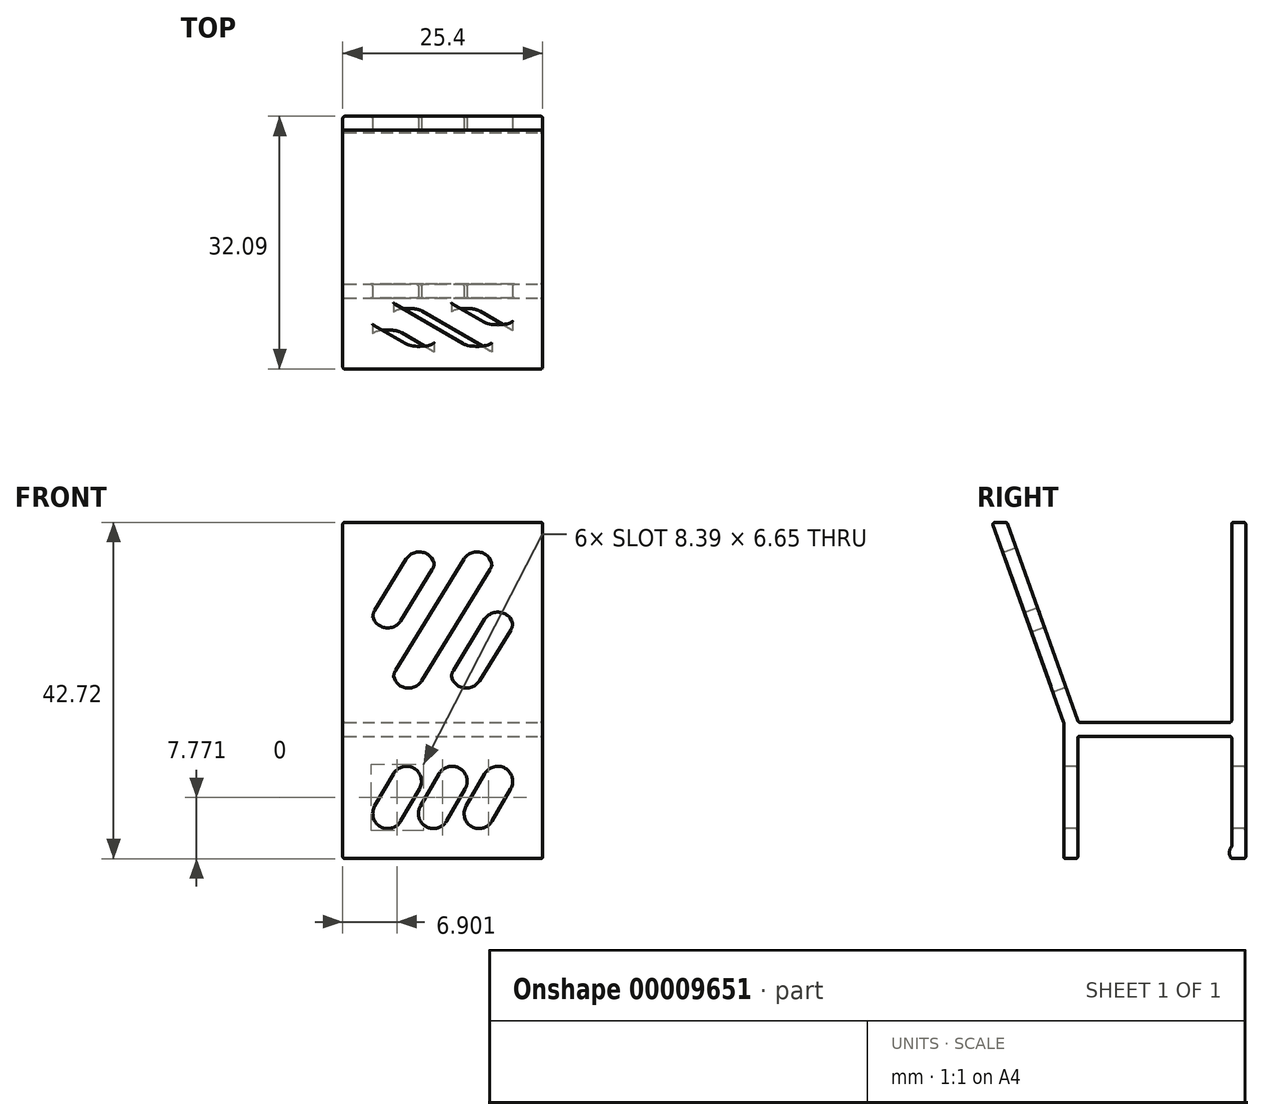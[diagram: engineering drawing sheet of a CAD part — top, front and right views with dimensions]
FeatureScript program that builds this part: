
annotation { "Feature Type Name" : "Feature", "Feature Type Description" : "" }
export const myFeature = defineFeature(function(context is Context, id is Id, definition is map)
    precondition{}
    {
        {
            var Q0;
            Q0=qCreatedBy(makeId("Right.planeOp"),FACE);
            var sketch = newSketch(context, id + "F0", { "sketchPlane" : qUnion([Q0])});
            skLineSegment(sketch, "E0.rect.bottom", {"start": v(9.78, 0.89) * mm, "end": v(-9.67, 0.89) * mm});
            skLineSegment(sketch, "E0.rect.top", {"start": v(9.78, -0.89) * mm, "end": v(-9.78, -0.89) * mm});
            skLineSegment(sketch, "E0.rect.left", {"start": v(11.56, 0.89) * mm, "end": v(11.56, -0.89) * mm});
            skLineSegment(sketch, "E0.rect.right", {"start": v(-11.56, 0.89) * mm, "end": v(-11.56, -0.89) * mm});
            skPoint(sketch, "E0.rect.middle", {"position": v(0, 0) * mm});
            skLineSegment(sketch, "E1.top", {"start": v(11.56, 26.29) * mm, "end": v(9.78, 26.29) * mm});
            skLineSegment(sketch, "E1.left", {"start": v(11.56, 0.89) * mm, "end": v(11.56, 26.29) * mm});
            skLineSegment(sketch, "E1.right", {"start": v(9.78, 0.89) * mm, "end": v(9.78, 26.29) * mm});
            skLineSegment(sketch, "E2", {"start": v(-11.56, 0.89) * mm, "end": v(-20.64, 26.29) * mm});
            skLineSegment(sketch, "E3", {"start": v(-20.64, 26.29) * mm, "end": v(-18.75, 26.29) * mm});
            skLineSegment(sketch, "E4", {"start": v(-18.75, 26.29) * mm, "end": v(-9.67, 0.89) * mm});
            skLineSegment(sketch, "E5.top", {"start": v(-11.56, -16.43) * mm, "end": v(-9.78, -16.43) * mm});
            skLineSegment(sketch, "E5.left", {"start": v(-11.56, -0.89) * mm, "end": v(-11.56, -16.43) * mm});
            skLineSegment(sketch, "E5.right", {"start": v(-9.78, -0.89) * mm, "end": v(-9.78, -16.43) * mm});
            skLineSegment(sketch, "E6.top", {"start": v(11.56, -16.43) * mm, "end": v(9.78, -16.43) * mm});
            skLineSegment(sketch, "E6.left", {"start": v(11.56, -0.89) * mm, "end": v(11.56, -16.43) * mm});
            skLineSegment(sketch, "E6.right", {"start": v(9.78, -0.89) * mm, "end": v(9.78, -14.9) * mm});
            skArc(sketch, "E7", {"start": v(9.78, -14.9) * mm, "mid": v(9.49, -15.67) * mm, "end": v(9.78, -16.43) * mm});
            skSolve(sketch);
        }
        {
            var Q0;
            Q0 = qSketchRegion(id + "F0", true);
            extrude(context, id + "F1", {"entities" : qUnion([Q0]), "oppositeDirection" : true, "depth" : 25.4 * mm});
        }
        {
            var Q0;
            Q0=makeQuery(id+"F1.opExtrude","SWEPT_FACE",FACE,{"disambiguationData":[OSD([sQuery(id+"F0.wireOp",EDGE,"E0.rect.right"),sQuery(id+"F0.wireOp",EDGE,"E5.left")])]});
            var sketch = newSketch(context, id + "F2", { "sketchPlane" : qUnion([Q0])});
            skLineSegment(sketch, "E8", {"start": v(0, 0) * mm, "end": v(-25.4, 0) * mm, "construction": true});
            skLineSegment(sketch, "E9", {"start": v(0, -0.89) * mm, "end": v(-25.4, -0.89) * mm, "construction": true});
            skArc(sketch, "E10", {"start": v(-21.33, -9.76) * mm, "mid": v(-20.64, -12.36) * mm, "end": v(-18.04, -11.67) * mm});
            skArc(sketch, "E11", {"start": v(-15.66, -7.56) * mm, "mid": v(-16.36, -4.95) * mm, "end": v(-18.96, -5.65) * mm});
            skLineSegment(sketch, "E12", {"start": v(-19.69, -10.71) * mm, "end": v(-17.31, -6.6) * mm, "construction": true});
            skLineSegment(sketch, "E13", {"start": v(-19.69, -10.71) * mm, "end": v(-10.98, -10.71) * mm, "construction": true});
            skLineSegment(sketch, "E14", {"start": v(-18.96, -5.65) * mm, "end": v(-21.33, -9.76) * mm});
            skLineSegment(sketch, "E15", {"start": v(-15.66, -7.56) * mm, "end": v(-18.04, -11.67) * mm});
            skArc(sketch, "E16.1.0.0", {"start": v(-9.86, -7.56) * mm, "mid": v(-10.56, -4.95) * mm, "end": v(-13.16, -5.65) * mm});
            skLineSegment(sketch, "E16.1.0.1", {"start": v(-13.16, -5.65) * mm, "end": v(-15.54, -9.76) * mm});
            skArc(sketch, "E16.1.0.2", {"start": v(-15.54, -9.76) * mm, "mid": v(-14.84, -12.36) * mm, "end": v(-12.24, -11.67) * mm});
            skLineSegment(sketch, "E16.1.0.3", {"start": v(-9.86, -7.56) * mm, "end": v(-12.24, -11.67) * mm});
            skArc(sketch, "E16.2.0.0", {"start": v(-4.07, -7.56) * mm, "mid": v(-4.76, -4.95) * mm, "end": v(-7.36, -5.65) * mm});
            skLineSegment(sketch, "E16.2.0.1", {"start": v(-7.36, -5.65) * mm, "end": v(-9.74, -9.76) * mm});
            skArc(sketch, "E16.2.0.2", {"start": v(-9.74, -9.76) * mm, "mid": v(-9.04, -12.36) * mm, "end": v(-6.44, -11.67) * mm});
            skLineSegment(sketch, "E16.2.0.3", {"start": v(-4.07, -7.56) * mm, "end": v(-6.44, -11.67) * mm});
            skLineSegment(sketch, "E16.direction1", {"start": v(-18.96, -5.65) * mm, "end": v(-13.16, -5.65) * mm, "construction": true});
            skSolve(sketch);
        }
        {
            var Q0;
            Q0 = qSketchRegion(id + "F2", true);
            extrude(context, id + "F3", {"entities" : qUnion([Q0]), "operationType" : NewBodyOperationType.REMOVE, "endBound" : BoundingType.THROUGH_ALL, "oppositeDirection" : true, "depth" : 25.4 * mm});
        }
        {
            var Q0;
            Q0=makeQuery(id+"F1.opExtrude","SWEPT_FACE",FACE,{"disambiguationData":[OSD([sQuery(id+"F0.wireOp",EDGE,"E2")])]});
            var sketch = newSketch(context, id + "F4", { "sketchPlane" : qUnion([Q0])});
            skArc(sketch, "E17", {"start": v(-18.7, 11.65) * mm, "mid": v(-18, 9.05) * mm, "end": v(-15.4, 9.75) * mm});
            skArc(sketch, "E18", {"start": v(-6.7, 24.78) * mm, "mid": v(-7.4, 27.39) * mm, "end": v(-10, 26.69) * mm});
            skLineSegment(sketch, "E19", {"start": v(-17.04, 10.7) * mm, "end": v(-9.9, 10.7) * mm, "construction": true});
            skLineSegment(sketch, "E20", {"start": v(-17.04, 10.7) * mm, "end": v(-8.36, 25.74) * mm, "construction": true});
            skLineSegment(sketch, "E21", {"start": v(-10, 26.69) * mm, "end": v(-18.7, 11.65) * mm});
            skLineSegment(sketch, "E22", {"start": v(-6.7, 24.78) * mm, "end": v(-15.4, 9.75) * mm});
            skLineSegment(sketch, "E23.0", {"start": v(-21.33, 19.77) * mm, "end": v(-17.34, 26.69) * mm});
            skLineSegment(sketch, "E24.0", {"start": v(-18.04, 17.87) * mm, "end": v(-14.04, 24.78) * mm});
            skArc(sketch, "E25", {"start": v(-17.34, 26.69) * mm, "mid": v(-14.74, 27.39) * mm, "end": v(-14.04, 24.78) * mm});
            skArc(sketch, "E26", {"start": v(-18.04, 17.87) * mm, "mid": v(-20.64, 17.17) * mm, "end": v(-21.33, 19.77) * mm});
            skLineSegment(sketch, "E27", {"start": v(4.18, 27.64) * mm, "end": v(-28.96, 27.64) * mm, "construction": true});
            skLineSegment(sketch, "E28", {"start": v(-29.07, 8.8) * mm, "end": v(4.54, 8.8) * mm, "construction": true});
            skLineSegment(sketch, "E29", {"start": v(-21.6, 33.76) * mm, "end": v(-21.59, -9.95) * mm, "construction": true});
            skLineSegment(sketch, "E30", {"start": v(-3.81, 33.76) * mm, "end": v(-3.8, -10.03) * mm, "construction": true});
            skLineSegment(sketch, "E31.0.MirrorCS", {"start": v(-8.06, 9.75) * mm, "end": v(-4.07, 16.66) * mm});
            skArc(sketch, "E32.0.MirrorCS", {"start": v(-4.07, 16.66) * mm, "mid": v(-4.76, 19.26) * mm, "end": v(-7.36, 18.57) * mm});
            skLineSegment(sketch, "E33.0.MirrorCS", {"start": v(-11.36, 11.65) * mm, "end": v(-7.36, 18.57) * mm});
            skArc(sketch, "E34", {"start": v(-8.06, 9.75) * mm, "mid": v(-10.66, 9.05) * mm, "end": v(-11.36, 11.65) * mm});
            skLineSegment(sketch, "E35", {"start": v(-12.7, 18.22) * mm, "end": v(-21.59, 18.22) * mm, "construction": true});
            skSolve(sketch);
        }
        {
            var Q0;
            Q0 = qSketchRegion(id + "F4", true);
            extrude(context, id + "F5", {"entities" : qUnion([Q0]), "operationType" : NewBodyOperationType.REMOVE, "endBound" : BoundingType.UP_TO_NEXT, "oppositeDirection" : true, "depth" : 25.4 * mm});
        }
        {
            var Q0;
            Q0=makeQuery(id+"F5.boolean.opBoolean","COPY",FACE,{"derivedFrom":makeQuery(id+"F5.opExtrude","SWEPT_FACE",FACE,{"disambiguationData":[OSD([sQuery(id+"F4.wireOp",EDGE,"f82c8603-6a34-46cd-9305-3e979d524e24.6.0.1")])]})});
            var Q1;
            Q1=makeQuery(id+"F5.boolean.opBoolean","COPY",EDGE,{"derivedFrom":makeQuery(id+"F5.opExtrude","CAP_EDGE",EDGE,{"disambiguationData":[OSD([sQuery(id+"F4.wireOp",EDGE,"f82c8603-6a34-46cd-9305-3e979d524e24.2.0.2")])],"isStart":true})});
            var Q2;
            Q2=makeQuery(id+"F5.boolean.opBoolean","COPY",EDGE,{"derivedFrom":makeQuery(id+"F5.opExtrude","CAP_EDGE",EDGE,{"disambiguationData":[OSD([sQuery(id+"F4.wireOp",EDGE,"f82c8603-6a34-46cd-9305-3e979d524e24.6.0.2")])],"isStart":true})});
            var Q3;
            Q3=makeQuery(id+"F5.boolean.opBoolean","COPY",EDGE,{"derivedFrom":makeQuery(id+"F5.opExtrude","CAP_EDGE",EDGE,{"disambiguationData":[OSD([sQuery(id+"F4.wireOp",EDGE,"f82c8603-6a34-46cd-9305-3e979d524e24.6.0.0")])],"isStart":true})});
            var Q4;
            Q4=makeQuery(id+"F5.boolean.opBoolean","COPY",FACE,{"derivedFrom":makeQuery(id+"F5.opExtrude","SWEPT_FACE",FACE,{"disambiguationData":[OSD([sQuery(id+"F4.wireOp",EDGE,"f82c8603-6a34-46cd-9305-3e979d524e24.6.0.0")])]})});
            var Q5;
            Q5=makeQuery(id+"F5.boolean.opBoolean","COPY",EDGE,{"derivedFrom":makeQuery(id+"F5.opExtrude","CAP_EDGE",EDGE,{"disambiguationData":[OSD([sQuery(id+"F4.wireOp",EDGE,"f82c8603-6a34-46cd-9305-3e979d524e24.2.0.1")])],"isStart":true})});
            var Q6;
            Q6=makeQuery(id+"F5.boolean.opBoolean","COPY",FACE,{"derivedFrom":makeQuery(id+"F5.opExtrude","SWEPT_FACE",FACE,{"disambiguationData":[OSD([sQuery(id+"F4.wireOp",EDGE,"f82c8603-6a34-46cd-9305-3e979d524e24.5.0.3")])]})});
            var Q7;
            Q7=makeQuery(id+"F5.boolean.opBoolean","COPY",EDGE,{"derivedFrom":makeQuery(id+"F5.opExtrude","TWEAK_EDGE",EDGE,{"derivedFrom":[makeQuery(id+"F1.opExtrude","SWEPT_FACE",FACE,{"disambiguationData":[OSD([sQuery(id+"F0.wireOp",EDGE,"E4")])]}),makeQuery(id+"F4.imprint","IMPRINT",EDGE,{"derivedFrom":sQuery(id+"F4.wireOp",EDGE,"f82c8603-6a34-46cd-9305-3e979d524e24.5.0.3")})]})});
            var Q8;
            Q8=makeQuery(id+"F5.boolean.opBoolean","COPY",EDGE,{"derivedFrom":makeQuery(id+"F5.opExtrude","CAP_EDGE",EDGE,{"disambiguationData":[OSD([sQuery(id+"F4.wireOp",EDGE,"f82c8603-6a34-46cd-9305-3e979d524e24.5.0.3")])],"isStart":true})});
            var Q9;
            Q9=makeQuery(id+"F5.boolean.opBoolean","COPY",EDGE,{"derivedFrom":makeQuery(id+"F5.opExtrude","CAP_EDGE",EDGE,{"disambiguationData":[OSD([sQuery(id+"F4.wireOp",EDGE,"f82c8603-6a34-46cd-9305-3e979d524e24.1.0.3")])],"isStart":true})});
            var Q10;
            Q10=makeQuery(id+"F5.boolean.opBoolean","COPY",FACE,{"derivedFrom":makeQuery(id+"F5.opExtrude","SWEPT_FACE",FACE,{"disambiguationData":[OSD([sQuery(id+"F4.wireOp",EDGE,"f82c8603-6a34-46cd-9305-3e979d524e24.5.0.2")])]})});
            var Q11;
            Q11=makeQuery(id+"F3.boolean.opBoolean","COPY",FACE,{"disambiguationData":[OD(0.0)],"derivedFrom":makeQuery(id+"F3.opExtrude","SWEPT_FACE",FACE,{"disambiguationData":[OSD([sQuery(id+"F2.wireOp",EDGE,"E16.4.0.1")])]})});
            var Q12;
            Q12=makeQuery(id+"F3.boolean.opBoolean","COPY",FACE,{"disambiguationData":[OD(0.0)],"derivedFrom":makeQuery(id+"F3.opExtrude","SWEPT_FACE",FACE,{"disambiguationData":[OSD([sQuery(id+"F2.wireOp",EDGE,"E16.2.0.1")])]})});
            var Q13;
            Q13=makeQuery(id+"F3.boolean.opBoolean","COPY",EDGE,{"derivedFrom":makeQuery(id+"F3.opExtrude","CAP_EDGE",EDGE,{"disambiguationData":[OSD([sQuery(id+"F2.wireOp",EDGE,"E16.5.0.3")])],"isStart":true})});
            var Q14;
            Q14=makeQuery(id+"F3.boolean.opBoolean","INTERSECT",EDGE,{"derivedFrom":[makeQuery(id+"F1.opExtrude","SWEPT_FACE",FACE,{"disambiguationData":[OSD([sQuery(id+"F0.wireOp",EDGE,"E5.right")])]}),makeQuery(id+"F3.opExtrude","SWEPT_FACE",FACE,{"disambiguationData":[OSD([sQuery(id+"F2.wireOp",EDGE,"E16.2.0.2")])]})]});
            var Q15;
            Q15=makeQuery(id+"F5.boolean.opBoolean","COPY",FACE,{"derivedFrom":makeQuery(id+"F5.opExtrude","SWEPT_FACE",FACE,{"disambiguationData":[OSD([sQuery(id+"F4.wireOp",EDGE,"f82c8603-6a34-46cd-9305-3e979d524e24.7.0.0")])]})});
            var Q16;
            Q16=makeQuery(id+"F3.boolean.opBoolean","COPY",FACE,{"disambiguationData":[OD(0.0)],"derivedFrom":makeQuery(id+"F3.opExtrude","SWEPT_FACE",FACE,{"disambiguationData":[OSD([sQuery(id+"F2.wireOp",EDGE,"E16.6.0.2")])]})});
            var Q17;
            Q17=makeQuery(id+"F3.boolean.opBoolean","COPY",FACE,{"disambiguationData":[OD(0.0)],"derivedFrom":makeQuery(id+"F3.opExtrude","SWEPT_FACE",FACE,{"disambiguationData":[OSD([sQuery(id+"F2.wireOp",EDGE,"E16.2.0.2")])]})});
            var Q18;
            Q18=makeQuery(id+"F3.boolean.opBoolean","COPY",FACE,{"disambiguationData":[OD(0.0)],"derivedFrom":makeQuery(id+"F3.opExtrude","SWEPT_FACE",FACE,{"disambiguationData":[OSD([sQuery(id+"F2.wireOp",EDGE,"E16.4.0.2")])]})});
            var Q19;
            Q19=makeQuery(id+"F3.boolean.opBoolean","COPY",EDGE,{"derivedFrom":makeQuery(id+"F3.opExtrude","CAP_EDGE",EDGE,{"disambiguationData":[OSD([sQuery(id+"F2.wireOp",EDGE,"E16.6.0.1")])],"isStart":true})});
            var Q20;
            Q20=makeQuery(id+"F3.boolean.opBoolean","INTERSECT",EDGE,{"derivedFrom":[makeQuery(id+"F1.opExtrude","SWEPT_FACE",FACE,{"disambiguationData":[OSD([sQuery(id+"F0.wireOp",EDGE,"E5.right")])]}),makeQuery(id+"F3.opExtrude","SWEPT_FACE",FACE,{"disambiguationData":[OSD([sQuery(id+"F2.wireOp",EDGE,"E16.2.0.1")])]})]});
            var Q21;
            Q21=makeQuery(id+"F5.boolean.opBoolean","COPY",FACE,{"derivedFrom":makeQuery(id+"F5.opExtrude","SWEPT_FACE",FACE,{"disambiguationData":[OSD([sQuery(id+"F4.wireOp",EDGE,"f82c8603-6a34-46cd-9305-3e979d524e24.6.0.3")])]})});
            var Q22;
            Q22=makeQuery(id+"F5.boolean.opBoolean","COPY",EDGE,{"derivedFrom":makeQuery(id+"F5.opExtrude","CAP_EDGE",EDGE,{"disambiguationData":[OSD([sQuery(id+"F4.wireOp",EDGE,"f82c8603-6a34-46cd-9305-3e979d524e24.7.0.0")])],"isStart":true})});
            var Q23;
            Q23=makeQuery(id+"F3.boolean.opBoolean","COPY",EDGE,{"derivedFrom":makeQuery(id+"F3.opExtrude","CAP_EDGE",EDGE,{"disambiguationData":[OSD([sQuery(id+"F2.wireOp",EDGE,"E16.6.0.3")])],"isStart":true})});
            var Q24;
            Q24=makeQuery(id+"F5.boolean.opBoolean","COPY",EDGE,{"derivedFrom":makeQuery(id+"F5.opExtrude","TWEAK_EDGE",EDGE,{"derivedFrom":[makeQuery(id+"F1.opExtrude","SWEPT_FACE",FACE,{"disambiguationData":[OSD([sQuery(id+"F0.wireOp",EDGE,"E4")])]}),makeQuery(id+"F4.imprint","IMPRINT",EDGE,{"derivedFrom":sQuery(id+"F4.wireOp",EDGE,"f82c8603-6a34-46cd-9305-3e979d524e24.6.0.3")})]})});
            var Q25;
            Q25=makeQuery(id+"F5.boolean.opBoolean","COPY",EDGE,{"derivedFrom":makeQuery(id+"F5.opExtrude","CAP_EDGE",EDGE,{"disambiguationData":[OSD([sQuery(id+"F4.wireOp",EDGE,"f82c8603-6a34-46cd-9305-3e979d524e24.6.0.3")])],"isStart":true})});
            var Q26;
            Q26=makeQuery(id+"F5.boolean.opBoolean","COPY",EDGE,{"derivedFrom":makeQuery(id+"F5.opExtrude","CAP_EDGE",EDGE,{"disambiguationData":[OSD([sQuery(id+"F4.wireOp",EDGE,"f82c8603-6a34-46cd-9305-3e979d524e24.2.0.3")])],"isStart":true})});
            var Q27;
            Q27=makeQuery(id+"F1.opExtrude","CAP_EDGE",EDGE,{"disambiguationData":[OSD([sQuery(id+"F0.wireOp",EDGE,"E1.right")])],"isStart":false});
            var Q28;
            Q28=makeQuery(id+"F3.boolean.opBoolean","COPY",FACE,{"disambiguationData":[OD(0.0)],"derivedFrom":makeQuery(id+"F3.opExtrude","SWEPT_FACE",FACE,{"disambiguationData":[OSD([sQuery(id+"F2.wireOp",EDGE,"E16.5.0.0")])]})});
            var Q29;
            Q29=makeQuery(id+"F3.boolean.opBoolean","COPY",FACE,{"disambiguationData":[OD(0.0)],"derivedFrom":makeQuery(id+"F3.opExtrude","SWEPT_FACE",FACE,{"disambiguationData":[OSD([sQuery(id+"F2.wireOp",EDGE,"E16.3.0.0")])]})});
            var Q30;
            Q30=makeQuery(id+"F3.boolean.opBoolean","COPY",FACE,{"disambiguationData":[OD(0.0)],"derivedFrom":makeQuery(id+"F3.opExtrude","SWEPT_FACE",FACE,{"disambiguationData":[OSD([sQuery(id+"F2.wireOp",EDGE,"E16.7.0.0")])]})});
            var Q31;
            Q31=makeQuery(id+"F1.opExtrude","CAP_EDGE",EDGE,{"disambiguationData":[OSD([sQuery(id+"F0.wireOp",EDGE,"E6.right")])],"isStart":true});
            var Q32;
            Q32=makeQuery(id+"F1.opExtrude","CAP_EDGE",EDGE,{"disambiguationData":[OSD([sQuery(id+"F0.wireOp",EDGE,"E0.rect.right"),sQuery(id+"F0.wireOp",EDGE,"E5.left")])],"isStart":true});
            var Q33;
            Q33=makeQuery(id+"F3.boolean.opBoolean","INTERSECT",EDGE,{"derivedFrom":[makeQuery(id+"F1.opExtrude","SWEPT_FACE",FACE,{"disambiguationData":[OSD([sQuery(id+"F0.wireOp",EDGE,"E5.right")])]}),makeQuery(id+"F3.opExtrude","SWEPT_FACE",FACE,{"disambiguationData":[OSD([sQuery(id+"F2.wireOp",EDGE,"E16.5.0.1")])]})]});
            var Q34;
            Q34=makeQuery(id+"F3.boolean.opBoolean","COPY",EDGE,{"derivedFrom":makeQuery(id+"F3.opExtrude","CAP_EDGE",EDGE,{"disambiguationData":[OSD([sQuery(id+"F2.wireOp",EDGE,"E16.5.0.1")])],"isStart":true})});
            var Q35;
            Q35=makeQuery(id+"F3.boolean.opBoolean","COPY",EDGE,{"derivedFrom":makeQuery(id+"F3.opExtrude","CAP_EDGE",EDGE,{"disambiguationData":[OSD([sQuery(id+"F2.wireOp",EDGE,"E16.5.0.0")])],"isStart":true})});
            var Q36;
            Q36=makeQuery(id+"F3.boolean.opBoolean","COPY",FACE,{"disambiguationData":[OD(0.0)],"derivedFrom":makeQuery(id+"F3.opExtrude","SWEPT_FACE",FACE,{"disambiguationData":[OSD([sQuery(id+"F2.wireOp",EDGE,"E16.6.0.0")])]})});
            var Q37;
            Q37=makeQuery(id+"F3.boolean.opBoolean","COPY",FACE,{"disambiguationData":[OD(0.0)],"derivedFrom":makeQuery(id+"F3.opExtrude","SWEPT_FACE",FACE,{"disambiguationData":[OSD([sQuery(id+"F2.wireOp",EDGE,"E16.4.0.0")])]})});
            var Q38;
            Q38=makeQuery(id+"F3.boolean.opBoolean","COPY",FACE,{"disambiguationData":[OD(0.0)],"derivedFrom":makeQuery(id+"F3.opExtrude","SWEPT_FACE",FACE,{"disambiguationData":[OSD([sQuery(id+"F2.wireOp",EDGE,"E16.2.0.0")])]})});
            var Q39;
            Q39=makeQuery(id+"F1.opExtrude","CAP_EDGE",EDGE,{"disambiguationData":[OSD([sQuery(id+"F0.wireOp",EDGE,"E0.rect.top")])],"isStart":true});
            var Q40;
            Q40=makeQuery(id+"F3.boolean.opBoolean","COPY",EDGE,{"derivedFrom":makeQuery(id+"F3.opExtrude","CAP_EDGE",EDGE,{"disambiguationData":[OSD([sQuery(id+"F2.wireOp",EDGE,"E16.4.0.3")])],"isStart":true})});
            var Q41;
            Q41=makeQuery(id+"F3.boolean.opBoolean","COPY",FACE,{"disambiguationData":[OD(1.0)],"derivedFrom":makeQuery(id+"F3.opExtrude","SWEPT_FACE",FACE,{"disambiguationData":[OSD([sQuery(id+"F2.wireOp",EDGE,"E16.7.0.3")])]})});
            var Q42;
            Q42=makeQuery(id+"F5.boolean.opBoolean","COPY",FACE,{"derivedFrom":makeQuery(id+"F5.opExtrude","SWEPT_FACE",FACE,{"disambiguationData":[OSD([sQuery(id+"F4.wireOp",EDGE,"f82c8603-6a34-46cd-9305-3e979d524e24.7.0.3")])]})});
            var Q43;
            Q43=makeQuery(id+"F1.opExtrude","CAP_EDGE",EDGE,{"disambiguationData":[OSD([sQuery(id+"F0.wireOp",EDGE,"E0.rect.left"),sQuery(id+"F0.wireOp",EDGE,"E1.left"),sQuery(id+"F0.wireOp",EDGE,"E6.left")])],"isStart":true});
            var Q44;
            Q44=makeQuery(id+"F1.opExtrude","CAP_EDGE",EDGE,{"disambiguationData":[OSD([sQuery(id+"F0.wireOp",EDGE,"E5.right")])],"isStart":true});
            var Q45;
            Q45=makeQuery(id+"F3.boolean.opBoolean","INTERSECT",EDGE,{"derivedFrom":[makeQuery(id+"F1.opExtrude","SWEPT_FACE",FACE,{"disambiguationData":[OSD([sQuery(id+"F0.wireOp",EDGE,"E5.right")])]}),makeQuery(id+"F3.opExtrude","SWEPT_FACE",FACE,{"disambiguationData":[OSD([sQuery(id+"F2.wireOp",EDGE,"E14")])]})]});
            var Q46;
            Q46=makeQuery(id+"F3.boolean.opBoolean","INTERSECT",EDGE,{"derivedFrom":[makeQuery(id+"F1.opExtrude","SWEPT_FACE",FACE,{"disambiguationData":[OSD([sQuery(id+"F0.wireOp",EDGE,"E5.right")])]}),makeQuery(id+"F3.opExtrude","SWEPT_FACE",FACE,{"disambiguationData":[OSD([sQuery(id+"F2.wireOp",EDGE,"E16.4.0.2")])]})]});
            var Q47;
            Q47=makeQuery(id+"F3.boolean.opBoolean","COPY",FACE,{"disambiguationData":[OD(0.0)],"derivedFrom":makeQuery(id+"F3.opExtrude","SWEPT_FACE",FACE,{"disambiguationData":[OSD([sQuery(id+"F2.wireOp",EDGE,"E16.3.0.2")])]})});
            var Q48;
            Q48=makeQuery(id+"F3.boolean.opBoolean","COPY",FACE,{"disambiguationData":[OD(0.0)],"derivedFrom":makeQuery(id+"F3.opExtrude","SWEPT_FACE",FACE,{"disambiguationData":[OSD([sQuery(id+"F2.wireOp",EDGE,"E16.1.0.2")])]})});
            var Q49;
            Q49=makeQuery(id+"F3.boolean.opBoolean","COPY",FACE,{"disambiguationData":[OD(0.0)],"derivedFrom":makeQuery(id+"F3.opExtrude","SWEPT_FACE",FACE,{"disambiguationData":[OSD([sQuery(id+"F2.wireOp",EDGE,"E16.7.0.2")])]})});
            var Q50;
            Q50=makeQuery(id+"F3.boolean.opBoolean","COPY",FACE,{"disambiguationData":[OD(0.0)],"derivedFrom":makeQuery(id+"F3.opExtrude","SWEPT_FACE",FACE,{"disambiguationData":[OSD([sQuery(id+"F2.wireOp",EDGE,"E16.5.0.2")])]})});
            var Q51;
            Q51=makeQuery(id+"F3.boolean.opBoolean","COPY",FACE,{"disambiguationData":[OD(1.0)],"derivedFrom":makeQuery(id+"F3.opExtrude","SWEPT_FACE",FACE,{"disambiguationData":[OSD([sQuery(id+"F2.wireOp",EDGE,"E16.7.0.2")])]})});
            var Q52;
            Q52=makeQuery(id+"F3.boolean.opBoolean","INTERSECT",EDGE,{"derivedFrom":[makeQuery(id+"F1.opExtrude","SWEPT_FACE",FACE,{"disambiguationData":[OSD([sQuery(id+"F0.wireOp",EDGE,"E5.right")])]}),makeQuery(id+"F3.opExtrude","SWEPT_FACE",FACE,{"disambiguationData":[OSD([sQuery(id+"F2.wireOp",EDGE,"E16.4.0.1")])]})]});
            var Q53;
            Q53=makeQuery(id+"F5.boolean.opBoolean","COPY",FACE,{"derivedFrom":makeQuery(id+"F5.opExtrude","SWEPT_FACE",FACE,{"disambiguationData":[OSD([sQuery(id+"F4.wireOp",EDGE,"f82c8603-6a34-46cd-9305-3e979d524e24.7.0.1")])]})});
            var Q54;
            Q54=makeQuery(id+"F3.boolean.opBoolean","COPY",EDGE,{"derivedFrom":makeQuery(id+"F3.opExtrude","CAP_EDGE",EDGE,{"disambiguationData":[OSD([sQuery(id+"F2.wireOp",EDGE,"E16.4.0.1")])],"isStart":true})});
            var Q55;
            Q55=makeQuery(id+"F5.boolean.opBoolean","COPY",EDGE,{"derivedFrom":makeQuery(id+"F5.opExtrude","CAP_EDGE",EDGE,{"disambiguationData":[OSD([sQuery(id+"F4.wireOp",EDGE,"f82c8603-6a34-46cd-9305-3e979d524e24.3.0.1")])],"isStart":true})});
            var Q56;
            Q56=makeQuery(id+"F5.boolean.opBoolean","COPY",FACE,{"derivedFrom":makeQuery(id+"F5.opExtrude","SWEPT_FACE",FACE,{"disambiguationData":[OSD([sQuery(id+"F4.wireOp",EDGE,"f82c8603-6a34-46cd-9305-3e979d524e24.7.0.2")])]})});
            var Q57;
            Q57=makeQuery(id+"F5.boolean.opBoolean","COPY",EDGE,{"derivedFrom":makeQuery(id+"F5.opExtrude","CAP_EDGE",EDGE,{"disambiguationData":[OSD([sQuery(id+"F4.wireOp",EDGE,"f82c8603-6a34-46cd-9305-3e979d524e24.3.0.2")])],"isStart":true})});
            var Q58;
            Q58=makeQuery(id+"F5.boolean.opBoolean","COPY",EDGE,{"derivedFrom":makeQuery(id+"F5.opExtrude","CAP_EDGE",EDGE,{"disambiguationData":[OSD([sQuery(id+"F4.wireOp",EDGE,"f82c8603-6a34-46cd-9305-3e979d524e24.7.0.2")])],"isStart":true})});
            var Q59;
            Q59=makeQuery(id+"F5.boolean.opBoolean","COPY",EDGE,{"derivedFrom":makeQuery(id+"F5.opExtrude","CAP_EDGE",EDGE,{"disambiguationData":[OSD([sQuery(id+"F4.wireOp",EDGE,"f82c8603-6a34-46cd-9305-3e979d524e24.7.0.3")])],"isStart":true})});
            var Q60;
            Q60=makeQuery(id+"F5.boolean.opBoolean","COPY",EDGE,{"derivedFrom":makeQuery(id+"F5.opExtrude","CAP_EDGE",EDGE,{"disambiguationData":[OSD([sQuery(id+"F4.wireOp",EDGE,"f82c8603-6a34-46cd-9305-3e979d524e24.3.0.3")])],"isStart":true})});
            var Q61;
            Q61=makeQuery(id+"F5.boolean.opBoolean","COPY",EDGE,{"derivedFrom":makeQuery(id+"F5.opExtrude","TWEAK_EDGE",EDGE,{"derivedFrom":[makeQuery(id+"F1.opExtrude","SWEPT_FACE",FACE,{"disambiguationData":[OSD([sQuery(id+"F0.wireOp",EDGE,"E4")])]}),makeQuery(id+"F4.imprint","IMPRINT",EDGE,{"derivedFrom":sQuery(id+"F4.wireOp",EDGE,"f82c8603-6a34-46cd-9305-3e979d524e24.7.0.3")})]})});
            var Q62;
            Q62=makeQuery(id+"F3.boolean.opBoolean","COPY",EDGE,{"derivedFrom":makeQuery(id+"F3.opExtrude","CAP_EDGE",EDGE,{"disambiguationData":[OSD([sQuery(id+"F2.wireOp",EDGE,"E16.7.0.3")])],"isStart":true})});
            var Q63;
            Q63=makeQuery(id+"F3.boolean.opBoolean","INTERSECT",EDGE,{"derivedFrom":[makeQuery(id+"F1.opExtrude","SWEPT_FACE",FACE,{"disambiguationData":[OSD([sQuery(id+"F0.wireOp",EDGE,"E6.right")])]}),makeQuery(id+"F3.opExtrude","SWEPT_FACE",FACE,{"disambiguationData":[OSD([sQuery(id+"F2.wireOp",EDGE,"E16.7.0.3")])]})]});
            var Q64;
            Q64=makeQuery(id+"F5.boolean.opBoolean","COPY",EDGE,{"derivedFrom":makeQuery(id+"F5.opExtrude","TWEAK_EDGE",EDGE,{"derivedFrom":[makeQuery(id+"F1.opExtrude","SWEPT_FACE",FACE,{"disambiguationData":[OSD([sQuery(id+"F0.wireOp",EDGE,"E4")])]}),makeQuery(id+"F4.imprint","IMPRINT",EDGE,{"derivedFrom":sQuery(id+"F4.wireOp",EDGE,"f82c8603-6a34-46cd-9305-3e979d524e24.1.0.1")})]})});
            var Q65;
            Q65=makeQuery(id+"F5.boolean.opBoolean","COPY",FACE,{"derivedFrom":makeQuery(id+"F5.opExtrude","SWEPT_FACE",FACE,{"disambiguationData":[OSD([sQuery(id+"F4.wireOp",EDGE,"f82c8603-6a34-46cd-9305-3e979d524e24.1.0.1")])]})});
            var Q66;
            Q66=makeQuery(id+"F5.boolean.opBoolean","COPY",FACE,{"derivedFrom":makeQuery(id+"F5.opExtrude","SWEPT_FACE",FACE,{"disambiguationData":[OSD([sQuery(id+"F4.wireOp",EDGE,"f82c8603-6a34-46cd-9305-3e979d524e24.1.0.2")])]})});
            var Q67;
            Q67=makeQuery(id+"F3.boolean.opBoolean","INTERSECT",EDGE,{"derivedFrom":[makeQuery(id+"F1.opExtrude","SWEPT_FACE",FACE,{"disambiguationData":[OSD([sQuery(id+"F0.wireOp",EDGE,"E5.right")])]}),makeQuery(id+"F3.opExtrude","SWEPT_FACE",FACE,{"disambiguationData":[OSD([sQuery(id+"F2.wireOp",EDGE,"E16.3.0.2")])]})]});
            var Q68;
            Q68=makeQuery(id+"F5.boolean.opBoolean","COPY",FACE,{"derivedFrom":makeQuery(id+"F5.opExtrude","SWEPT_FACE",FACE,{"disambiguationData":[OSD([sQuery(id+"F4.wireOp",EDGE,"f82c8603-6a34-46cd-9305-3e979d524e24.1.0.3")])]})});
            var Q69;
            Q69=makeQuery(id+"F5.boolean.opBoolean","COPY",FACE,{"derivedFrom":makeQuery(id+"F5.opExtrude","SWEPT_FACE",FACE,{"disambiguationData":[OSD([sQuery(id+"F4.wireOp",EDGE,"E18")])]})});
            var Q70;
            Q70=makeQuery(id+"F3.boolean.opBoolean","COPY",EDGE,{"derivedFrom":makeQuery(id+"F3.opExtrude","CAP_EDGE",EDGE,{"disambiguationData":[OSD([sQuery(id+"F2.wireOp",EDGE,"E16.7.0.2")])],"isStart":true})});
            var Q71;
            Q71=makeQuery(id+"F5.boolean.opBoolean","COPY",FACE,{"derivedFrom":makeQuery(id+"F5.opExtrude","SWEPT_FACE",FACE,{"disambiguationData":[OSD([sQuery(id+"F4.wireOp",EDGE,"E21")])]})});
            var Q72;
            Q72=makeQuery(id+"F5.boolean.opBoolean","COPY",EDGE,{"derivedFrom":makeQuery(id+"F5.opExtrude","TWEAK_EDGE",EDGE,{"derivedFrom":[makeQuery(id+"F1.opExtrude","SWEPT_FACE",FACE,{"disambiguationData":[OSD([sQuery(id+"F0.wireOp",EDGE,"E4")])]}),makeQuery(id+"F4.imprint","IMPRINT",EDGE,{"derivedFrom":sQuery(id+"F4.wireOp",EDGE,"E21")})]})});
            var Q73;
            Q73=makeQuery(id+"F5.boolean.opBoolean","COPY",FACE,{"derivedFrom":makeQuery(id+"F5.opExtrude","SWEPT_FACE",FACE,{"disambiguationData":[OSD([sQuery(id+"F4.wireOp",EDGE,"f82c8603-6a34-46cd-9305-3e979d524e24.1.0.0")])]})});
            var Q74;
            Q74=makeQuery(id+"F5.boolean.opBoolean","COPY",FACE,{"derivedFrom":makeQuery(id+"F5.opExtrude","SWEPT_FACE",FACE,{"disambiguationData":[OSD([sQuery(id+"F4.wireOp",EDGE,"f82c8603-6a34-46cd-9305-3e979d524e24.3.0.0")])]})});
            var Q75;
            Q75=makeQuery(id+"F5.boolean.opBoolean","COPY",FACE,{"derivedFrom":makeQuery(id+"F5.opExtrude","SWEPT_FACE",FACE,{"disambiguationData":[OSD([sQuery(id+"F4.wireOp",EDGE,"f82c8603-6a34-46cd-9305-3e979d524e24.2.0.0")])]})});
            var Q76;
            Q76=makeQuery(id+"F3.boolean.opBoolean","COPY",FACE,{"disambiguationData":[OD(0.0)],"derivedFrom":makeQuery(id+"F3.opExtrude","SWEPT_FACE",FACE,{"disambiguationData":[OSD([sQuery(id+"F2.wireOp",EDGE,"E16.3.0.1")])]})});
            var Q77;
            Q77=makeQuery(id+"F5.boolean.opBoolean","COPY",FACE,{"derivedFrom":makeQuery(id+"F5.opExtrude","SWEPT_FACE",FACE,{"disambiguationData":[OSD([sQuery(id+"F4.wireOp",EDGE,"f82c8603-6a34-46cd-9305-3e979d524e24.2.0.1")])]})});
            var Q78;
            Q78=makeQuery(id+"F5.boolean.opBoolean","COPY",FACE,{"derivedFrom":makeQuery(id+"F5.opExtrude","SWEPT_FACE",FACE,{"disambiguationData":[OSD([sQuery(id+"F4.wireOp",EDGE,"f82c8603-6a34-46cd-9305-3e979d524e24.2.0.2")])]})});
            var Q79;
            Q79=makeQuery(id+"F5.boolean.opBoolean","COPY",FACE,{"derivedFrom":makeQuery(id+"F5.opExtrude","SWEPT_FACE",FACE,{"disambiguationData":[OSD([sQuery(id+"F4.wireOp",EDGE,"f82c8603-6a34-46cd-9305-3e979d524e24.2.0.3")])]})});
            var Q80;
            Q80=makeQuery(id+"F5.boolean.opBoolean","COPY",EDGE,{"derivedFrom":makeQuery(id+"F5.opExtrude","TWEAK_EDGE",EDGE,{"derivedFrom":[makeQuery(id+"F1.opExtrude","SWEPT_FACE",FACE,{"disambiguationData":[OSD([sQuery(id+"F0.wireOp",EDGE,"E4")])]}),makeQuery(id+"F4.imprint","IMPRINT",EDGE,{"derivedFrom":sQuery(id+"F4.wireOp",EDGE,"f82c8603-6a34-46cd-9305-3e979d524e24.2.0.3")})]})});
            var Q81;
            Q81=makeQuery(id+"F5.boolean.opBoolean","COPY",FACE,{"derivedFrom":makeQuery(id+"F5.opExtrude","SWEPT_FACE",FACE,{"disambiguationData":[OSD([sQuery(id+"F4.wireOp",EDGE,"f82c8603-6a34-46cd-9305-3e979d524e24.3.0.2")])]})});
            var Q82;
            Q82=makeQuery(id+"F5.boolean.opBoolean","COPY",EDGE,{"derivedFrom":makeQuery(id+"F5.opExtrude","TWEAK_EDGE",EDGE,{"derivedFrom":[makeQuery(id+"F1.opExtrude","SWEPT_FACE",FACE,{"disambiguationData":[OSD([sQuery(id+"F0.wireOp",EDGE,"E4")])]}),makeQuery(id+"F4.imprint","IMPRINT",EDGE,{"derivedFrom":sQuery(id+"F4.wireOp",EDGE,"f82c8603-6a34-46cd-9305-3e979d524e24.3.0.3")})]})});
            var Q83;
            Q83=makeQuery(id+"F5.boolean.opBoolean","COPY",FACE,{"derivedFrom":makeQuery(id+"F5.opExtrude","SWEPT_FACE",FACE,{"disambiguationData":[OSD([sQuery(id+"F4.wireOp",EDGE,"E17")])]})});
            var Q84;
            Q84=makeQuery(id+"F5.boolean.opBoolean","COPY",FACE,{"derivedFrom":makeQuery(id+"F5.opExtrude","SWEPT_FACE",FACE,{"disambiguationData":[OSD([sQuery(id+"F4.wireOp",EDGE,"f82c8603-6a34-46cd-9305-3e979d524e24.3.0.3")])]})});
            var Q85;
            Q85=makeQuery(id+"F5.boolean.opBoolean","COPY",FACE,{"derivedFrom":makeQuery(id+"F5.opExtrude","SWEPT_FACE",FACE,{"disambiguationData":[OSD([sQuery(id+"F4.wireOp",EDGE,"f82c8603-6a34-46cd-9305-3e979d524e24.3.0.1")])]})});
            var Q86;
            Q86=makeQuery(id+"F5.boolean.opBoolean","COPY",EDGE,{"derivedFrom":makeQuery(id+"F5.opExtrude","TWEAK_EDGE",EDGE,{"derivedFrom":[makeQuery(id+"F1.opExtrude","SWEPT_FACE",FACE,{"disambiguationData":[OSD([sQuery(id+"F0.wireOp",EDGE,"E4")])]}),makeQuery(id+"F4.imprint","IMPRINT",EDGE,{"derivedFrom":sQuery(id+"F4.wireOp",EDGE,"f82c8603-6a34-46cd-9305-3e979d524e24.3.0.1")})]})});
            var Q87;
            Q87=makeQuery(id+"F3.boolean.opBoolean","COPY",FACE,{"disambiguationData":[OD(0.0)],"derivedFrom":makeQuery(id+"F3.opExtrude","SWEPT_FACE",FACE,{"disambiguationData":[OSD([sQuery(id+"F2.wireOp",EDGE,"E11")])]})});
            var Q88;
            Q88=makeQuery(id+"F3.boolean.opBoolean","COPY",EDGE,{"derivedFrom":makeQuery(id+"F3.opExtrude","CAP_EDGE",EDGE,{"disambiguationData":[OSD([sQuery(id+"F2.wireOp",EDGE,"E16.7.0.1")])],"isStart":true})});
            var Q89;
            Q89=makeQuery(id+"F3.boolean.opBoolean","COPY",FACE,{"disambiguationData":[OD(0.0)],"derivedFrom":makeQuery(id+"F3.opExtrude","SWEPT_FACE",FACE,{"disambiguationData":[OSD([sQuery(id+"F2.wireOp",EDGE,"E10")])]})});
            var Q90;
            Q90=makeQuery(id+"F3.boolean.opBoolean","COPY",EDGE,{"derivedFrom":makeQuery(id+"F3.opExtrude","CAP_EDGE",EDGE,{"disambiguationData":[OSD([sQuery(id+"F2.wireOp",EDGE,"E16.1.0.1")])],"isStart":true})});
            var Q91;
            Q91=makeQuery(id+"F3.boolean.opBoolean","COPY",EDGE,{"derivedFrom":makeQuery(id+"F3.opExtrude","CAP_EDGE",EDGE,{"disambiguationData":[OSD([sQuery(id+"F2.wireOp",EDGE,"E14")])],"isStart":true})});
            var Q92;
            Q92=makeQuery(id+"F1.opExtrude","SWEPT_FACE",FACE,{"disambiguationData":[OSD([sQuery(id+"F0.wireOp",EDGE,"E5.right")])]});
            var Q93;
            Q93=makeQuery(id+"F3.boolean.opBoolean","COPY",EDGE,{"derivedFrom":makeQuery(id+"F3.opExtrude","CAP_EDGE",EDGE,{"disambiguationData":[OSD([sQuery(id+"F2.wireOp",EDGE,"E15")])],"isStart":true})});
            var Q94;
            Q94=makeQuery(id+"F1.opExtrude","SWEPT_FACE",FACE,{"disambiguationData":[OSD([sQuery(id+"F0.wireOp",EDGE,"E6.right")])]});
            var Q95;
            Q95=makeQuery(id+"F1.opExtrude","SWEPT_FACE",FACE,{"disambiguationData":[OSD([sQuery(id+"F0.wireOp",EDGE,"E0.rect.left"),sQuery(id+"F0.wireOp",EDGE,"E1.left"),sQuery(id+"F0.wireOp",EDGE,"E6.left")])]});
            var Q96;
            Q96=makeQuery(id+"F3.boolean.opBoolean","COPY",EDGE,{"derivedFrom":makeQuery(id+"F3.opExtrude","CAP_EDGE",EDGE,{"disambiguationData":[OSD([sQuery(id+"F2.wireOp",EDGE,"E11")])],"isStart":true})});
            var Q97;
            Q97=makeQuery(id+"F1.opExtrude","SWEPT_FACE",FACE,{"disambiguationData":[OSD([sQuery(id+"F0.wireOp",EDGE,"E0.rect.right"),sQuery(id+"F0.wireOp",EDGE,"E5.left")])]});
            var Q98;
            Q98=makeQuery(id+"F5.boolean.opBoolean","COPY",EDGE,{"derivedFrom":makeQuery(id+"F5.opExtrude","CAP_EDGE",EDGE,{"disambiguationData":[OSD([sQuery(id+"F4.wireOp",EDGE,"E18")])],"isStart":true})});
            var Q99;
            Q99=makeQuery(id+"F5.boolean.opBoolean","COPY",EDGE,{"derivedFrom":makeQuery(id+"F5.opExtrude","CAP_EDGE",EDGE,{"disambiguationData":[OSD([sQuery(id+"F4.wireOp",EDGE,"f82c8603-6a34-46cd-9305-3e979d524e24.4.0.1")])],"isStart":true})});
            var Q100;
            Q100=makeQuery(id+"F3.boolean.opBoolean","COPY",EDGE,{"derivedFrom":makeQuery(id+"F3.opExtrude","CAP_EDGE",EDGE,{"disambiguationData":[OSD([sQuery(id+"F2.wireOp",EDGE,"E16.2.0.3")])],"isStart":true})});
            var Q101;
            Q101=makeQuery(id+"F3.boolean.opBoolean","COPY",FACE,{"disambiguationData":[OD(0.0)],"derivedFrom":makeQuery(id+"F3.opExtrude","SWEPT_FACE",FACE,{"disambiguationData":[OSD([sQuery(id+"F2.wireOp",EDGE,"E16.1.0.0")])]})});
            var Q102;
            Q102=makeQuery(id+"F3.boolean.opBoolean","COPY",EDGE,{"derivedFrom":makeQuery(id+"F3.opExtrude","CAP_EDGE",EDGE,{"disambiguationData":[OSD([sQuery(id+"F2.wireOp",EDGE,"E16.2.0.1")])],"isStart":true})});
            var Q103;
            Q103=makeQuery(id+"F3.boolean.opBoolean","COPY",EDGE,{"derivedFrom":makeQuery(id+"F3.opExtrude","CAP_EDGE",EDGE,{"disambiguationData":[OSD([sQuery(id+"F2.wireOp",EDGE,"E16.1.0.3")])],"isStart":true})});
            var Q104;
            Q104=makeQuery(id+"F3.boolean.opBoolean","COPY",FACE,{"disambiguationData":[OD(0.0)],"derivedFrom":makeQuery(id+"F3.opExtrude","SWEPT_FACE",FACE,{"disambiguationData":[OSD([sQuery(id+"F2.wireOp",EDGE,"E14")])]})});
            var Q105;
            Q105=makeQuery(id+"F5.boolean.opBoolean","COPY",FACE,{"derivedFrom":makeQuery(id+"F5.opExtrude","SWEPT_FACE",FACE,{"disambiguationData":[OSD([sQuery(id+"F4.wireOp",EDGE,"f82c8603-6a34-46cd-9305-3e979d524e24.4.0.0")])]})});
            var Q106;
            Q106=makeQuery(id+"F1.opExtrude","SWEPT_FACE",FACE,{"disambiguationData":[OSD([sQuery(id+"F0.wireOp",EDGE,"E2")])]});
            var Q107;
            Q107=makeQuery(id+"F3.boolean.opBoolean","COPY",FACE,{"disambiguationData":[OD(0.0)],"derivedFrom":makeQuery(id+"F3.opExtrude","SWEPT_FACE",FACE,{"disambiguationData":[OSD([sQuery(id+"F2.wireOp",EDGE,"E16.1.0.1")])]})});
            var Q108;
            Q108=makeQuery(id+"F3.boolean.opBoolean","COPY",EDGE,{"derivedFrom":makeQuery(id+"F3.opExtrude","CAP_EDGE",EDGE,{"disambiguationData":[OSD([sQuery(id+"F2.wireOp",EDGE,"E16.3.0.3")])],"isStart":true})});
            var Q109;
            Q109=makeQuery(id+"F3.boolean.opBoolean","COPY",EDGE,{"derivedFrom":makeQuery(id+"F3.opExtrude","CAP_EDGE",EDGE,{"disambiguationData":[OSD([sQuery(id+"F2.wireOp",EDGE,"E16.3.0.2")])],"isStart":true})});
            var Q110;
            Q110=makeQuery(id+"F3.boolean.opBoolean","COPY",EDGE,{"derivedFrom":makeQuery(id+"F3.opExtrude","CAP_EDGE",EDGE,{"disambiguationData":[OSD([sQuery(id+"F2.wireOp",EDGE,"E16.3.0.1")])],"isStart":true})});
            var Q111;
            Q111=makeQuery(id+"F1.opExtrude","SWEPT_FACE",FACE,{"disambiguationData":[OSD([sQuery(id+"F0.wireOp",EDGE,"E0.rect.bottom")])]});
            var Q112;
            Q112=makeQuery(id+"F1.opExtrude","SWEPT_EDGE",EDGE,{"disambiguationData":[OSD([sQuery(id+"F0.wireOp",EDGE,"E0.rect.bottom"),sQuery(id+"F0.wireOp",EDGE,"E1.right")])]});
            var Q113;
            Q113=makeQuery(id+"F1.opExtrude","CAP_FACE",FACE,{"disambiguationData":[OSD([sQuery(id+"F0.wireOp",EDGE,"E0.rect.bottom"),sQuery(id+"F0.wireOp",EDGE,"E0.rect.top"),sQuery(id+"F0.wireOp",EDGE,"E0.rect.left"),sQuery(id+"F0.wireOp",EDGE,"E0.rect.right"),sQuery(id+"F0.wireOp",EDGE,"E1.top"),sQuery(id+"F0.wireOp",EDGE,"E1.left"),sQuery(id+"F0.wireOp",EDGE,"E1.right"),sQuery(id+"F0.wireOp",EDGE,"E2"),sQuery(id+"F0.wireOp",EDGE,"E3"),sQuery(id+"F0.wireOp",EDGE,"E4"),sQuery(id+"F0.wireOp",EDGE,"E5.top"),sQuery(id+"F0.wireOp",EDGE,"E5.left"),sQuery(id+"F0.wireOp",EDGE,"E5.right"),sQuery(id+"F0.wireOp",EDGE,"E6.top"),sQuery(id+"F0.wireOp",EDGE,"E6.left"),sQuery(id+"F0.wireOp",EDGE,"E6.right"),sQuery(id+"F0.wireOp",EDGE,"E7")])],"isStart":true});
            var Q114;
            Q114=makeQuery(id+"F1.opExtrude","CAP_FACE",FACE,{"disambiguationData":[OSD([sQuery(id+"F0.wireOp",EDGE,"E0.rect.bottom"),sQuery(id+"F0.wireOp",EDGE,"E0.rect.top"),sQuery(id+"F0.wireOp",EDGE,"E0.rect.left"),sQuery(id+"F0.wireOp",EDGE,"E0.rect.right"),sQuery(id+"F0.wireOp",EDGE,"E1.top"),sQuery(id+"F0.wireOp",EDGE,"E1.left"),sQuery(id+"F0.wireOp",EDGE,"E1.right"),sQuery(id+"F0.wireOp",EDGE,"E2"),sQuery(id+"F0.wireOp",EDGE,"E3"),sQuery(id+"F0.wireOp",EDGE,"E4"),sQuery(id+"F0.wireOp",EDGE,"E5.top"),sQuery(id+"F0.wireOp",EDGE,"E5.left"),sQuery(id+"F0.wireOp",EDGE,"E5.right"),sQuery(id+"F0.wireOp",EDGE,"E6.top"),sQuery(id+"F0.wireOp",EDGE,"E6.left"),sQuery(id+"F0.wireOp",EDGE,"E6.right"),sQuery(id+"F0.wireOp",EDGE,"E7")])],"isStart":false});
            var Q115;
            Q115=makeQuery(id+"F1.opExtrude","SWEPT_FACE",FACE,{"disambiguationData":[OSD([sQuery(id+"F0.wireOp",EDGE,"E0.rect.top")])]});
            var Q116;
            Q116=makeQuery(id+"F1.opExtrude","SWEPT_EDGE",EDGE,{"disambiguationData":[OSD([sQuery(id+"F0.wireOp",EDGE,"E0.rect.right"),sQuery(id+"F0.wireOp",EDGE,"E2")])]});
            var Q117;
            Q117=makeQuery(id+"F1.opExtrude","SWEPT_EDGE",EDGE,{"disambiguationData":[OSD([sQuery(id+"F0.wireOp",EDGE,"E1.top"),sQuery(id+"F0.wireOp",EDGE,"E1.left")])]});
            var Q118;
            Q118=makeQuery(id+"F1.opExtrude","SWEPT_EDGE",EDGE,{"disambiguationData":[OSD([sQuery(id+"F0.wireOp",EDGE,"E1.top"),sQuery(id+"F0.wireOp",EDGE,"E1.right")])]});
            var Q119;
            Q119=makeQuery(id+"F5.boolean.opBoolean","COPY",FACE,{"derivedFrom":makeQuery(id+"F5.opExtrude","SWEPT_FACE",FACE,{"disambiguationData":[OSD([sQuery(id+"F4.wireOp",EDGE,"f82c8603-6a34-46cd-9305-3e979d524e24.4.0.2")])]})});
            var Q120;
            Q120=makeQuery(id+"F1.opExtrude","SWEPT_FACE",FACE,{"disambiguationData":[OSD([sQuery(id+"F0.wireOp",EDGE,"E1.top")])]});
            var Q121;
            Q121=makeQuery(id+"F1.opExtrude","SWEPT_FACE",FACE,{"disambiguationData":[OSD([sQuery(id+"F0.wireOp",EDGE,"E1.right")])]});
            var Q122;
            Q122=makeQuery(id+"F1.opExtrude","SWEPT_EDGE",EDGE,{"disambiguationData":[OSD([sQuery(id+"F0.wireOp",EDGE,"E2"),sQuery(id+"F0.wireOp",EDGE,"E3")])]});
            var Q123;
            Q123=makeQuery(id+"F1.opExtrude","SWEPT_EDGE",EDGE,{"disambiguationData":[OSD([sQuery(id+"F0.wireOp",EDGE,"E3"),sQuery(id+"F0.wireOp",EDGE,"E4")])]});
            var Q124;
            Q124=makeQuery(id+"F1.opExtrude","SWEPT_FACE",FACE,{"disambiguationData":[OSD([sQuery(id+"F0.wireOp",EDGE,"E3")])]});
            var Q125;
            Q125=makeQuery(id+"F1.opExtrude","SWEPT_EDGE",EDGE,{"disambiguationData":[OSD([sQuery(id+"F0.wireOp",EDGE,"E5.top"),sQuery(id+"F0.wireOp",EDGE,"E5.left")])]});
            var Q126;
            Q126=makeQuery(id+"F1.opExtrude","SWEPT_FACE",FACE,{"disambiguationData":[OSD([sQuery(id+"F0.wireOp",EDGE,"E5.top")])]});
            var Q127;
            Q127=makeQuery(id+"F1.opExtrude","SWEPT_EDGE",EDGE,{"disambiguationData":[OSD([sQuery(id+"F0.wireOp",EDGE,"E6.top"),sQuery(id+"F0.wireOp",EDGE,"E7")])]});
            var Q128;
            Q128=makeQuery(id+"F5.boolean.opBoolean","COPY",EDGE,{"derivedFrom":makeQuery(id+"F5.opExtrude","CAP_EDGE",EDGE,{"disambiguationData":[OSD([sQuery(id+"F4.wireOp",EDGE,"f82c8603-6a34-46cd-9305-3e979d524e24.4.0.2")])],"isStart":true})});
            var Q129;
            Q129=makeQuery(id+"F5.boolean.opBoolean","COPY",EDGE,{"derivedFrom":makeQuery(id+"F5.opExtrude","CAP_EDGE",EDGE,{"disambiguationData":[OSD([sQuery(id+"F4.wireOp",EDGE,"E21")])],"isStart":true})});
            var Q130;
            Q130=makeQuery(id+"F1.opExtrude","SWEPT_FACE",FACE,{"disambiguationData":[OSD([sQuery(id+"F0.wireOp",EDGE,"E4")])]});
            var Q131;
            Q131=makeQuery(id+"F5.boolean.opBoolean","COPY",FACE,{"derivedFrom":makeQuery(id+"F5.opExtrude","SWEPT_FACE",FACE,{"disambiguationData":[OSD([sQuery(id+"F4.wireOp",EDGE,"f82c8603-6a34-46cd-9305-3e979d524e24.4.0.1")])]})});
            var Q132;
            Q132=makeQuery(id+"F1.opExtrude","SWEPT_FACE",FACE,{"disambiguationData":[OSD([sQuery(id+"F0.wireOp",EDGE,"E7")])]});
            var Q133;
            Q133=makeQuery(id+"F1.opExtrude","CAP_EDGE",EDGE,{"disambiguationData":[OSD([sQuery(id+"F0.wireOp",EDGE,"E0.rect.bottom")])],"isStart":true});
            var Q134;
            Q134=makeQuery(id+"F1.opExtrude","SWEPT_EDGE",EDGE,{"disambiguationData":[OSD([sQuery(id+"F0.wireOp",EDGE,"E6.right"),sQuery(id+"F0.wireOp",EDGE,"E7")])]});
            var Q135;
            Q135=makeQuery(id+"F1.opExtrude","CAP_EDGE",EDGE,{"disambiguationData":[OSD([sQuery(id+"F0.wireOp",EDGE,"E0.rect.bottom")])],"isStart":false});
            var Q136;
            Q136=makeQuery(id+"F5.boolean.opBoolean","COPY",EDGE,{"derivedFrom":makeQuery(id+"F5.opExtrude","CAP_EDGE",EDGE,{"disambiguationData":[OSD([sQuery(id+"F4.wireOp",EDGE,"f82c8603-6a34-46cd-9305-3e979d524e24.4.0.3")])],"isStart":true})});
            var Q137;
            Q137=makeQuery(id+"F5.boolean.opBoolean","COPY",EDGE,{"derivedFrom":makeQuery(id+"F5.opExtrude","CAP_EDGE",EDGE,{"disambiguationData":[OSD([sQuery(id+"F4.wireOp",EDGE,"E22")])],"isStart":true})});
            var Q138;
            Q138=makeQuery(id+"F5.boolean.opBoolean","COPY",EDGE,{"derivedFrom":makeQuery(id+"F5.opExtrude","TWEAK_EDGE",EDGE,{"derivedFrom":[makeQuery(id+"F1.opExtrude","SWEPT_FACE",FACE,{"disambiguationData":[OSD([sQuery(id+"F0.wireOp",EDGE,"E4")])]}),makeQuery(id+"F4.imprint","IMPRINT",EDGE,{"derivedFrom":sQuery(id+"F4.wireOp",EDGE,"f82c8603-6a34-46cd-9305-3e979d524e24.4.0.3")})]})});
            var Q139;
            Q139=makeQuery(id+"F5.boolean.opBoolean","COPY",FACE,{"derivedFrom":makeQuery(id+"F5.opExtrude","SWEPT_FACE",FACE,{"disambiguationData":[OSD([sQuery(id+"F4.wireOp",EDGE,"f82c8603-6a34-46cd-9305-3e979d524e24.4.0.3")])]})});
            var Q140;
            Q140=makeQuery(id+"F5.boolean.opBoolean","COPY",FACE,{"derivedFrom":makeQuery(id+"F5.opExtrude","SWEPT_FACE",FACE,{"disambiguationData":[OSD([sQuery(id+"F4.wireOp",EDGE,"f82c8603-6a34-46cd-9305-3e979d524e24.5.0.0")])]})});
            var Q141;
            Q141=makeQuery(id+"F5.boolean.opBoolean","COPY",EDGE,{"derivedFrom":makeQuery(id+"F5.opExtrude","CAP_EDGE",EDGE,{"disambiguationData":[OSD([sQuery(id+"F4.wireOp",EDGE,"f82c8603-6a34-46cd-9305-3e979d524e24.1.0.0")])],"isStart":true})});
            var Q142;
            Q142=makeQuery(id+"F5.boolean.opBoolean","COPY",FACE,{"derivedFrom":makeQuery(id+"F5.opExtrude","SWEPT_FACE",FACE,{"disambiguationData":[OSD([sQuery(id+"F4.wireOp",EDGE,"f82c8603-6a34-46cd-9305-3e979d524e24.5.0.1")])]})});
            var Q143;
            Q143=makeQuery(id+"F5.boolean.opBoolean","COPY",EDGE,{"derivedFrom":makeQuery(id+"F5.opExtrude","TWEAK_EDGE",EDGE,{"derivedFrom":[makeQuery(id+"F1.opExtrude","SWEPT_FACE",FACE,{"disambiguationData":[OSD([sQuery(id+"F0.wireOp",EDGE,"E4")])]}),makeQuery(id+"F4.imprint","IMPRINT",EDGE,{"derivedFrom":sQuery(id+"F4.wireOp",EDGE,"f82c8603-6a34-46cd-9305-3e979d524e24.5.0.1")})]})});
            var Q144;
            Q144=makeQuery(id+"F5.boolean.opBoolean","COPY",EDGE,{"derivedFrom":makeQuery(id+"F5.opExtrude","CAP_EDGE",EDGE,{"disambiguationData":[OSD([sQuery(id+"F4.wireOp",EDGE,"f82c8603-6a34-46cd-9305-3e979d524e24.1.0.1")])],"isStart":true})});
            var Q145;
            Q145=makeQuery(id+"F5.boolean.opBoolean","COPY",EDGE,{"derivedFrom":makeQuery(id+"F5.opExtrude","CAP_EDGE",EDGE,{"disambiguationData":[OSD([sQuery(id+"F4.wireOp",EDGE,"f82c8603-6a34-46cd-9305-3e979d524e24.1.0.2")])],"isStart":true})});
            var Q146;
            Q146=makeQuery(id+"F5.boolean.opBoolean","COPY",EDGE,{"derivedFrom":makeQuery(id+"F5.opExtrude","CAP_EDGE",EDGE,{"disambiguationData":[OSD([sQuery(id+"F4.wireOp",EDGE,"f82c8603-6a34-46cd-9305-3e979d524e24.5.0.2")])],"isStart":true})});
            var Q147;
            Q147=makeQuery(id+"F5.boolean.opBoolean","COPY",EDGE,{"derivedFrom":makeQuery(id+"F5.opExtrude","SWEPT_EDGE",EDGE,{"disambiguationData":[OSD([sQuery(id+"F4.wireOp",EDGE,"f82c8603-6a34-46cd-9305-3e979d524e24.2.0.1"),sQuery(id+"F4.wireOp",EDGE,"f82c8603-6a34-46cd-9305-3e979d524e24.2.0.3")])]})});
            var Q148;
            Q148=makeQuery(id+"F5.boolean.opBoolean","COPY",EDGE,{"derivedFrom":makeQuery(id+"F5.opExtrude","SWEPT_EDGE",EDGE,{"disambiguationData":[OSD([sQuery(id+"F4.wireOp",EDGE,"f82c8603-6a34-46cd-9305-3e979d524e24.6.0.1"),sQuery(id+"F4.wireOp",EDGE,"f82c8603-6a34-46cd-9305-3e979d524e24.6.0.3")])]})});
            var Q149;
            Q149=makeQuery(id+"F5.boolean.opBoolean","COPY",EDGE,{"derivedFrom":makeQuery(id+"F5.opExtrude","TWEAK_EDGE",EDGE,{"derivedFrom":[makeQuery(id+"F1.opExtrude","SWEPT_FACE",FACE,{"disambiguationData":[OSD([sQuery(id+"F0.wireOp",EDGE,"E4")])]}),makeQuery(id+"F4.imprint","IMPRINT",EDGE,{"derivedFrom":sQuery(id+"F4.wireOp",EDGE,"f82c8603-6a34-46cd-9305-3e979d524e24.6.0.2")})]})});
            var Q150;
            Q150=makeQuery(id+"F5.boolean.opBoolean","COPY",EDGE,{"derivedFrom":makeQuery(id+"F5.opExtrude","CAP_EDGE",EDGE,{"disambiguationData":[OSD([sQuery(id+"F4.wireOp",EDGE,"f82c8603-6a34-46cd-9305-3e979d524e24.2.0.0")])],"isStart":true})});
            var Q151;
            Q151=makeQuery(id+"F5.boolean.opBoolean","COPY",EDGE,{"derivedFrom":makeQuery(id+"F5.opExtrude","SWEPT_EDGE",EDGE,{"disambiguationData":[OSD([sQuery(id+"F4.wireOp",EDGE,"f82c8603-6a34-46cd-9305-3e979d524e24.2.0.0"),sQuery(id+"F4.wireOp",EDGE,"f82c8603-6a34-46cd-9305-3e979d524e24.2.0.2")])]})});
            var Q152;
            Q152=makeQuery(id+"F5.boolean.opBoolean","COPY",EDGE,{"derivedFrom":makeQuery(id+"F5.opExtrude","SWEPT_EDGE",EDGE,{"disambiguationData":[OSD([sQuery(id+"F4.wireOp",EDGE,"f82c8603-6a34-46cd-9305-3e979d524e24.6.0.0"),sQuery(id+"F4.wireOp",EDGE,"f82c8603-6a34-46cd-9305-3e979d524e24.6.0.2")])]})});
            var Q153;
            Q153=makeQuery(id+"F3.boolean.opBoolean","INTERSECT",EDGE,{"derivedFrom":[makeQuery(id+"F1.opExtrude","SWEPT_FACE",FACE,{"disambiguationData":[OSD([sQuery(id+"F0.wireOp",EDGE,"E5.right")])]}),makeQuery(id+"F3.opExtrude","SWEPT_FACE",FACE,{"disambiguationData":[OSD([sQuery(id+"F2.wireOp",EDGE,"E16.1.0.2")])]})]});
            var Q154;
            Q154=makeQuery(id+"F3.boolean.opBoolean","INTERSECT",EDGE,{"derivedFrom":[makeQuery(id+"F1.opExtrude","SWEPT_FACE",FACE,{"disambiguationData":[OSD([sQuery(id+"F0.wireOp",EDGE,"E5.right")])]}),makeQuery(id+"F3.opExtrude","SWEPT_FACE",FACE,{"disambiguationData":[OSD([sQuery(id+"F2.wireOp",EDGE,"E16.5.0.2")])]})]});
            var Q155;
            Q155=makeQuery(id+"F5.boolean.opBoolean","COPY",EDGE,{"derivedFrom":makeQuery(id+"F5.opExtrude","SWEPT_EDGE",EDGE,{"disambiguationData":[OSD([sQuery(id+"F4.wireOp",EDGE,"f82c8603-6a34-46cd-9305-3e979d524e24.6.0.0"),sQuery(id+"F4.wireOp",EDGE,"f82c8603-6a34-46cd-9305-3e979d524e24.6.0.3")])]})});
            var Q156;
            Q156=makeQuery(id+"F3.boolean.opBoolean","COPY",EDGE,{"disambiguationData":[OD(0.0)],"derivedFrom":makeQuery(id+"F3.opExtrude","SWEPT_EDGE",EDGE,{"disambiguationData":[OSD([sQuery(id+"F2.wireOp",EDGE,"E16.6.0.2"),sQuery(id+"F2.wireOp",EDGE,"E16.6.0.3")])]})});
            var Q157;
            Q157=makeQuery(id+"F5.boolean.opBoolean","COPY",EDGE,{"derivedFrom":makeQuery(id+"F5.opExtrude","SWEPT_EDGE",EDGE,{"disambiguationData":[OSD([sQuery(id+"F4.wireOp",EDGE,"f82c8603-6a34-46cd-9305-3e979d524e24.2.0.0"),sQuery(id+"F4.wireOp",EDGE,"f82c8603-6a34-46cd-9305-3e979d524e24.2.0.3")])]})});
            var Q158;
            Q158=makeQuery(id+"F3.boolean.opBoolean","COPY",EDGE,{"disambiguationData":[OD(0.0)],"derivedFrom":makeQuery(id+"F3.opExtrude","SWEPT_EDGE",EDGE,{"disambiguationData":[OSD([sQuery(id+"F2.wireOp",EDGE,"E16.4.0.2"),sQuery(id+"F2.wireOp",EDGE,"E16.4.0.3")])]})});
            var Q159;
            Q159=makeQuery(id+"F5.boolean.opBoolean","COPY",EDGE,{"derivedFrom":makeQuery(id+"F5.opExtrude","CAP_EDGE",EDGE,{"disambiguationData":[OSD([sQuery(id+"F4.wireOp",EDGE,"f82c8603-6a34-46cd-9305-3e979d524e24.6.0.1")])],"isStart":true})});
            var Q160;
            Q160=makeQuery(id+"F3.boolean.opBoolean","COPY",EDGE,{"derivedFrom":makeQuery(id+"F3.opExtrude","CAP_EDGE",EDGE,{"disambiguationData":[OSD([sQuery(id+"F2.wireOp",EDGE,"E16.5.0.2")])],"isStart":true})});
            var Q161;
            Q161=makeQuery(id+"F5.boolean.opBoolean","COPY",EDGE,{"derivedFrom":makeQuery(id+"F5.opExtrude","TWEAK_EDGE",EDGE,{"derivedFrom":[makeQuery(id+"F1.opExtrude","SWEPT_FACE",FACE,{"disambiguationData":[OSD([sQuery(id+"F0.wireOp",EDGE,"E4")])]}),makeQuery(id+"F4.imprint","IMPRINT",EDGE,{"derivedFrom":sQuery(id+"F4.wireOp",EDGE,"f82c8603-6a34-46cd-9305-3e979d524e24.6.0.1")})]})});
            var Q162;
            Q162=makeQuery(id+"F3.boolean.opBoolean","COPY",EDGE,{"disambiguationData":[OD(0.0)],"derivedFrom":makeQuery(id+"F3.opExtrude","SWEPT_EDGE",EDGE,{"disambiguationData":[OSD([sQuery(id+"F2.wireOp",EDGE,"E16.2.0.2"),sQuery(id+"F2.wireOp",EDGE,"E16.2.0.3")])]})});
            var Q163;
            Q163=makeQuery(id+"F3.boolean.opBoolean","COPY",EDGE,{"disambiguationData":[OD(0.0)],"derivedFrom":makeQuery(id+"F3.opExtrude","SWEPT_EDGE",EDGE,{"disambiguationData":[OSD([sQuery(id+"F2.wireOp",EDGE,"E11"),sQuery(id+"F2.wireOp",EDGE,"E14")])]})});
            var Q164;
            Q164=makeQuery(id+"F3.boolean.opBoolean","INTERSECT",EDGE,{"derivedFrom":[makeQuery(id+"F1.opExtrude","SWEPT_FACE",FACE,{"disambiguationData":[OSD([sQuery(id+"F0.wireOp",EDGE,"E6.right")])]}),makeQuery(id+"F3.opExtrude","SWEPT_FACE",FACE,{"disambiguationData":[OSD([sQuery(id+"F2.wireOp",EDGE,"E16.1.0.3")])]})]});
            var Q165;
            Q165=makeQuery(id+"F3.boolean.opBoolean","INTERSECT",EDGE,{"derivedFrom":[makeQuery(id+"F1.opExtrude","SWEPT_FACE",FACE,{"disambiguationData":[OSD([sQuery(id+"F0.wireOp",EDGE,"E6.right")])]}),makeQuery(id+"F3.opExtrude","SWEPT_FACE",FACE,{"disambiguationData":[OSD([sQuery(id+"F2.wireOp",EDGE,"E16.5.0.3")])]})]});
            var Q166;
            Q166=makeQuery(id+"F3.boolean.opBoolean","INTERSECT",EDGE,{"derivedFrom":[makeQuery(id+"F1.opExtrude","SWEPT_FACE",FACE,{"disambiguationData":[OSD([sQuery(id+"F0.wireOp",EDGE,"E5.right")])]}),makeQuery(id+"F3.opExtrude","SWEPT_FACE",FACE,{"disambiguationData":[OSD([sQuery(id+"F2.wireOp",EDGE,"E16.1.0.3")])]})]});
            var Q167;
            Q167=makeQuery(id+"F3.boolean.opBoolean","INTERSECT",EDGE,{"derivedFrom":[makeQuery(id+"F1.opExtrude","SWEPT_FACE",FACE,{"disambiguationData":[OSD([sQuery(id+"F0.wireOp",EDGE,"E0.rect.left"),sQuery(id+"F0.wireOp",EDGE,"E1.left"),sQuery(id+"F0.wireOp",EDGE,"E6.left")])]}),makeQuery(id+"F3.opExtrude","SWEPT_FACE",FACE,{"disambiguationData":[OSD([sQuery(id+"F2.wireOp",EDGE,"E16.1.0.3")])]})]});
            var Q168;
            Q168=makeQuery(id+"F3.boolean.opBoolean","INTERSECT",EDGE,{"derivedFrom":[makeQuery(id+"F1.opExtrude","SWEPT_FACE",FACE,{"disambiguationData":[OSD([sQuery(id+"F0.wireOp",EDGE,"E0.rect.left"),sQuery(id+"F0.wireOp",EDGE,"E1.left"),sQuery(id+"F0.wireOp",EDGE,"E6.left")])]}),makeQuery(id+"F3.opExtrude","SWEPT_FACE",FACE,{"disambiguationData":[OSD([sQuery(id+"F2.wireOp",EDGE,"E16.5.0.3")])]})]});
            var Q169;
            Q169=makeQuery(id+"F3.boolean.opBoolean","COPY",FACE,{"disambiguationData":[OD(1.0)],"derivedFrom":makeQuery(id+"F3.opExtrude","SWEPT_FACE",FACE,{"disambiguationData":[OSD([sQuery(id+"F2.wireOp",EDGE,"E16.4.0.1")])]})});
            var Q170;
            Q170=makeQuery(id+"F3.boolean.opBoolean","COPY",FACE,{"disambiguationData":[OD(1.0)],"derivedFrom":makeQuery(id+"F3.opExtrude","SWEPT_FACE",FACE,{"disambiguationData":[OSD([sQuery(id+"F2.wireOp",EDGE,"E16.2.0.1")])]})});
            var Q171;
            Q171=makeQuery(id+"F3.boolean.opBoolean","COPY",FACE,{"disambiguationData":[OD(1.0)],"derivedFrom":makeQuery(id+"F3.opExtrude","SWEPT_FACE",FACE,{"disambiguationData":[OSD([sQuery(id+"F2.wireOp",EDGE,"E16.6.0.1")])]})});
            var Q172;
            Q172=makeQuery(id+"F5.boolean.opBoolean","COPY",EDGE,{"derivedFrom":makeQuery(id+"F5.opExtrude","SWEPT_EDGE",EDGE,{"disambiguationData":[OSD([sQuery(id+"F4.wireOp",EDGE,"f82c8603-6a34-46cd-9305-3e979d524e24.5.0.1"),sQuery(id+"F4.wireOp",EDGE,"f82c8603-6a34-46cd-9305-3e979d524e24.5.0.2")])]})});
            var Q173;
            Q173=makeQuery(id+"F5.boolean.opBoolean","COPY",EDGE,{"derivedFrom":makeQuery(id+"F5.opExtrude","SWEPT_EDGE",EDGE,{"disambiguationData":[OSD([sQuery(id+"F4.wireOp",EDGE,"f82c8603-6a34-46cd-9305-3e979d524e24.1.0.1"),sQuery(id+"F4.wireOp",EDGE,"f82c8603-6a34-46cd-9305-3e979d524e24.1.0.2")])]})});
            var Q174;
            Q174=makeQuery(id+"F5.boolean.opBoolean","COPY",EDGE,{"derivedFrom":makeQuery(id+"F5.opExtrude","TWEAK_EDGE",EDGE,{"derivedFrom":[makeQuery(id+"F1.opExtrude","SWEPT_FACE",FACE,{"disambiguationData":[OSD([sQuery(id+"F0.wireOp",EDGE,"E4")])]}),makeQuery(id+"F4.imprint","IMPRINT",EDGE,{"derivedFrom":sQuery(id+"F4.wireOp",EDGE,"f82c8603-6a34-46cd-9305-3e979d524e24.6.0.0")})]})});
            var Q175;
            Q175=makeQuery(id+"F3.boolean.opBoolean","COPY",EDGE,{"disambiguationData":[OD(0.0)],"derivedFrom":makeQuery(id+"F3.opExtrude","SWEPT_EDGE",EDGE,{"disambiguationData":[OSD([sQuery(id+"F2.wireOp",EDGE,"E16.3.0.0"),sQuery(id+"F2.wireOp",EDGE,"E16.3.0.3")])]})});
            var Q176;
            Q176=makeQuery(id+"F3.boolean.opBoolean","COPY",EDGE,{"disambiguationData":[OD(0.0)],"derivedFrom":makeQuery(id+"F3.opExtrude","SWEPT_EDGE",EDGE,{"disambiguationData":[OSD([sQuery(id+"F2.wireOp",EDGE,"E16.7.0.0"),sQuery(id+"F2.wireOp",EDGE,"E16.7.0.3")])]})});
            var Q177;
            Q177=makeQuery(id+"F3.boolean.opBoolean","COPY",EDGE,{"disambiguationData":[OD(0.0)],"derivedFrom":makeQuery(id+"F3.opExtrude","SWEPT_EDGE",EDGE,{"disambiguationData":[OSD([sQuery(id+"F2.wireOp",EDGE,"E16.5.0.0"),sQuery(id+"F2.wireOp",EDGE,"E16.5.0.3")])]})});
            var Q178;
            Q178=makeQuery(id+"F3.boolean.opBoolean","COPY",EDGE,{"derivedFrom":makeQuery(id+"F3.opExtrude","CAP_EDGE",EDGE,{"disambiguationData":[OSD([sQuery(id+"F2.wireOp",EDGE,"E16.6.0.0")])],"isStart":true})});
            var Q179;
            Q179=makeQuery(id+"F3.boolean.opBoolean","COPY",FACE,{"disambiguationData":[OD(0.0)],"derivedFrom":makeQuery(id+"F3.opExtrude","SWEPT_FACE",FACE,{"disambiguationData":[OSD([sQuery(id+"F2.wireOp",EDGE,"E16.6.0.1")])]})});
            var Q180;
            Q180=makeQuery(id+"F3.boolean.opBoolean","COPY",FACE,{"disambiguationData":[OD(1.0)],"derivedFrom":makeQuery(id+"F3.opExtrude","SWEPT_FACE",FACE,{"disambiguationData":[OSD([sQuery(id+"F2.wireOp",EDGE,"E16.6.0.2")])]})});
            var Q181;
            Q181=makeQuery(id+"F3.boolean.opBoolean","COPY",FACE,{"disambiguationData":[OD(1.0)],"derivedFrom":makeQuery(id+"F3.opExtrude","SWEPT_FACE",FACE,{"disambiguationData":[OSD([sQuery(id+"F2.wireOp",EDGE,"E16.4.0.2")])]})});
            var Q182;
            Q182=makeQuery(id+"F3.boolean.opBoolean","COPY",FACE,{"disambiguationData":[OD(1.0)],"derivedFrom":makeQuery(id+"F3.opExtrude","SWEPT_FACE",FACE,{"disambiguationData":[OSD([sQuery(id+"F2.wireOp",EDGE,"E16.2.0.2")])]})});
            var Q183;
            Q183=makeQuery(id+"F3.boolean.opBoolean","INTERSECT",EDGE,{"derivedFrom":[makeQuery(id+"F1.opExtrude","SWEPT_FACE",FACE,{"disambiguationData":[OSD([sQuery(id+"F0.wireOp",EDGE,"E5.right")])]}),makeQuery(id+"F3.opExtrude","SWEPT_FACE",FACE,{"disambiguationData":[OSD([sQuery(id+"F2.wireOp",EDGE,"E16.6.0.2")])]})]});
            var Q184;
            Q184=makeQuery(id+"F3.boolean.opBoolean","INTERSECT",EDGE,{"derivedFrom":[makeQuery(id+"F1.opExtrude","SWEPT_FACE",FACE,{"disambiguationData":[OSD([sQuery(id+"F0.wireOp",EDGE,"E0.rect.left"),sQuery(id+"F0.wireOp",EDGE,"E1.left"),sQuery(id+"F0.wireOp",EDGE,"E6.left")])]}),makeQuery(id+"F3.opExtrude","SWEPT_FACE",FACE,{"disambiguationData":[OSD([sQuery(id+"F2.wireOp",EDGE,"E16.6.0.2")])]})]});
            var Q185;
            Q185=makeQuery(id+"F3.boolean.opBoolean","INTERSECT",EDGE,{"derivedFrom":[makeQuery(id+"F1.opExtrude","SWEPT_FACE",FACE,{"disambiguationData":[OSD([sQuery(id+"F0.wireOp",EDGE,"E0.rect.left"),sQuery(id+"F0.wireOp",EDGE,"E1.left"),sQuery(id+"F0.wireOp",EDGE,"E6.left")])]}),makeQuery(id+"F3.opExtrude","SWEPT_FACE",FACE,{"disambiguationData":[OSD([sQuery(id+"F2.wireOp",EDGE,"E16.2.0.2")])]})]});
            var Q186;
            Q186=makeQuery(id+"F3.boolean.opBoolean","INTERSECT",EDGE,{"derivedFrom":[makeQuery(id+"F1.opExtrude","SWEPT_FACE",FACE,{"disambiguationData":[OSD([sQuery(id+"F0.wireOp",EDGE,"E6.right")])]}),makeQuery(id+"F3.opExtrude","SWEPT_FACE",FACE,{"disambiguationData":[OSD([sQuery(id+"F2.wireOp",EDGE,"E16.6.0.2")])]})]});
            var Q187;
            Q187=makeQuery(id+"F3.boolean.opBoolean","INTERSECT",EDGE,{"derivedFrom":[makeQuery(id+"F1.opExtrude","SWEPT_FACE",FACE,{"disambiguationData":[OSD([sQuery(id+"F0.wireOp",EDGE,"E6.right")])]}),makeQuery(id+"F3.opExtrude","SWEPT_FACE",FACE,{"disambiguationData":[OSD([sQuery(id+"F2.wireOp",EDGE,"E16.2.0.2")])]})]});
            var Q188;
            Q188=makeQuery(id+"F3.boolean.opBoolean","COPY",EDGE,{"derivedFrom":makeQuery(id+"F3.opExtrude","CAP_EDGE",EDGE,{"disambiguationData":[OSD([sQuery(id+"F2.wireOp",EDGE,"E16.6.0.2")])],"isStart":true})});
            var Q189;
            Q189=makeQuery(id+"F3.boolean.opBoolean","COPY",EDGE,{"disambiguationData":[OD(0.0)],"derivedFrom":makeQuery(id+"F3.opExtrude","SWEPT_EDGE",EDGE,{"disambiguationData":[OSD([sQuery(id+"F2.wireOp",EDGE,"E16.5.0.0"),sQuery(id+"F2.wireOp",EDGE,"E16.5.0.1")])]})});
            var Q190;
            Q190=makeQuery(id+"F3.boolean.opBoolean","COPY",EDGE,{"disambiguationData":[OD(0.0)],"derivedFrom":makeQuery(id+"F3.opExtrude","SWEPT_EDGE",EDGE,{"disambiguationData":[OSD([sQuery(id+"F2.wireOp",EDGE,"E16.1.0.0"),sQuery(id+"F2.wireOp",EDGE,"E16.1.0.1")])]})});
            var Q191;
            Q191=makeQuery(id+"F3.boolean.opBoolean","INTERSECT",EDGE,{"derivedFrom":[makeQuery(id+"F1.opExtrude","SWEPT_FACE",FACE,{"disambiguationData":[OSD([sQuery(id+"F0.wireOp",EDGE,"E0.rect.left"),sQuery(id+"F0.wireOp",EDGE,"E1.left"),sQuery(id+"F0.wireOp",EDGE,"E6.left")])]}),makeQuery(id+"F3.opExtrude","SWEPT_FACE",FACE,{"disambiguationData":[OSD([sQuery(id+"F2.wireOp",EDGE,"E16.6.0.0")])]})]});
            var Q192;
            Q192=makeQuery(id+"F3.boolean.opBoolean","INTERSECT",EDGE,{"derivedFrom":[makeQuery(id+"F1.opExtrude","SWEPT_FACE",FACE,{"disambiguationData":[OSD([sQuery(id+"F0.wireOp",EDGE,"E0.rect.left"),sQuery(id+"F0.wireOp",EDGE,"E1.left"),sQuery(id+"F0.wireOp",EDGE,"E6.left")])]}),makeQuery(id+"F3.opExtrude","SWEPT_FACE",FACE,{"disambiguationData":[OSD([sQuery(id+"F2.wireOp",EDGE,"E16.2.0.0")])]})]});
            var Q193;
            Q193=makeQuery(id+"F3.boolean.opBoolean","INTERSECT",EDGE,{"derivedFrom":[makeQuery(id+"F1.opExtrude","SWEPT_FACE",FACE,{"disambiguationData":[OSD([sQuery(id+"F0.wireOp",EDGE,"E5.right")])]}),makeQuery(id+"F3.opExtrude","SWEPT_FACE",FACE,{"disambiguationData":[OSD([sQuery(id+"F2.wireOp",EDGE,"E16.6.0.0")])]})]});
            var Q194;
            Q194=makeQuery(id+"F3.boolean.opBoolean","INTERSECT",EDGE,{"derivedFrom":[makeQuery(id+"F1.opExtrude","SWEPT_FACE",FACE,{"disambiguationData":[OSD([sQuery(id+"F0.wireOp",EDGE,"E5.right")])]}),makeQuery(id+"F3.opExtrude","SWEPT_FACE",FACE,{"disambiguationData":[OSD([sQuery(id+"F2.wireOp",EDGE,"E16.2.0.0")])]})]});
            var Q195;
            Q195=makeQuery(id+"F3.boolean.opBoolean","COPY",EDGE,{"disambiguationData":[OD(1.0)],"derivedFrom":makeQuery(id+"F3.opExtrude","SWEPT_EDGE",EDGE,{"disambiguationData":[OSD([sQuery(id+"F2.wireOp",EDGE,"E16.7.0.0"),sQuery(id+"F2.wireOp",EDGE,"E16.7.0.3")])]})});
            var Q196;
            Q196=makeQuery(id+"F3.boolean.opBoolean","INTERSECT",EDGE,{"derivedFrom":[makeQuery(id+"F1.opExtrude","SWEPT_FACE",FACE,{"disambiguationData":[OSD([sQuery(id+"F0.wireOp",EDGE,"E5.right")])]}),makeQuery(id+"F3.opExtrude","SWEPT_FACE",FACE,{"disambiguationData":[OSD([sQuery(id+"F2.wireOp",EDGE,"E16.6.0.1")])]})]});
            var Q197;
            Q197=makeQuery(id+"F3.boolean.opBoolean","COPY",FACE,{"disambiguationData":[OD(1.0)],"derivedFrom":makeQuery(id+"F3.opExtrude","SWEPT_FACE",FACE,{"disambiguationData":[OSD([sQuery(id+"F2.wireOp",EDGE,"E16.2.0.3")])]})});
            var Q198;
            Q198=makeQuery(id+"F3.boolean.opBoolean","COPY",FACE,{"disambiguationData":[OD(1.0)],"derivedFrom":makeQuery(id+"F3.opExtrude","SWEPT_FACE",FACE,{"disambiguationData":[OSD([sQuery(id+"F2.wireOp",EDGE,"E16.6.0.3")])]})});
            var Q199;
            Q199=makeQuery(id+"F3.boolean.opBoolean","COPY",EDGE,{"derivedFrom":makeQuery(id+"F3.opExtrude","CAP_EDGE",EDGE,{"disambiguationData":[OSD([sQuery(id+"F2.wireOp",EDGE,"E16.7.0.0")])],"isStart":true})});
            var Q200;
            Q200=makeQuery(id+"F3.boolean.opBoolean","COPY",EDGE,{"disambiguationData":[OD(0.0)],"derivedFrom":makeQuery(id+"F3.opExtrude","SWEPT_EDGE",EDGE,{"disambiguationData":[OSD([sQuery(id+"F2.wireOp",EDGE,"E16.1.0.1"),sQuery(id+"F2.wireOp",EDGE,"E16.1.0.2")])]})});
            var Q201;
            Q201=makeQuery(id+"F3.boolean.opBoolean","COPY",EDGE,{"disambiguationData":[OD(0.0)],"derivedFrom":makeQuery(id+"F3.opExtrude","SWEPT_EDGE",EDGE,{"disambiguationData":[OSD([sQuery(id+"F2.wireOp",EDGE,"E16.3.0.1"),sQuery(id+"F2.wireOp",EDGE,"E16.3.0.2")])]})});
            var Q202;
            Q202=makeQuery(id+"F3.boolean.opBoolean","COPY",EDGE,{"disambiguationData":[OD(0.0)],"derivedFrom":makeQuery(id+"F3.opExtrude","SWEPT_EDGE",EDGE,{"disambiguationData":[OSD([sQuery(id+"F2.wireOp",EDGE,"E16.5.0.1"),sQuery(id+"F2.wireOp",EDGE,"E16.5.0.2")])]})});
            var Q203;
            Q203=makeQuery(id+"F3.boolean.opBoolean","COPY",EDGE,{"disambiguationData":[OD(0.0)],"derivedFrom":makeQuery(id+"F3.opExtrude","SWEPT_EDGE",EDGE,{"disambiguationData":[OSD([sQuery(id+"F2.wireOp",EDGE,"E16.7.0.1"),sQuery(id+"F2.wireOp",EDGE,"E16.7.0.2")])]})});
            var Q204;
            Q204=makeQuery(id+"F1.opExtrude","CAP_EDGE",EDGE,{"disambiguationData":[OSD([sQuery(id+"F0.wireOp",EDGE,"E2")])],"isStart":false});
            var Q205;
            Q205=makeQuery(id+"F3.boolean.opBoolean","INTERSECT",EDGE,{"derivedFrom":[makeQuery(id+"F1.opExtrude","SWEPT_FACE",FACE,{"disambiguationData":[OSD([sQuery(id+"F0.wireOp",EDGE,"E0.rect.left"),sQuery(id+"F0.wireOp",EDGE,"E1.left"),sQuery(id+"F0.wireOp",EDGE,"E6.left")])]}),makeQuery(id+"F3.opExtrude","SWEPT_FACE",FACE,{"disambiguationData":[OSD([sQuery(id+"F2.wireOp",EDGE,"E16.3.0.0")])]})]});
            var Q206;
            Q206=makeQuery(id+"F3.boolean.opBoolean","INTERSECT",EDGE,{"derivedFrom":[makeQuery(id+"F1.opExtrude","SWEPT_FACE",FACE,{"disambiguationData":[OSD([sQuery(id+"F0.wireOp",EDGE,"E5.right")])]}),makeQuery(id+"F3.opExtrude","SWEPT_FACE",FACE,{"disambiguationData":[OSD([sQuery(id+"F2.wireOp",EDGE,"E16.7.0.0")])]})]});
            var Q207;
            Q207=makeQuery(id+"F3.boolean.opBoolean","INTERSECT",EDGE,{"derivedFrom":[makeQuery(id+"F1.opExtrude","SWEPT_FACE",FACE,{"disambiguationData":[OSD([sQuery(id+"F0.wireOp",EDGE,"E5.right")])]}),makeQuery(id+"F3.opExtrude","SWEPT_FACE",FACE,{"disambiguationData":[OSD([sQuery(id+"F2.wireOp",EDGE,"E16.3.0.0")])]})]});
            var Q208;
            Q208=makeQuery(id+"F3.boolean.opBoolean","INTERSECT",EDGE,{"derivedFrom":[makeQuery(id+"F1.opExtrude","SWEPT_FACE",FACE,{"disambiguationData":[OSD([sQuery(id+"F0.wireOp",EDGE,"E6.right")])]}),makeQuery(id+"F3.opExtrude","SWEPT_FACE",FACE,{"disambiguationData":[OSD([sQuery(id+"F2.wireOp",EDGE,"E16.7.0.0")])]})]});
            var Q209;
            Q209=makeQuery(id+"F5.boolean.opBoolean","COPY",EDGE,{"derivedFrom":makeQuery(id+"F5.opExtrude","CAP_EDGE",EDGE,{"disambiguationData":[OSD([sQuery(id+"F4.wireOp",EDGE,"f82c8603-6a34-46cd-9305-3e979d524e24.3.0.0")])],"isStart":true})});
            var Q210;
            Q210=makeQuery(id+"F5.boolean.opBoolean","COPY",EDGE,{"derivedFrom":makeQuery(id+"F5.opExtrude","SWEPT_EDGE",EDGE,{"disambiguationData":[OSD([sQuery(id+"F4.wireOp",EDGE,"f82c8603-6a34-46cd-9305-3e979d524e24.3.0.0"),sQuery(id+"F4.wireOp",EDGE,"f82c8603-6a34-46cd-9305-3e979d524e24.3.0.2")])]})});
            var Q211;
            Q211=makeQuery(id+"F5.boolean.opBoolean","COPY",EDGE,{"derivedFrom":makeQuery(id+"F5.opExtrude","SWEPT_EDGE",EDGE,{"disambiguationData":[OSD([sQuery(id+"F4.wireOp",EDGE,"f82c8603-6a34-46cd-9305-3e979d524e24.7.0.0"),sQuery(id+"F4.wireOp",EDGE,"f82c8603-6a34-46cd-9305-3e979d524e24.7.0.2")])]})});
            var Q212;
            Q212=makeQuery(id+"F5.boolean.opBoolean","COPY",EDGE,{"derivedFrom":makeQuery(id+"F5.opExtrude","TWEAK_EDGE",EDGE,{"derivedFrom":[makeQuery(id+"F1.opExtrude","SWEPT_FACE",FACE,{"disambiguationData":[OSD([sQuery(id+"F0.wireOp",EDGE,"E4")])]}),makeQuery(id+"F4.imprint","IMPRINT",EDGE,{"derivedFrom":sQuery(id+"F4.wireOp",EDGE,"f82c8603-6a34-46cd-9305-3e979d524e24.7.0.0")})]})});
            var Q213;
            Q213=makeQuery(id+"F5.boolean.opBoolean","COPY",FACE,{"derivedFrom":makeQuery(id+"F5.opExtrude","SWEPT_FACE",FACE,{"disambiguationData":[OSD([sQuery(id+"F4.wireOp",EDGE,"f82c8603-6a34-46cd-9305-3e979d524e24.6.0.2")])]})});
            var Q214;
            Q214=makeQuery(id+"F3.boolean.opBoolean","COPY",FACE,{"disambiguationData":[OD(0.0)],"derivedFrom":makeQuery(id+"F3.opExtrude","SWEPT_FACE",FACE,{"disambiguationData":[OSD([sQuery(id+"F2.wireOp",EDGE,"E16.6.0.3")])]})});
            var Q215;
            Q215=makeQuery(id+"F3.boolean.opBoolean","COPY",FACE,{"disambiguationData":[OD(0.0)],"derivedFrom":makeQuery(id+"F3.opExtrude","SWEPT_FACE",FACE,{"disambiguationData":[OSD([sQuery(id+"F2.wireOp",EDGE,"E16.2.0.3")])]})});
            var Q216;
            Q216=makeQuery(id+"F3.boolean.opBoolean","COPY",FACE,{"disambiguationData":[OD(0.0)],"derivedFrom":makeQuery(id+"F3.opExtrude","SWEPT_FACE",FACE,{"disambiguationData":[OSD([sQuery(id+"F2.wireOp",EDGE,"E16.4.0.3")])]})});
            var Q217;
            Q217=makeQuery(id+"F1.opExtrude","CAP_EDGE",EDGE,{"disambiguationData":[OSD([sQuery(id+"F0.wireOp",EDGE,"E3")])],"isStart":true});
            var Q218;
            Q218=makeQuery(id+"F3.boolean.opBoolean","INTERSECT",EDGE,{"derivedFrom":[makeQuery(id+"F1.opExtrude","SWEPT_FACE",FACE,{"disambiguationData":[OSD([sQuery(id+"F0.wireOp",EDGE,"E6.right")])]}),makeQuery(id+"F3.opExtrude","SWEPT_FACE",FACE,{"disambiguationData":[OSD([sQuery(id+"F2.wireOp",EDGE,"E16.2.0.3")])]})]});
            var Q219;
            Q219=makeQuery(id+"F3.boolean.opBoolean","INTERSECT",EDGE,{"derivedFrom":[makeQuery(id+"F1.opExtrude","SWEPT_FACE",FACE,{"disambiguationData":[OSD([sQuery(id+"F0.wireOp",EDGE,"E6.right")])]}),makeQuery(id+"F3.opExtrude","SWEPT_FACE",FACE,{"disambiguationData":[OSD([sQuery(id+"F2.wireOp",EDGE,"E16.6.0.3")])]})]});
            var Q220;
            Q220=makeQuery(id+"F5.boolean.opBoolean","COPY",EDGE,{"derivedFrom":makeQuery(id+"F5.opExtrude","SWEPT_EDGE",EDGE,{"disambiguationData":[OSD([sQuery(id+"F4.wireOp",EDGE,"f82c8603-6a34-46cd-9305-3e979d524e24.2.0.1"),sQuery(id+"F4.wireOp",EDGE,"f82c8603-6a34-46cd-9305-3e979d524e24.2.0.2")])]})});
            var Q221;
            Q221=makeQuery(id+"F1.opExtrude","CAP_EDGE",EDGE,{"disambiguationData":[OSD([sQuery(id+"F0.wireOp",EDGE,"E2")])],"isStart":true});
            var Q222;
            Q222=makeQuery(id+"F1.opExtrude","CAP_EDGE",EDGE,{"disambiguationData":[OSD([sQuery(id+"F0.wireOp",EDGE,"E6.right")])],"isStart":false});
            var Q223;
            Q223=makeQuery(id+"F1.opExtrude","CAP_EDGE",EDGE,{"disambiguationData":[OSD([sQuery(id+"F0.wireOp",EDGE,"E1.top")])],"isStart":false});
            var Q224;
            Q224=makeQuery(id+"F1.opExtrude","CAP_EDGE",EDGE,{"disambiguationData":[OSD([sQuery(id+"F0.wireOp",EDGE,"E7")])],"isStart":true});
            var Q225;
            Q225=makeQuery(id+"F1.opExtrude","CAP_EDGE",EDGE,{"disambiguationData":[OSD([sQuery(id+"F0.wireOp",EDGE,"E1.right")])],"isStart":true});
            var Q226;
            Q226=makeQuery(id+"F1.opExtrude","CAP_EDGE",EDGE,{"disambiguationData":[OSD([sQuery(id+"F0.wireOp",EDGE,"E1.top")])],"isStart":true});
            var Q227;
            Q227=makeQuery(id+"F1.opExtrude","CAP_EDGE",EDGE,{"disambiguationData":[OSD([sQuery(id+"F0.wireOp",EDGE,"E0.rect.right"),sQuery(id+"F0.wireOp",EDGE,"E5.left")])],"isStart":false});
            var Q228;
            Q228=makeQuery(id+"F3.boolean.opBoolean","INTERSECT",EDGE,{"derivedFrom":[makeQuery(id+"F1.opExtrude","SWEPT_FACE",FACE,{"disambiguationData":[OSD([sQuery(id+"F0.wireOp",EDGE,"E5.right")])]}),makeQuery(id+"F3.opExtrude","SWEPT_FACE",FACE,{"disambiguationData":[OSD([sQuery(id+"F2.wireOp",EDGE,"E16.1.0.1")])]})]});
            var Q229;
            Q229=makeQuery(id+"F3.boolean.opBoolean","INTERSECT",EDGE,{"derivedFrom":[makeQuery(id+"F1.opExtrude","SWEPT_FACE",FACE,{"disambiguationData":[OSD([sQuery(id+"F0.wireOp",EDGE,"E0.rect.left"),sQuery(id+"F0.wireOp",EDGE,"E1.left"),sQuery(id+"F0.wireOp",EDGE,"E6.left")])]}),makeQuery(id+"F3.opExtrude","SWEPT_FACE",FACE,{"disambiguationData":[OSD([sQuery(id+"F2.wireOp",EDGE,"E16.5.0.1")])]})]});
            var Q230;
            Q230=makeQuery(id+"F3.boolean.opBoolean","COPY",FACE,{"disambiguationData":[OD(1.0)],"derivedFrom":makeQuery(id+"F3.opExtrude","SWEPT_FACE",FACE,{"disambiguationData":[OSD([sQuery(id+"F2.wireOp",EDGE,"E16.6.0.0")])]})});
            var Q231;
            Q231=makeQuery(id+"F3.boolean.opBoolean","COPY",FACE,{"disambiguationData":[OD(1.0)],"derivedFrom":makeQuery(id+"F3.opExtrude","SWEPT_FACE",FACE,{"disambiguationData":[OSD([sQuery(id+"F2.wireOp",EDGE,"E16.4.0.0")])]})});
            var Q232;
            Q232=makeQuery(id+"F3.boolean.opBoolean","COPY",FACE,{"disambiguationData":[OD(1.0)],"derivedFrom":makeQuery(id+"F3.opExtrude","SWEPT_FACE",FACE,{"disambiguationData":[OSD([sQuery(id+"F2.wireOp",EDGE,"E16.2.0.0")])]})});
            var Q233;
            Q233=makeQuery(id+"F1.opExtrude","CAP_EDGE",EDGE,{"disambiguationData":[OSD([sQuery(id+"F0.wireOp",EDGE,"E5.top")])],"isStart":false});
            var Q234;
            Q234=makeQuery(id+"F1.opExtrude","CAP_EDGE",EDGE,{"disambiguationData":[OSD([sQuery(id+"F0.wireOp",EDGE,"E0.rect.top")])],"isStart":false});
            var Q235;
            Q235=makeQuery(id+"F3.boolean.opBoolean","INTERSECT",EDGE,{"derivedFrom":[makeQuery(id+"F1.opExtrude","SWEPT_FACE",FACE,{"disambiguationData":[OSD([sQuery(id+"F0.wireOp",EDGE,"E5.right")])]}),makeQuery(id+"F3.opExtrude","SWEPT_FACE",FACE,{"disambiguationData":[OSD([sQuery(id+"F2.wireOp",EDGE,"E16.5.0.0")])]})]});
            var Q236;
            Q236=makeQuery(id+"F3.boolean.opBoolean","INTERSECT",EDGE,{"derivedFrom":[makeQuery(id+"F1.opExtrude","SWEPT_FACE",FACE,{"disambiguationData":[OSD([sQuery(id+"F0.wireOp",EDGE,"E5.right")])]}),makeQuery(id+"F3.opExtrude","SWEPT_FACE",FACE,{"disambiguationData":[OSD([sQuery(id+"F2.wireOp",EDGE,"E16.1.0.0")])]})]});
            var Q237;
            Q237=makeQuery(id+"F3.boolean.opBoolean","INTERSECT",EDGE,{"derivedFrom":[makeQuery(id+"F1.opExtrude","SWEPT_FACE",FACE,{"disambiguationData":[OSD([sQuery(id+"F0.wireOp",EDGE,"E6.right")])]}),makeQuery(id+"F3.opExtrude","SWEPT_FACE",FACE,{"disambiguationData":[OSD([sQuery(id+"F2.wireOp",EDGE,"E16.5.0.0")])]})]});
            var Q238;
            Q238=makeQuery(id+"F3.boolean.opBoolean","INTERSECT",EDGE,{"derivedFrom":[makeQuery(id+"F1.opExtrude","SWEPT_FACE",FACE,{"disambiguationData":[OSD([sQuery(id+"F0.wireOp",EDGE,"E6.right")])]}),makeQuery(id+"F3.opExtrude","SWEPT_FACE",FACE,{"disambiguationData":[OSD([sQuery(id+"F2.wireOp",EDGE,"E16.1.0.0")])]})]});
            var Q239;
            Q239=makeQuery(id+"F3.boolean.opBoolean","COPY",EDGE,{"disambiguationData":[OD(0.0)],"derivedFrom":makeQuery(id+"F3.opExtrude","SWEPT_EDGE",EDGE,{"disambiguationData":[OSD([sQuery(id+"F2.wireOp",EDGE,"E16.6.0.1"),sQuery(id+"F2.wireOp",EDGE,"E16.6.0.2")])]})});
            var Q240;
            Q240=makeQuery(id+"F3.boolean.opBoolean","COPY",EDGE,{"disambiguationData":[OD(0.0)],"derivedFrom":makeQuery(id+"F3.opExtrude","SWEPT_EDGE",EDGE,{"disambiguationData":[OSD([sQuery(id+"F2.wireOp",EDGE,"E16.4.0.1"),sQuery(id+"F2.wireOp",EDGE,"E16.4.0.2")])]})});
            var Q241;
            Q241=makeQuery(id+"F3.boolean.opBoolean","INTERSECT",EDGE,{"derivedFrom":[makeQuery(id+"F1.opExtrude","SWEPT_FACE",FACE,{"disambiguationData":[OSD([sQuery(id+"F0.wireOp",EDGE,"E0.rect.left"),sQuery(id+"F0.wireOp",EDGE,"E1.left"),sQuery(id+"F0.wireOp",EDGE,"E6.left")])]}),makeQuery(id+"F3.opExtrude","SWEPT_FACE",FACE,{"disambiguationData":[OSD([sQuery(id+"F2.wireOp",EDGE,"E16.1.0.0")])]})]});
            var Q242;
            Q242=makeQuery(id+"F3.boolean.opBoolean","COPY",EDGE,{"disambiguationData":[OD(0.0)],"derivedFrom":makeQuery(id+"F3.opExtrude","SWEPT_EDGE",EDGE,{"disambiguationData":[OSD([sQuery(id+"F2.wireOp",EDGE,"E16.2.0.1"),sQuery(id+"F2.wireOp",EDGE,"E16.2.0.2")])]})});
            var Q243;
            Q243=makeQuery(id+"F3.boolean.opBoolean","COPY",EDGE,{"disambiguationData":[OD(0.0)],"derivedFrom":makeQuery(id+"F3.opExtrude","SWEPT_EDGE",EDGE,{"disambiguationData":[OSD([sQuery(id+"F2.wireOp",EDGE,"E11"),sQuery(id+"F2.wireOp",EDGE,"E15")])]})});
            var Q244;
            Q244=makeQuery(id+"F1.opExtrude","CAP_EDGE",EDGE,{"disambiguationData":[OSD([sQuery(id+"F0.wireOp",EDGE,"E5.top")])],"isStart":true});
            var Q245;
            Q245=makeQuery(id+"F3.boolean.opBoolean","INTERSECT",EDGE,{"derivedFrom":[makeQuery(id+"F1.opExtrude","SWEPT_FACE",FACE,{"disambiguationData":[OSD([sQuery(id+"F0.wireOp",EDGE,"E6.right")])]}),makeQuery(id+"F3.opExtrude","SWEPT_FACE",FACE,{"disambiguationData":[OSD([sQuery(id+"F2.wireOp",EDGE,"E15")])]})]});
            var Q246;
            Q246=makeQuery(id+"F3.boolean.opBoolean","INTERSECT",EDGE,{"derivedFrom":[makeQuery(id+"F1.opExtrude","SWEPT_FACE",FACE,{"disambiguationData":[OSD([sQuery(id+"F0.wireOp",EDGE,"E6.right")])]}),makeQuery(id+"F3.opExtrude","SWEPT_FACE",FACE,{"disambiguationData":[OSD([sQuery(id+"F2.wireOp",EDGE,"E16.4.0.3")])]})]});
            var Q247;
            Q247=makeQuery(id+"F3.boolean.opBoolean","INTERSECT",EDGE,{"derivedFrom":[makeQuery(id+"F1.opExtrude","SWEPT_FACE",FACE,{"disambiguationData":[OSD([sQuery(id+"F0.wireOp",EDGE,"E5.right")])]}),makeQuery(id+"F3.opExtrude","SWEPT_FACE",FACE,{"disambiguationData":[OSD([sQuery(id+"F2.wireOp",EDGE,"E16.4.0.3")])]})]});
            var Q248;
            Q248=makeQuery(id+"F3.boolean.opBoolean","INTERSECT",EDGE,{"derivedFrom":[makeQuery(id+"F1.opExtrude","SWEPT_FACE",FACE,{"disambiguationData":[OSD([sQuery(id+"F0.wireOp",EDGE,"E0.rect.left"),sQuery(id+"F0.wireOp",EDGE,"E1.left"),sQuery(id+"F0.wireOp",EDGE,"E6.left")])]}),makeQuery(id+"F3.opExtrude","SWEPT_FACE",FACE,{"disambiguationData":[OSD([sQuery(id+"F2.wireOp",EDGE,"E16.4.0.3")])]})]});
            var Q249;
            Q249=makeQuery(id+"F1.opExtrude","CAP_EDGE",EDGE,{"disambiguationData":[OSD([sQuery(id+"F0.wireOp",EDGE,"E0.rect.left"),sQuery(id+"F0.wireOp",EDGE,"E1.left"),sQuery(id+"F0.wireOp",EDGE,"E6.left")])],"isStart":false});
            var Q250;
            Q250=makeQuery(id+"F1.opExtrude","CAP_EDGE",EDGE,{"disambiguationData":[OSD([sQuery(id+"F0.wireOp",EDGE,"E5.right")])],"isStart":false});
            var Q251;
            Q251=makeQuery(id+"F3.boolean.opBoolean","COPY",FACE,{"disambiguationData":[OD(1.0)],"derivedFrom":makeQuery(id+"F3.opExtrude","SWEPT_FACE",FACE,{"disambiguationData":[OSD([sQuery(id+"F2.wireOp",EDGE,"E16.1.0.3")])]})});
            var Q252;
            Q252=makeQuery(id+"F3.boolean.opBoolean","COPY",EDGE,{"disambiguationData":[OD(0.0)],"derivedFrom":makeQuery(id+"F3.opExtrude","SWEPT_EDGE",EDGE,{"disambiguationData":[OSD([sQuery(id+"F2.wireOp",EDGE,"E16.4.0.0"),sQuery(id+"F2.wireOp",EDGE,"E16.4.0.1")])]})});
            var Q253;
            Q253=makeQuery(id+"F3.boolean.opBoolean","COPY",EDGE,{"disambiguationData":[OD(0.0)],"derivedFrom":makeQuery(id+"F3.opExtrude","SWEPT_EDGE",EDGE,{"disambiguationData":[OSD([sQuery(id+"F2.wireOp",EDGE,"E10"),sQuery(id+"F2.wireOp",EDGE,"E15")])]})});
            var Q254;
            Q254=makeQuery(id+"F3.boolean.opBoolean","COPY",EDGE,{"derivedFrom":makeQuery(id+"F3.opExtrude","CAP_EDGE",EDGE,{"disambiguationData":[OSD([sQuery(id+"F2.wireOp",EDGE,"E16.4.0.2")])],"isStart":true})});
            var Q255;
            Q255=makeQuery(id+"F3.boolean.opBoolean","INTERSECT",EDGE,{"derivedFrom":[makeQuery(id+"F1.opExtrude","SWEPT_FACE",FACE,{"disambiguationData":[OSD([sQuery(id+"F0.wireOp",EDGE,"E6.right")])]}),makeQuery(id+"F3.opExtrude","SWEPT_FACE",FACE,{"disambiguationData":[OSD([sQuery(id+"F2.wireOp",EDGE,"E14")])]})]});
            var Q256;
            Q256=makeQuery(id+"F3.boolean.opBoolean","INTERSECT",EDGE,{"derivedFrom":[makeQuery(id+"F1.opExtrude","SWEPT_FACE",FACE,{"disambiguationData":[OSD([sQuery(id+"F0.wireOp",EDGE,"E6.right")])]}),makeQuery(id+"F3.opExtrude","SWEPT_FACE",FACE,{"disambiguationData":[OSD([sQuery(id+"F2.wireOp",EDGE,"E16.4.0.2")])]})]});
            var Q257;
            Q257=makeQuery(id+"F3.boolean.opBoolean","COPY",FACE,{"disambiguationData":[OD(0.0)],"derivedFrom":makeQuery(id+"F3.opExtrude","SWEPT_FACE",FACE,{"disambiguationData":[OSD([sQuery(id+"F2.wireOp",EDGE,"E16.3.0.3")])]})});
            var Q258;
            Q258=makeQuery(id+"F3.boolean.opBoolean","COPY",FACE,{"disambiguationData":[OD(0.0)],"derivedFrom":makeQuery(id+"F3.opExtrude","SWEPT_FACE",FACE,{"disambiguationData":[OSD([sQuery(id+"F2.wireOp",EDGE,"E16.1.0.3")])]})});
            var Q259;
            Q259=makeQuery(id+"F3.boolean.opBoolean","COPY",FACE,{"disambiguationData":[OD(0.0)],"derivedFrom":makeQuery(id+"F3.opExtrude","SWEPT_FACE",FACE,{"disambiguationData":[OSD([sQuery(id+"F2.wireOp",EDGE,"E16.7.0.3")])]})});
            var Q260;
            Q260=makeQuery(id+"F3.boolean.opBoolean","COPY",FACE,{"disambiguationData":[OD(0.0)],"derivedFrom":makeQuery(id+"F3.opExtrude","SWEPT_FACE",FACE,{"disambiguationData":[OSD([sQuery(id+"F2.wireOp",EDGE,"E16.5.0.3")])]})});
            var Q261;
            Q261=makeQuery(id+"F1.opExtrude","CAP_EDGE",EDGE,{"disambiguationData":[OSD([sQuery(id+"F0.wireOp",EDGE,"E4")])],"isStart":true});
            var Q262;
            Q262=makeQuery(id+"F3.boolean.opBoolean","COPY",FACE,{"disambiguationData":[OD(1.0)],"derivedFrom":makeQuery(id+"F3.opExtrude","SWEPT_FACE",FACE,{"disambiguationData":[OSD([sQuery(id+"F2.wireOp",EDGE,"E16.5.0.2")])]})});
            var Q263;
            Q263=makeQuery(id+"F3.boolean.opBoolean","COPY",FACE,{"disambiguationData":[OD(1.0)],"derivedFrom":makeQuery(id+"F3.opExtrude","SWEPT_FACE",FACE,{"disambiguationData":[OSD([sQuery(id+"F2.wireOp",EDGE,"E16.1.0.2")])]})});
            var Q264;
            Q264=makeQuery(id+"F3.boolean.opBoolean","COPY",FACE,{"disambiguationData":[OD(1.0)],"derivedFrom":makeQuery(id+"F3.opExtrude","SWEPT_FACE",FACE,{"disambiguationData":[OSD([sQuery(id+"F2.wireOp",EDGE,"E16.3.0.2")])]})});
            var Q265;
            Q265=makeQuery(id+"F3.boolean.opBoolean","INTERSECT",EDGE,{"derivedFrom":[makeQuery(id+"F1.opExtrude","SWEPT_FACE",FACE,{"disambiguationData":[OSD([sQuery(id+"F0.wireOp",EDGE,"E0.rect.left"),sQuery(id+"F0.wireOp",EDGE,"E1.left"),sQuery(id+"F0.wireOp",EDGE,"E6.left")])]}),makeQuery(id+"F3.opExtrude","SWEPT_FACE",FACE,{"disambiguationData":[OSD([sQuery(id+"F2.wireOp",EDGE,"E11")])]})]});
            var Q266;
            Q266=makeQuery(id+"F3.boolean.opBoolean","INTERSECT",EDGE,{"derivedFrom":[makeQuery(id+"F1.opExtrude","SWEPT_FACE",FACE,{"disambiguationData":[OSD([sQuery(id+"F0.wireOp",EDGE,"E6.right")])]}),makeQuery(id+"F3.opExtrude","SWEPT_FACE",FACE,{"disambiguationData":[OSD([sQuery(id+"F2.wireOp",EDGE,"E16.4.0.1")])]})]});
            var Q267;
            Q267=makeQuery(id+"F3.boolean.opBoolean","INTERSECT",EDGE,{"derivedFrom":[makeQuery(id+"F1.opExtrude","SWEPT_FACE",FACE,{"disambiguationData":[OSD([sQuery(id+"F0.wireOp",EDGE,"E6.right")])]}),makeQuery(id+"F3.opExtrude","SWEPT_FACE",FACE,{"disambiguationData":[OSD([sQuery(id+"F2.wireOp",EDGE,"E11")])]})]});
            var Q268;
            Q268=makeQuery(id+"F3.boolean.opBoolean","INTERSECT",EDGE,{"derivedFrom":[makeQuery(id+"F1.opExtrude","SWEPT_FACE",FACE,{"disambiguationData":[OSD([sQuery(id+"F0.wireOp",EDGE,"E5.right")])]}),makeQuery(id+"F3.opExtrude","SWEPT_FACE",FACE,{"disambiguationData":[OSD([sQuery(id+"F2.wireOp",EDGE,"E11")])]})]});
            var Q269;
            Q269=makeQuery(id+"F5.boolean.opBoolean","COPY",EDGE,{"derivedFrom":makeQuery(id+"F5.opExtrude","TWEAK_EDGE",EDGE,{"derivedFrom":[makeQuery(id+"F1.opExtrude","SWEPT_FACE",FACE,{"disambiguationData":[OSD([sQuery(id+"F0.wireOp",EDGE,"E4")])]}),makeQuery(id+"F4.imprint","IMPRINT",EDGE,{"derivedFrom":sQuery(id+"F4.wireOp",EDGE,"f82c8603-6a34-46cd-9305-3e979d524e24.7.0.1")})]})});
            var Q270;
            Q270=makeQuery(id+"F5.boolean.opBoolean","COPY",EDGE,{"derivedFrom":makeQuery(id+"F5.opExtrude","SWEPT_EDGE",EDGE,{"disambiguationData":[OSD([sQuery(id+"F4.wireOp",EDGE,"f82c8603-6a34-46cd-9305-3e979d524e24.3.0.0"),sQuery(id+"F4.wireOp",EDGE,"f82c8603-6a34-46cd-9305-3e979d524e24.3.0.3")])]})});
            var Q271;
            Q271=makeQuery(id+"F5.boolean.opBoolean","COPY",EDGE,{"derivedFrom":makeQuery(id+"F5.opExtrude","SWEPT_EDGE",EDGE,{"disambiguationData":[OSD([sQuery(id+"F4.wireOp",EDGE,"f82c8603-6a34-46cd-9305-3e979d524e24.7.0.0"),sQuery(id+"F4.wireOp",EDGE,"f82c8603-6a34-46cd-9305-3e979d524e24.7.0.3")])]})});
            var Q272;
            Q272=makeQuery(id+"F5.boolean.opBoolean","COPY",EDGE,{"derivedFrom":makeQuery(id+"F5.opExtrude","CAP_EDGE",EDGE,{"disambiguationData":[OSD([sQuery(id+"F4.wireOp",EDGE,"f82c8603-6a34-46cd-9305-3e979d524e24.7.0.1")])],"isStart":true})});
            var Q273;
            Q273=makeQuery(id+"F1.opExtrude","CAP_EDGE",EDGE,{"disambiguationData":[OSD([sQuery(id+"F0.wireOp",EDGE,"E3")])],"isStart":false});
            var Q274;
            Q274=makeQuery(id+"F3.boolean.opBoolean","INTERSECT",EDGE,{"derivedFrom":[makeQuery(id+"F1.opExtrude","SWEPT_FACE",FACE,{"disambiguationData":[OSD([sQuery(id+"F0.wireOp",EDGE,"E6.right")])]}),makeQuery(id+"F3.opExtrude","SWEPT_FACE",FACE,{"disambiguationData":[OSD([sQuery(id+"F2.wireOp",EDGE,"E10")])]})]});
            var Q275;
            Q275=makeQuery(id+"F3.boolean.opBoolean","INTERSECT",EDGE,{"derivedFrom":[makeQuery(id+"F1.opExtrude","SWEPT_FACE",FACE,{"disambiguationData":[OSD([sQuery(id+"F0.wireOp",EDGE,"E6.right")])]}),makeQuery(id+"F3.opExtrude","SWEPT_FACE",FACE,{"disambiguationData":[OSD([sQuery(id+"F2.wireOp",EDGE,"E16.4.0.0")])]})]});
            var Q276;
            Q276=makeQuery(id+"F3.boolean.opBoolean","INTERSECT",EDGE,{"derivedFrom":[makeQuery(id+"F1.opExtrude","SWEPT_FACE",FACE,{"disambiguationData":[OSD([sQuery(id+"F0.wireOp",EDGE,"E5.right")])]}),makeQuery(id+"F3.opExtrude","SWEPT_FACE",FACE,{"disambiguationData":[OSD([sQuery(id+"F2.wireOp",EDGE,"E10")])]})]});
            var Q277;
            Q277=makeQuery(id+"F3.boolean.opBoolean","INTERSECT",EDGE,{"derivedFrom":[makeQuery(id+"F1.opExtrude","SWEPT_FACE",FACE,{"disambiguationData":[OSD([sQuery(id+"F0.wireOp",EDGE,"E5.right")])]}),makeQuery(id+"F3.opExtrude","SWEPT_FACE",FACE,{"disambiguationData":[OSD([sQuery(id+"F2.wireOp",EDGE,"E16.4.0.0")])]})]});
            var Q278;
            Q278=makeQuery(id+"F3.boolean.opBoolean","COPY",EDGE,{"disambiguationData":[OD(0.0)],"derivedFrom":makeQuery(id+"F3.opExtrude","SWEPT_EDGE",EDGE,{"disambiguationData":[OSD([sQuery(id+"F2.wireOp",EDGE,"E10"),sQuery(id+"F2.wireOp",EDGE,"E14")])]})});
            var Q279;
            Q279=makeQuery(id+"F3.boolean.opBoolean","COPY",EDGE,{"disambiguationData":[OD(0.0)],"derivedFrom":makeQuery(id+"F3.opExtrude","SWEPT_EDGE",EDGE,{"disambiguationData":[OSD([sQuery(id+"F2.wireOp",EDGE,"E16.2.0.0"),sQuery(id+"F2.wireOp",EDGE,"E16.2.0.3")])]})});
            var Q280;
            Q280=makeQuery(id+"F3.boolean.opBoolean","COPY",EDGE,{"derivedFrom":makeQuery(id+"F3.opExtrude","CAP_EDGE",EDGE,{"disambiguationData":[OSD([sQuery(id+"F2.wireOp",EDGE,"E16.4.0.0")])],"isStart":true})});
            var Q281;
            Q281=makeQuery(id+"F3.boolean.opBoolean","INTERSECT",EDGE,{"derivedFrom":[makeQuery(id+"F1.opExtrude","SWEPT_FACE",FACE,{"disambiguationData":[OSD([sQuery(id+"F0.wireOp",EDGE,"E0.rect.left"),sQuery(id+"F0.wireOp",EDGE,"E1.left"),sQuery(id+"F0.wireOp",EDGE,"E6.left")])]}),makeQuery(id+"F3.opExtrude","SWEPT_FACE",FACE,{"disambiguationData":[OSD([sQuery(id+"F2.wireOp",EDGE,"E16.4.0.0")])]})]});
            var Q282;
            Q282=makeQuery(id+"F3.boolean.opBoolean","COPY",EDGE,{"disambiguationData":[OD(0.0)],"derivedFrom":makeQuery(id+"F3.opExtrude","SWEPT_EDGE",EDGE,{"disambiguationData":[OSD([sQuery(id+"F2.wireOp",EDGE,"E16.6.0.0"),sQuery(id+"F2.wireOp",EDGE,"E16.6.0.3")])]})});
            var Q283;
            Q283=makeQuery(id+"F5.boolean.opBoolean","COPY",EDGE,{"derivedFrom":makeQuery(id+"F5.opExtrude","SWEPT_EDGE",EDGE,{"disambiguationData":[OSD([sQuery(id+"F4.wireOp",EDGE,"f82c8603-6a34-46cd-9305-3e979d524e24.3.0.1"),sQuery(id+"F4.wireOp",EDGE,"f82c8603-6a34-46cd-9305-3e979d524e24.3.0.3")])]})});
            var Q284;
            Q284=makeQuery(id+"F5.boolean.opBoolean","COPY",EDGE,{"derivedFrom":makeQuery(id+"F5.opExtrude","TWEAK_EDGE",EDGE,{"derivedFrom":[makeQuery(id+"F1.opExtrude","SWEPT_FACE",FACE,{"disambiguationData":[OSD([sQuery(id+"F0.wireOp",EDGE,"E4")])]}),makeQuery(id+"F4.imprint","IMPRINT",EDGE,{"derivedFrom":sQuery(id+"F4.wireOp",EDGE,"f82c8603-6a34-46cd-9305-3e979d524e24.7.0.2")})]})});
            var Q285;
            Q285=makeQuery(id+"F5.boolean.opBoolean","COPY",EDGE,{"derivedFrom":makeQuery(id+"F5.opExtrude","SWEPT_EDGE",EDGE,{"disambiguationData":[OSD([sQuery(id+"F4.wireOp",EDGE,"f82c8603-6a34-46cd-9305-3e979d524e24.7.0.1"),sQuery(id+"F4.wireOp",EDGE,"f82c8603-6a34-46cd-9305-3e979d524e24.7.0.3")])]})});
            var Q286;
            Q286=makeQuery(id+"F5.boolean.opBoolean","COPY",EDGE,{"derivedFrom":makeQuery(id+"F5.opExtrude","SWEPT_EDGE",EDGE,{"disambiguationData":[OSD([sQuery(id+"F4.wireOp",EDGE,"f82c8603-6a34-46cd-9305-3e979d524e24.7.0.1"),sQuery(id+"F4.wireOp",EDGE,"f82c8603-6a34-46cd-9305-3e979d524e24.7.0.2")])]})});
            var Q287;
            Q287=makeQuery(id+"F5.boolean.opBoolean","COPY",EDGE,{"derivedFrom":makeQuery(id+"F5.opExtrude","SWEPT_EDGE",EDGE,{"disambiguationData":[OSD([sQuery(id+"F4.wireOp",EDGE,"f82c8603-6a34-46cd-9305-3e979d524e24.3.0.1"),sQuery(id+"F4.wireOp",EDGE,"f82c8603-6a34-46cd-9305-3e979d524e24.3.0.2")])]})});
            var Q288;
            Q288=makeQuery(id+"F1.opExtrude","CAP_EDGE",EDGE,{"disambiguationData":[OSD([sQuery(id+"F0.wireOp",EDGE,"E4")])],"isStart":false});
            var Q289;
            Q289=makeQuery(id+"F3.boolean.opBoolean","COPY",EDGE,{"disambiguationData":[OD(1.0)],"derivedFrom":makeQuery(id+"F3.opExtrude","SWEPT_EDGE",EDGE,{"disambiguationData":[OSD([sQuery(id+"F2.wireOp",EDGE,"E16.7.0.2"),sQuery(id+"F2.wireOp",EDGE,"E16.7.0.3")])]})});
            var Q290;
            Q290=makeQuery(id+"F3.boolean.opBoolean","INTERSECT",EDGE,{"derivedFrom":[makeQuery(id+"F1.opExtrude","SWEPT_FACE",FACE,{"disambiguationData":[OSD([sQuery(id+"F0.wireOp",EDGE,"E0.rect.left"),sQuery(id+"F0.wireOp",EDGE,"E1.left"),sQuery(id+"F0.wireOp",EDGE,"E6.left")])]}),makeQuery(id+"F3.opExtrude","SWEPT_FACE",FACE,{"disambiguationData":[OSD([sQuery(id+"F2.wireOp",EDGE,"E16.3.0.3")])]})]});
            var Q291;
            Q291=makeQuery(id+"F3.boolean.opBoolean","INTERSECT",EDGE,{"derivedFrom":[makeQuery(id+"F1.opExtrude","SWEPT_FACE",FACE,{"disambiguationData":[OSD([sQuery(id+"F0.wireOp",EDGE,"E6.right")])]}),makeQuery(id+"F3.opExtrude","SWEPT_FACE",FACE,{"disambiguationData":[OSD([sQuery(id+"F2.wireOp",EDGE,"E16.3.0.3")])]})]});
            var Q292;
            Q292=makeQuery(id+"F3.boolean.opBoolean","INTERSECT",EDGE,{"derivedFrom":[makeQuery(id+"F1.opExtrude","SWEPT_FACE",FACE,{"disambiguationData":[OSD([sQuery(id+"F0.wireOp",EDGE,"E5.right")])]}),makeQuery(id+"F3.opExtrude","SWEPT_FACE",FACE,{"disambiguationData":[OSD([sQuery(id+"F2.wireOp",EDGE,"E16.7.0.3")])]})]});
            var Q293;
            Q293=makeQuery(id+"F3.boolean.opBoolean","INTERSECT",EDGE,{"derivedFrom":[makeQuery(id+"F1.opExtrude","SWEPT_FACE",FACE,{"disambiguationData":[OSD([sQuery(id+"F0.wireOp",EDGE,"E0.rect.left"),sQuery(id+"F0.wireOp",EDGE,"E1.left"),sQuery(id+"F0.wireOp",EDGE,"E6.left")])]}),makeQuery(id+"F3.opExtrude","SWEPT_FACE",FACE,{"disambiguationData":[OSD([sQuery(id+"F2.wireOp",EDGE,"E16.7.0.3")])]})]});
            var Q294;
            Q294=makeQuery(id+"F3.boolean.opBoolean","INTERSECT",EDGE,{"derivedFrom":[makeQuery(id+"F1.opExtrude","SWEPT_FACE",FACE,{"disambiguationData":[OSD([sQuery(id+"F0.wireOp",EDGE,"E6.right")])]}),makeQuery(id+"F3.opExtrude","SWEPT_FACE",FACE,{"disambiguationData":[OSD([sQuery(id+"F2.wireOp",EDGE,"E16.7.0.2")])]})]});
            var Q295;
            Q295=makeQuery(id+"F5.boolean.opBoolean","COPY",EDGE,{"derivedFrom":makeQuery(id+"F5.opExtrude","TWEAK_EDGE",EDGE,{"derivedFrom":[makeQuery(id+"F1.opExtrude","SWEPT_FACE",FACE,{"disambiguationData":[OSD([sQuery(id+"F0.wireOp",EDGE,"E4")])]}),makeQuery(id+"F4.imprint","IMPRINT",EDGE,{"derivedFrom":sQuery(id+"F4.wireOp",EDGE,"f82c8603-6a34-46cd-9305-3e979d524e24.1.0.2")})]})});
            var Q296;
            Q296=makeQuery(id+"F3.boolean.opBoolean","INTERSECT",EDGE,{"derivedFrom":[makeQuery(id+"F1.opExtrude","SWEPT_FACE",FACE,{"disambiguationData":[OSD([sQuery(id+"F0.wireOp",EDGE,"E0.rect.left"),sQuery(id+"F0.wireOp",EDGE,"E1.left"),sQuery(id+"F0.wireOp",EDGE,"E6.left")])]}),makeQuery(id+"F3.opExtrude","SWEPT_FACE",FACE,{"disambiguationData":[OSD([sQuery(id+"F2.wireOp",EDGE,"E16.7.0.2")])]})]});
            var Q297;
            Q297=makeQuery(id+"F3.boolean.opBoolean","INTERSECT",EDGE,{"derivedFrom":[makeQuery(id+"F1.opExtrude","SWEPT_FACE",FACE,{"disambiguationData":[OSD([sQuery(id+"F0.wireOp",EDGE,"E5.right")])]}),makeQuery(id+"F3.opExtrude","SWEPT_FACE",FACE,{"disambiguationData":[OSD([sQuery(id+"F2.wireOp",EDGE,"E16.7.0.2")])]})]});
            var Q298;
            Q298=makeQuery(id+"F5.boolean.opBoolean","COPY",EDGE,{"derivedFrom":makeQuery(id+"F5.opExtrude","TWEAK_EDGE",EDGE,{"derivedFrom":[makeQuery(id+"F1.opExtrude","SWEPT_FACE",FACE,{"disambiguationData":[OSD([sQuery(id+"F0.wireOp",EDGE,"E4")])]}),makeQuery(id+"F4.imprint","IMPRINT",EDGE,{"derivedFrom":sQuery(id+"F4.wireOp",EDGE,"f82c8603-6a34-46cd-9305-3e979d524e24.1.0.3")})]})});
            var Q299;
            Q299=makeQuery(id+"F3.boolean.opBoolean","COPY",EDGE,{"disambiguationData":[OD(0.0)],"derivedFrom":makeQuery(id+"F3.opExtrude","SWEPT_EDGE",EDGE,{"disambiguationData":[OSD([sQuery(id+"F2.wireOp",EDGE,"E16.3.0.2"),sQuery(id+"F2.wireOp",EDGE,"E16.3.0.3")])]})});
            var Q300;
            Q300=makeQuery(id+"F3.boolean.opBoolean","COPY",EDGE,{"disambiguationData":[OD(0.0)],"derivedFrom":makeQuery(id+"F3.opExtrude","SWEPT_EDGE",EDGE,{"disambiguationData":[OSD([sQuery(id+"F2.wireOp",EDGE,"E16.5.0.2"),sQuery(id+"F2.wireOp",EDGE,"E16.5.0.3")])]})});
            var Q301;
            Q301=makeQuery(id+"F3.boolean.opBoolean","COPY",EDGE,{"disambiguationData":[OD(0.0)],"derivedFrom":makeQuery(id+"F3.opExtrude","SWEPT_EDGE",EDGE,{"disambiguationData":[OSD([sQuery(id+"F2.wireOp",EDGE,"E16.7.0.2"),sQuery(id+"F2.wireOp",EDGE,"E16.7.0.3")])]})});
            var Q302;
            Q302=makeQuery(id+"F3.boolean.opBoolean","INTERSECT",EDGE,{"derivedFrom":[makeQuery(id+"F1.opExtrude","SWEPT_FACE",FACE,{"disambiguationData":[OSD([sQuery(id+"F0.wireOp",EDGE,"E0.rect.left"),sQuery(id+"F0.wireOp",EDGE,"E1.left"),sQuery(id+"F0.wireOp",EDGE,"E6.left")])]}),makeQuery(id+"F3.opExtrude","SWEPT_FACE",FACE,{"disambiguationData":[OSD([sQuery(id+"F2.wireOp",EDGE,"E16.3.0.2")])]})]});
            var Q303;
            Q303=makeQuery(id+"F3.boolean.opBoolean","COPY",EDGE,{"disambiguationData":[OD(0.0)],"derivedFrom":makeQuery(id+"F3.opExtrude","SWEPT_EDGE",EDGE,{"disambiguationData":[OSD([sQuery(id+"F2.wireOp",EDGE,"E16.1.0.2"),sQuery(id+"F2.wireOp",EDGE,"E16.1.0.3")])]})});
            var Q304;
            Q304=makeQuery(id+"F5.boolean.opBoolean","COPY",EDGE,{"derivedFrom":makeQuery(id+"F5.opExtrude","TWEAK_EDGE",EDGE,{"derivedFrom":[makeQuery(id+"F1.opExtrude","SWEPT_FACE",FACE,{"disambiguationData":[OSD([sQuery(id+"F0.wireOp",EDGE,"E4")])]}),makeQuery(id+"F4.imprint","IMPRINT",EDGE,{"derivedFrom":sQuery(id+"F4.wireOp",EDGE,"E18")})]})});
            var Q305;
            Q305=makeQuery(id+"F5.boolean.opBoolean","COPY",FACE,{"derivedFrom":makeQuery(id+"F5.opExtrude","SWEPT_FACE",FACE,{"disambiguationData":[OSD([sQuery(id+"F4.wireOp",EDGE,"E22")])]})});
            var Q306;
            Q306=makeQuery(id+"F5.boolean.opBoolean","COPY",EDGE,{"derivedFrom":makeQuery(id+"F5.opExtrude","TWEAK_EDGE",EDGE,{"derivedFrom":[makeQuery(id+"F1.opExtrude","SWEPT_FACE",FACE,{"disambiguationData":[OSD([sQuery(id+"F0.wireOp",EDGE,"E4")])]}),makeQuery(id+"F4.imprint","IMPRINT",EDGE,{"derivedFrom":sQuery(id+"F4.wireOp",EDGE,"E22")})]})});
            var Q307;
            Q307=makeQuery(id+"F5.boolean.opBoolean","COPY",EDGE,{"derivedFrom":makeQuery(id+"F5.opExtrude","TWEAK_EDGE",EDGE,{"derivedFrom":[makeQuery(id+"F1.opExtrude","SWEPT_FACE",FACE,{"disambiguationData":[OSD([sQuery(id+"F0.wireOp",EDGE,"E4")])]}),makeQuery(id+"F4.imprint","IMPRINT",EDGE,{"derivedFrom":sQuery(id+"F4.wireOp",EDGE,"f82c8603-6a34-46cd-9305-3e979d524e24.1.0.0")})]})});
            var Q308;
            Q308=makeQuery(id+"F5.boolean.opBoolean","COPY",EDGE,{"derivedFrom":makeQuery(id+"F5.opExtrude","TWEAK_EDGE",EDGE,{"derivedFrom":[makeQuery(id+"F1.opExtrude","SWEPT_FACE",FACE,{"disambiguationData":[OSD([sQuery(id+"F0.wireOp",EDGE,"E4")])]}),makeQuery(id+"F4.imprint","IMPRINT",EDGE,{"derivedFrom":sQuery(id+"F4.wireOp",EDGE,"f82c8603-6a34-46cd-9305-3e979d524e24.3.0.0")})]})});
            var Q309;
            Q309=makeQuery(id+"F5.boolean.opBoolean","COPY",EDGE,{"derivedFrom":makeQuery(id+"F5.opExtrude","CAP_EDGE",EDGE,{"disambiguationData":[OSD([sQuery(id+"F4.wireOp",EDGE,"f82c8603-6a34-46cd-9305-3e979d524e24.4.0.0")])],"isStart":true})});
            var Q310;
            Q310=makeQuery(id+"F5.boolean.opBoolean","COPY",EDGE,{"derivedFrom":makeQuery(id+"F5.opExtrude","CAP_EDGE",EDGE,{"disambiguationData":[OSD([sQuery(id+"F4.wireOp",EDGE,"E17")])],"isStart":true})});
            var Q311;
            Q311=makeQuery(id+"F5.boolean.opBoolean","COPY",EDGE,{"derivedFrom":makeQuery(id+"F5.opExtrude","SWEPT_EDGE",EDGE,{"disambiguationData":[OSD([sQuery(id+"F4.wireOp",EDGE,"E17"),sQuery(id+"F4.wireOp",EDGE,"E21")])]})});
            var Q312;
            Q312=makeQuery(id+"F5.boolean.opBoolean","COPY",EDGE,{"derivedFrom":makeQuery(id+"F5.opExtrude","TWEAK_EDGE",EDGE,{"derivedFrom":[makeQuery(id+"F1.opExtrude","SWEPT_FACE",FACE,{"disambiguationData":[OSD([sQuery(id+"F0.wireOp",EDGE,"E4")])]}),makeQuery(id+"F4.imprint","IMPRINT",EDGE,{"derivedFrom":sQuery(id+"F4.wireOp",EDGE,"f82c8603-6a34-46cd-9305-3e979d524e24.4.0.0")})]})});
            var Q313;
            Q313=makeQuery(id+"F3.boolean.opBoolean","COPY",FACE,{"disambiguationData":[OD(0.0)],"derivedFrom":makeQuery(id+"F3.opExtrude","SWEPT_FACE",FACE,{"disambiguationData":[OSD([sQuery(id+"F2.wireOp",EDGE,"E16.7.0.1")])]})});
            var Q314;
            Q314=makeQuery(id+"F3.boolean.opBoolean","COPY",FACE,{"disambiguationData":[OD(0.0)],"derivedFrom":makeQuery(id+"F3.opExtrude","SWEPT_FACE",FACE,{"disambiguationData":[OSD([sQuery(id+"F2.wireOp",EDGE,"E16.5.0.1")])]})});
            var Q315;
            Q315=makeQuery(id+"F5.boolean.opBoolean","COPY",EDGE,{"derivedFrom":makeQuery(id+"F5.opExtrude","TWEAK_EDGE",EDGE,{"derivedFrom":[makeQuery(id+"F1.opExtrude","SWEPT_FACE",FACE,{"disambiguationData":[OSD([sQuery(id+"F0.wireOp",EDGE,"E4")])]}),makeQuery(id+"F4.imprint","IMPRINT",EDGE,{"derivedFrom":sQuery(id+"F4.wireOp",EDGE,"f82c8603-6a34-46cd-9305-3e979d524e24.2.0.0")})]})});
            var Q316;
            Q316=makeQuery(id+"F5.boolean.opBoolean","COPY",EDGE,{"derivedFrom":makeQuery(id+"F5.opExtrude","TWEAK_EDGE",EDGE,{"derivedFrom":[makeQuery(id+"F1.opExtrude","SWEPT_FACE",FACE,{"disambiguationData":[OSD([sQuery(id+"F0.wireOp",EDGE,"E4")])]}),makeQuery(id+"F4.imprint","IMPRINT",EDGE,{"derivedFrom":sQuery(id+"F4.wireOp",EDGE,"f82c8603-6a34-46cd-9305-3e979d524e24.2.0.1")})]})});
            var Q317;
            Q317=makeQuery(id+"F5.boolean.opBoolean","COPY",EDGE,{"derivedFrom":makeQuery(id+"F5.opExtrude","TWEAK_EDGE",EDGE,{"derivedFrom":[makeQuery(id+"F1.opExtrude","SWEPT_FACE",FACE,{"disambiguationData":[OSD([sQuery(id+"F0.wireOp",EDGE,"E4")])]}),makeQuery(id+"F4.imprint","IMPRINT",EDGE,{"derivedFrom":sQuery(id+"F4.wireOp",EDGE,"f82c8603-6a34-46cd-9305-3e979d524e24.2.0.2")})]})});
            var Q318;
            Q318=makeQuery(id+"F5.boolean.opBoolean","COPY",EDGE,{"derivedFrom":makeQuery(id+"F5.opExtrude","TWEAK_EDGE",EDGE,{"derivedFrom":[makeQuery(id+"F1.opExtrude","SWEPT_FACE",FACE,{"disambiguationData":[OSD([sQuery(id+"F0.wireOp",EDGE,"E4")])]}),makeQuery(id+"F4.imprint","IMPRINT",EDGE,{"derivedFrom":sQuery(id+"F4.wireOp",EDGE,"E17")})]})});
            var Q319;
            Q319=makeQuery(id+"F5.boolean.opBoolean","COPY",EDGE,{"derivedFrom":makeQuery(id+"F5.opExtrude","TWEAK_EDGE",EDGE,{"derivedFrom":[makeQuery(id+"F1.opExtrude","SWEPT_FACE",FACE,{"disambiguationData":[OSD([sQuery(id+"F0.wireOp",EDGE,"E4")])]}),makeQuery(id+"F4.imprint","IMPRINT",EDGE,{"derivedFrom":sQuery(id+"F4.wireOp",EDGE,"f82c8603-6a34-46cd-9305-3e979d524e24.3.0.2")})]})});
            var Q320;
            Q320=makeQuery(id+"F3.boolean.opBoolean","INTERSECT",EDGE,{"derivedFrom":[makeQuery(id+"F1.opExtrude","SWEPT_FACE",FACE,{"disambiguationData":[OSD([sQuery(id+"F0.wireOp",EDGE,"E0.rect.left"),sQuery(id+"F0.wireOp",EDGE,"E1.left"),sQuery(id+"F0.wireOp",EDGE,"E6.left")])]}),makeQuery(id+"F3.opExtrude","SWEPT_FACE",FACE,{"disambiguationData":[OSD([sQuery(id+"F2.wireOp",EDGE,"E16.3.0.1")])]})]});
            var Q321;
            Q321=makeQuery(id+"F3.boolean.opBoolean","COPY",EDGE,{"derivedFrom":makeQuery(id+"F3.opExtrude","CAP_EDGE",EDGE,{"disambiguationData":[OSD([sQuery(id+"F2.wireOp",EDGE,"E16.1.0.2")])],"isStart":true})});
            var Q322;
            Q322=makeQuery(id+"F3.boolean.opBoolean","INTERSECT",EDGE,{"derivedFrom":[makeQuery(id+"F1.opExtrude","SWEPT_FACE",FACE,{"disambiguationData":[OSD([sQuery(id+"F0.wireOp",EDGE,"E6.right")])]}),makeQuery(id+"F3.opExtrude","SWEPT_FACE",FACE,{"disambiguationData":[OSD([sQuery(id+"F2.wireOp",EDGE,"E16.7.0.1")])]})]});
            var Q323;
            Q323=makeQuery(id+"F3.boolean.opBoolean","COPY",EDGE,{"derivedFrom":makeQuery(id+"F3.opExtrude","CAP_EDGE",EDGE,{"disambiguationData":[OSD([sQuery(id+"F2.wireOp",EDGE,"E16.1.0.0")])],"isStart":true})});
            var Q324;
            Q324=makeQuery(id+"F3.boolean.opBoolean","INTERSECT",EDGE,{"derivedFrom":[makeQuery(id+"F1.opExtrude","SWEPT_FACE",FACE,{"disambiguationData":[OSD([sQuery(id+"F0.wireOp",EDGE,"E5.right")])]}),makeQuery(id+"F3.opExtrude","SWEPT_FACE",FACE,{"disambiguationData":[OSD([sQuery(id+"F2.wireOp",EDGE,"E16.3.0.1")])]})]});
            var Q325;
            Q325=makeQuery(id+"F3.boolean.opBoolean","INTERSECT",EDGE,{"derivedFrom":[makeQuery(id+"F1.opExtrude","SWEPT_FACE",FACE,{"disambiguationData":[OSD([sQuery(id+"F0.wireOp",EDGE,"E0.rect.left"),sQuery(id+"F0.wireOp",EDGE,"E1.left"),sQuery(id+"F0.wireOp",EDGE,"E6.left")])]}),makeQuery(id+"F3.opExtrude","SWEPT_FACE",FACE,{"disambiguationData":[OSD([sQuery(id+"F2.wireOp",EDGE,"E16.7.0.1")])]})]});
            var Q326;
            Q326=makeQuery(id+"F3.boolean.opBoolean","COPY",FACE,{"disambiguationData":[OD(1.0)],"derivedFrom":makeQuery(id+"F3.opExtrude","SWEPT_FACE",FACE,{"disambiguationData":[OSD([sQuery(id+"F2.wireOp",EDGE,"E10")])]})});
            var Q327;
            Q327=makeQuery(id+"F3.boolean.opBoolean","INTERSECT",EDGE,{"derivedFrom":[makeQuery(id+"F1.opExtrude","SWEPT_FACE",FACE,{"disambiguationData":[OSD([sQuery(id+"F0.wireOp",EDGE,"E6.right")])]}),makeQuery(id+"F3.opExtrude","SWEPT_FACE",FACE,{"disambiguationData":[OSD([sQuery(id+"F2.wireOp",EDGE,"E16.3.0.1")])]})]});
            var Q328;
            Q328=makeQuery(id+"F3.boolean.opBoolean","INTERSECT",EDGE,{"derivedFrom":[makeQuery(id+"F1.opExtrude","SWEPT_FACE",FACE,{"disambiguationData":[OSD([sQuery(id+"F0.wireOp",EDGE,"E5.right")])]}),makeQuery(id+"F3.opExtrude","SWEPT_FACE",FACE,{"disambiguationData":[OSD([sQuery(id+"F2.wireOp",EDGE,"E16.7.0.1")])]})]});
            var Q329;
            Q329=makeQuery(id+"F3.boolean.opBoolean","COPY",EDGE,{"derivedFrom":makeQuery(id+"F3.opExtrude","CAP_EDGE",EDGE,{"disambiguationData":[OSD([sQuery(id+"F2.wireOp",EDGE,"E10")])],"isStart":true})});
            var Q330;
            Q330=makeQuery(id+"F3.boolean.opBoolean","COPY",FACE,{"disambiguationData":[OD(1.0)],"derivedFrom":makeQuery(id+"F3.opExtrude","SWEPT_FACE",FACE,{"disambiguationData":[OSD([sQuery(id+"F2.wireOp",EDGE,"E16.7.0.0")])]})});
            var Q331;
            Q331=makeQuery(id+"F5.boolean.opBoolean","COPY",EDGE,{"derivedFrom":makeQuery(id+"F5.opExtrude","SWEPT_EDGE",EDGE,{"disambiguationData":[OSD([sQuery(id+"F4.wireOp",EDGE,"f82c8603-6a34-46cd-9305-3e979d524e24.4.0.0"),sQuery(id+"F4.wireOp",EDGE,"f82c8603-6a34-46cd-9305-3e979d524e24.4.0.3")])]})});
            var Q332;
            Q332=makeQuery(id+"F3.boolean.opBoolean","COPY",FACE,{"disambiguationData":[OD(1.0)],"derivedFrom":makeQuery(id+"F3.opExtrude","SWEPT_FACE",FACE,{"disambiguationData":[OSD([sQuery(id+"F2.wireOp",EDGE,"E16.5.0.0")])]})});
            var Q333;
            Q333=makeQuery(id+"F3.boolean.opBoolean","COPY",FACE,{"disambiguationData":[OD(1.0)],"derivedFrom":makeQuery(id+"F3.opExtrude","SWEPT_FACE",FACE,{"disambiguationData":[OSD([sQuery(id+"F2.wireOp",EDGE,"E16.3.0.0")])]})});
            var Q334;
            Q334=makeQuery(id+"F5.boolean.opBoolean","COPY",EDGE,{"derivedFrom":makeQuery(id+"F5.opExtrude","TWEAK_EDGE",EDGE,{"derivedFrom":[makeQuery(id+"F1.opExtrude","SWEPT_FACE",FACE,{"disambiguationData":[OSD([sQuery(id+"F0.wireOp",EDGE,"E4")])]}),makeQuery(id+"F4.imprint","IMPRINT",EDGE,{"derivedFrom":sQuery(id+"F4.wireOp",EDGE,"f82c8603-6a34-46cd-9305-3e979d524e24.4.0.1")})]})});
            var Q335;
            Q335=makeQuery(id+"F3.boolean.opBoolean","COPY",FACE,{"disambiguationData":[OD(1.0)],"derivedFrom":makeQuery(id+"F3.opExtrude","SWEPT_FACE",FACE,{"disambiguationData":[OSD([sQuery(id+"F2.wireOp",EDGE,"E15")])]})});
            var Q336;
            Q336=makeQuery(id+"F3.boolean.opBoolean","COPY",EDGE,{"derivedFrom":makeQuery(id+"F3.opExtrude","CAP_EDGE",EDGE,{"disambiguationData":[OSD([sQuery(id+"F2.wireOp",EDGE,"E16.3.0.0")])],"isStart":true})});
            var Q337;
            Q337=makeQuery(id+"F3.boolean.opBoolean","COPY",FACE,{"disambiguationData":[OD(1.0)],"derivedFrom":makeQuery(id+"F3.opExtrude","SWEPT_FACE",FACE,{"disambiguationData":[OSD([sQuery(id+"F2.wireOp",EDGE,"E14")])]})});
            var Q338;
            Q338=makeQuery(id+"F3.boolean.opBoolean","COPY",EDGE,{"derivedFrom":makeQuery(id+"F3.opExtrude","CAP_EDGE",EDGE,{"disambiguationData":[OSD([sQuery(id+"F2.wireOp",EDGE,"E16.2.0.2")])],"isStart":true})});
            var Q339;
            Q339=makeQuery(id+"F3.boolean.opBoolean","COPY",FACE,{"disambiguationData":[OD(0.0)],"derivedFrom":makeQuery(id+"F3.opExtrude","SWEPT_FACE",FACE,{"disambiguationData":[OSD([sQuery(id+"F2.wireOp",EDGE,"E15")])]})});
            var Q340;
            Q340=makeQuery(id+"F3.boolean.opBoolean","COPY",FACE,{"disambiguationData":[OD(1.0)],"derivedFrom":makeQuery(id+"F3.opExtrude","SWEPT_FACE",FACE,{"disambiguationData":[OSD([sQuery(id+"F2.wireOp",EDGE,"E11")])]})});
            var Q341;
            Q341=makeQuery(id+"F3.boolean.opBoolean","COPY",EDGE,{"derivedFrom":makeQuery(id+"F3.opExtrude","CAP_EDGE",EDGE,{"disambiguationData":[OSD([sQuery(id+"F2.wireOp",EDGE,"E16.2.0.0")])],"isStart":true})});
            var Q342;
            Q342=makeQuery(id+"F3.boolean.opBoolean","COPY",FACE,{"disambiguationData":[OD(1.0)],"derivedFrom":makeQuery(id+"F3.opExtrude","SWEPT_FACE",FACE,{"disambiguationData":[OSD([sQuery(id+"F2.wireOp",EDGE,"E16.1.0.0")])]})});
            var Q343;
            Q343=makeQuery(id+"F3.boolean.opBoolean","COPY",FACE,{"disambiguationData":[OD(1.0)],"derivedFrom":makeQuery(id+"F3.opExtrude","SWEPT_FACE",FACE,{"disambiguationData":[OSD([sQuery(id+"F2.wireOp",EDGE,"E16.1.0.1")])]})});
            var Q344;
            Q344=makeQuery(id+"F5.boolean.opBoolean","COPY",EDGE,{"derivedFrom":makeQuery(id+"F5.opExtrude","SWEPT_EDGE",EDGE,{"disambiguationData":[OSD([sQuery(id+"F4.wireOp",EDGE,"E18"),sQuery(id+"F4.wireOp",EDGE,"E22")])]})});
            var Q345;
            Q345=makeQuery(id+"F5.boolean.opBoolean","COPY",EDGE,{"derivedFrom":makeQuery(id+"F5.opExtrude","SWEPT_EDGE",EDGE,{"disambiguationData":[OSD([sQuery(id+"F4.wireOp",EDGE,"f82c8603-6a34-46cd-9305-3e979d524e24.4.0.1"),sQuery(id+"F4.wireOp",EDGE,"f82c8603-6a34-46cd-9305-3e979d524e24.4.0.3")])]})});
            var Q346;
            Q346=makeQuery(id+"F5.boolean.opBoolean","COPY",EDGE,{"derivedFrom":makeQuery(id+"F5.opExtrude","TWEAK_EDGE",EDGE,{"derivedFrom":[makeQuery(id+"F1.opExtrude","SWEPT_FACE",FACE,{"disambiguationData":[OSD([sQuery(id+"F0.wireOp",EDGE,"E4")])]}),makeQuery(id+"F4.imprint","IMPRINT",EDGE,{"derivedFrom":sQuery(id+"F4.wireOp",EDGE,"f82c8603-6a34-46cd-9305-3e979d524e24.4.0.2")})]})});
            var Q347;
            Q347=makeQuery(id+"F1.opExtrude","SWEPT_EDGE",EDGE,{"disambiguationData":[OSD([sQuery(id+"F0.wireOp",EDGE,"E0.rect.bottom"),sQuery(id+"F0.wireOp",EDGE,"E4")])]});
            var Q348;
            Q348=makeQuery(id+"F1.opExtrude","SWEPT_EDGE",EDGE,{"disambiguationData":[OSD([sQuery(id+"F0.wireOp",EDGE,"E0.rect.top"),sQuery(id+"F0.wireOp",EDGE,"E6.right")])]});
            var Q349;
            Q349=makeQuery(id+"F1.opExtrude","SWEPT_EDGE",EDGE,{"disambiguationData":[OSD([sQuery(id+"F0.wireOp",EDGE,"E0.rect.top"),sQuery(id+"F0.wireOp",EDGE,"E5.right")])]});
            var Q350;
            Q350=makeQuery(id+"F1.opExtrude","SWEPT_EDGE",EDGE,{"disambiguationData":[OSD([sQuery(id+"F0.wireOp",EDGE,"E5.top"),sQuery(id+"F0.wireOp",EDGE,"E5.right")])]});
            var Q351;
            Q351=makeQuery(id+"F1.opExtrude","SWEPT_EDGE",EDGE,{"disambiguationData":[OSD([sQuery(id+"F0.wireOp",EDGE,"E6.top"),sQuery(id+"F0.wireOp",EDGE,"E6.left")])]});
            var Q352;
            Q352=makeQuery(id+"F3.boolean.opBoolean","COPY",FACE,{"disambiguationData":[OD(1.0)],"derivedFrom":makeQuery(id+"F3.opExtrude","SWEPT_FACE",FACE,{"disambiguationData":[OSD([sQuery(id+"F2.wireOp",EDGE,"E16.7.0.1")])]})});
            var Q353;
            Q353=makeQuery(id+"F3.boolean.opBoolean","COPY",FACE,{"disambiguationData":[OD(1.0)],"derivedFrom":makeQuery(id+"F3.opExtrude","SWEPT_FACE",FACE,{"disambiguationData":[OSD([sQuery(id+"F2.wireOp",EDGE,"E16.3.0.1")])]})});
            var Q354;
            Q354=makeQuery(id+"F3.boolean.opBoolean","COPY",FACE,{"disambiguationData":[OD(1.0)],"derivedFrom":makeQuery(id+"F3.opExtrude","SWEPT_FACE",FACE,{"disambiguationData":[OSD([sQuery(id+"F2.wireOp",EDGE,"E16.5.0.1")])]})});
            var Q355;
            Q355=makeQuery(id+"F1.opExtrude","SWEPT_FACE",FACE,{"disambiguationData":[OSD([sQuery(id+"F0.wireOp",EDGE,"E6.top")])]});
            var Q356;
            Q356=makeQuery(id+"F5.boolean.opBoolean","COPY",EDGE,{"derivedFrom":makeQuery(id+"F5.opExtrude","SWEPT_EDGE",EDGE,{"disambiguationData":[OSD([sQuery(id+"F4.wireOp",EDGE,"f82c8603-6a34-46cd-9305-3e979d524e24.4.0.1"),sQuery(id+"F4.wireOp",EDGE,"f82c8603-6a34-46cd-9305-3e979d524e24.4.0.2")])]})});
            var Q357;
            Q357=makeQuery(id+"F5.boolean.opBoolean","COPY",EDGE,{"derivedFrom":makeQuery(id+"F5.opExtrude","SWEPT_EDGE",EDGE,{"disambiguationData":[OSD([sQuery(id+"F4.wireOp",EDGE,"E18"),sQuery(id+"F4.wireOp",EDGE,"E21")])]})});
            var Q358;
            Q358=makeQuery(id+"F5.boolean.opBoolean","COPY",EDGE,{"derivedFrom":makeQuery(id+"F5.opExtrude","CAP_EDGE",EDGE,{"disambiguationData":[OSD([sQuery(id+"F4.wireOp",EDGE,"f82c8603-6a34-46cd-9305-3e979d524e24.5.0.0")])],"isStart":true})});
            var Q359;
            Q359=makeQuery(id+"F5.boolean.opBoolean","COPY",EDGE,{"derivedFrom":makeQuery(id+"F5.opExtrude","TWEAK_EDGE",EDGE,{"derivedFrom":[makeQuery(id+"F1.opExtrude","SWEPT_FACE",FACE,{"disambiguationData":[OSD([sQuery(id+"F0.wireOp",EDGE,"E4")])]}),makeQuery(id+"F4.imprint","IMPRINT",EDGE,{"derivedFrom":sQuery(id+"F4.wireOp",EDGE,"f82c8603-6a34-46cd-9305-3e979d524e24.5.0.0")})]})});
            var Q360;
            Q360=makeQuery(id+"F5.boolean.opBoolean","COPY",EDGE,{"derivedFrom":makeQuery(id+"F5.opExtrude","SWEPT_EDGE",EDGE,{"disambiguationData":[OSD([sQuery(id+"F4.wireOp",EDGE,"f82c8603-6a34-46cd-9305-3e979d524e24.1.0.0"),sQuery(id+"F4.wireOp",EDGE,"f82c8603-6a34-46cd-9305-3e979d524e24.1.0.2")])]})});
            var Q361;
            Q361=makeQuery(id+"F5.boolean.opBoolean","COPY",EDGE,{"derivedFrom":makeQuery(id+"F5.opExtrude","SWEPT_EDGE",EDGE,{"disambiguationData":[OSD([sQuery(id+"F4.wireOp",EDGE,"f82c8603-6a34-46cd-9305-3e979d524e24.1.0.0"),sQuery(id+"F4.wireOp",EDGE,"f82c8603-6a34-46cd-9305-3e979d524e24.1.0.3")])]})});
            var Q362;
            Q362=makeQuery(id+"F5.boolean.opBoolean","COPY",EDGE,{"derivedFrom":makeQuery(id+"F5.opExtrude","CAP_EDGE",EDGE,{"disambiguationData":[OSD([sQuery(id+"F4.wireOp",EDGE,"f82c8603-6a34-46cd-9305-3e979d524e24.5.0.1")])],"isStart":true})});
            var Q363;
            Q363=makeQuery(id+"F5.boolean.opBoolean","COPY",EDGE,{"derivedFrom":makeQuery(id+"F5.opExtrude","SWEPT_EDGE",EDGE,{"disambiguationData":[OSD([sQuery(id+"F4.wireOp",EDGE,"f82c8603-6a34-46cd-9305-3e979d524e24.5.0.1"),sQuery(id+"F4.wireOp",EDGE,"f82c8603-6a34-46cd-9305-3e979d524e24.5.0.3")])]})});
            var Q364;
            Q364=makeQuery(id+"F5.boolean.opBoolean","COPY",EDGE,{"derivedFrom":makeQuery(id+"F5.opExtrude","SWEPT_EDGE",EDGE,{"disambiguationData":[OSD([sQuery(id+"F4.wireOp",EDGE,"f82c8603-6a34-46cd-9305-3e979d524e24.1.0.1"),sQuery(id+"F4.wireOp",EDGE,"f82c8603-6a34-46cd-9305-3e979d524e24.1.0.3")])]})});
            var Q365;
            Q365=makeQuery(id+"F5.boolean.opBoolean","COPY",EDGE,{"derivedFrom":makeQuery(id+"F5.opExtrude","TWEAK_EDGE",EDGE,{"derivedFrom":[makeQuery(id+"F1.opExtrude","SWEPT_FACE",FACE,{"disambiguationData":[OSD([sQuery(id+"F0.wireOp",EDGE,"E4")])]}),makeQuery(id+"F4.imprint","IMPRINT",EDGE,{"derivedFrom":sQuery(id+"F4.wireOp",EDGE,"f82c8603-6a34-46cd-9305-3e979d524e24.5.0.2")})]})});
            var Q366;
            Q366=makeQuery(id+"F3.boolean.opBoolean","INTERSECT",EDGE,{"derivedFrom":[makeQuery(id+"F1.opExtrude","SWEPT_FACE",FACE,{"disambiguationData":[OSD([sQuery(id+"F0.wireOp",EDGE,"E6.right")])]}),makeQuery(id+"F3.opExtrude","SWEPT_FACE",FACE,{"disambiguationData":[OSD([sQuery(id+"F2.wireOp",EDGE,"E16.1.0.2")])]})]});
            var Q367;
            Q367=makeQuery(id+"F3.boolean.opBoolean","INTERSECT",EDGE,{"derivedFrom":[makeQuery(id+"F1.opExtrude","SWEPT_FACE",FACE,{"disambiguationData":[OSD([sQuery(id+"F0.wireOp",EDGE,"E6.right")])]}),makeQuery(id+"F3.opExtrude","SWEPT_FACE",FACE,{"disambiguationData":[OSD([sQuery(id+"F2.wireOp",EDGE,"E16.5.0.2")])]})]});
            var Q368;
            Q368=makeQuery(id+"F3.boolean.opBoolean","INTERSECT",EDGE,{"derivedFrom":[makeQuery(id+"F1.opExtrude","SWEPT_FACE",FACE,{"disambiguationData":[OSD([sQuery(id+"F0.wireOp",EDGE,"E0.rect.left"),sQuery(id+"F0.wireOp",EDGE,"E1.left"),sQuery(id+"F0.wireOp",EDGE,"E6.left")])]}),makeQuery(id+"F3.opExtrude","SWEPT_FACE",FACE,{"disambiguationData":[OSD([sQuery(id+"F2.wireOp",EDGE,"E16.5.0.2")])]})]});
            var Q369;
            Q369=makeQuery(id+"F3.boolean.opBoolean","INTERSECT",EDGE,{"derivedFrom":[makeQuery(id+"F1.opExtrude","SWEPT_FACE",FACE,{"disambiguationData":[OSD([sQuery(id+"F0.wireOp",EDGE,"E0.rect.left"),sQuery(id+"F0.wireOp",EDGE,"E1.left"),sQuery(id+"F0.wireOp",EDGE,"E6.left")])]}),makeQuery(id+"F3.opExtrude","SWEPT_FACE",FACE,{"disambiguationData":[OSD([sQuery(id+"F2.wireOp",EDGE,"E16.1.0.2")])]})]});
            var Q370;
            Q370=makeQuery(id+"F3.boolean.opBoolean","COPY",EDGE,{"disambiguationData":[OD(1.0)],"derivedFrom":makeQuery(id+"F3.opExtrude","SWEPT_EDGE",EDGE,{"disambiguationData":[OSD([sQuery(id+"F2.wireOp",EDGE,"E16.4.0.2"),sQuery(id+"F2.wireOp",EDGE,"E16.4.0.3")])]})});
            var Q371;
            Q371=makeQuery(id+"F3.boolean.opBoolean","COPY",EDGE,{"disambiguationData":[OD(1.0)],"derivedFrom":makeQuery(id+"F3.opExtrude","SWEPT_EDGE",EDGE,{"disambiguationData":[OSD([sQuery(id+"F2.wireOp",EDGE,"E16.6.0.2"),sQuery(id+"F2.wireOp",EDGE,"E16.6.0.3")])]})});
            var Q372;
            Q372=makeQuery(id+"F3.boolean.opBoolean","COPY",EDGE,{"disambiguationData":[OD(1.0)],"derivedFrom":makeQuery(id+"F3.opExtrude","SWEPT_EDGE",EDGE,{"disambiguationData":[OSD([sQuery(id+"F2.wireOp",EDGE,"E11"),sQuery(id+"F2.wireOp",EDGE,"E14")])]})});
            var Q373;
            Q373=makeQuery(id+"F3.boolean.opBoolean","COPY",EDGE,{"disambiguationData":[OD(1.0)],"derivedFrom":makeQuery(id+"F3.opExtrude","SWEPT_EDGE",EDGE,{"disambiguationData":[OSD([sQuery(id+"F2.wireOp",EDGE,"E16.2.0.2"),sQuery(id+"F2.wireOp",EDGE,"E16.2.0.3")])]})});
            var Q374;
            Q374=makeQuery(id+"F3.boolean.opBoolean","INTERSECT",EDGE,{"derivedFrom":[makeQuery(id+"F1.opExtrude","SWEPT_FACE",FACE,{"disambiguationData":[OSD([sQuery(id+"F0.wireOp",EDGE,"E5.right")])]}),makeQuery(id+"F3.opExtrude","SWEPT_FACE",FACE,{"disambiguationData":[OSD([sQuery(id+"F2.wireOp",EDGE,"E16.5.0.3")])]})]});
            var Q375;
            Q375=makeQuery(id+"F3.boolean.opBoolean","COPY",EDGE,{"disambiguationData":[OD(0.0)],"derivedFrom":makeQuery(id+"F3.opExtrude","SWEPT_EDGE",EDGE,{"disambiguationData":[OSD([sQuery(id+"F2.wireOp",EDGE,"E16.1.0.0"),sQuery(id+"F2.wireOp",EDGE,"E16.1.0.3")])]})});
            var Q376;
            Q376=makeQuery(id+"F3.boolean.opBoolean","INTERSECT",EDGE,{"derivedFrom":[makeQuery(id+"F1.opExtrude","SWEPT_FACE",FACE,{"disambiguationData":[OSD([sQuery(id+"F0.wireOp",EDGE,"E6.right")])]}),makeQuery(id+"F3.opExtrude","SWEPT_FACE",FACE,{"disambiguationData":[OSD([sQuery(id+"F2.wireOp",EDGE,"E16.2.0.1")])]})]});
            var Q377;
            Q377=makeQuery(id+"F3.boolean.opBoolean","INTERSECT",EDGE,{"derivedFrom":[makeQuery(id+"F1.opExtrude","SWEPT_FACE",FACE,{"disambiguationData":[OSD([sQuery(id+"F0.wireOp",EDGE,"E6.right")])]}),makeQuery(id+"F3.opExtrude","SWEPT_FACE",FACE,{"disambiguationData":[OSD([sQuery(id+"F2.wireOp",EDGE,"E16.6.0.1")])]})]});
            var Q378;
            Q378=makeQuery(id+"F3.boolean.opBoolean","COPY",EDGE,{"disambiguationData":[OD(0.0)],"derivedFrom":makeQuery(id+"F3.opExtrude","SWEPT_EDGE",EDGE,{"disambiguationData":[OSD([sQuery(id+"F2.wireOp",EDGE,"E16.7.0.0"),sQuery(id+"F2.wireOp",EDGE,"E16.7.0.1")])]})});
            var Q379;
            Q379=makeQuery(id+"F3.boolean.opBoolean","COPY",EDGE,{"disambiguationData":[OD(0.0)],"derivedFrom":makeQuery(id+"F3.opExtrude","SWEPT_EDGE",EDGE,{"disambiguationData":[OSD([sQuery(id+"F2.wireOp",EDGE,"E16.3.0.0"),sQuery(id+"F2.wireOp",EDGE,"E16.3.0.1")])]})});
            var Q380;
            Q380=makeQuery(id+"F3.boolean.opBoolean","INTERSECT",EDGE,{"derivedFrom":[makeQuery(id+"F1.opExtrude","SWEPT_FACE",FACE,{"disambiguationData":[OSD([sQuery(id+"F0.wireOp",EDGE,"E6.right")])]}),makeQuery(id+"F3.opExtrude","SWEPT_FACE",FACE,{"disambiguationData":[OSD([sQuery(id+"F2.wireOp",EDGE,"E16.6.0.0")])]})]});
            var Q381;
            Q381=makeQuery(id+"F3.boolean.opBoolean","INTERSECT",EDGE,{"derivedFrom":[makeQuery(id+"F1.opExtrude","SWEPT_FACE",FACE,{"disambiguationData":[OSD([sQuery(id+"F0.wireOp",EDGE,"E6.right")])]}),makeQuery(id+"F3.opExtrude","SWEPT_FACE",FACE,{"disambiguationData":[OSD([sQuery(id+"F2.wireOp",EDGE,"E16.2.0.0")])]})]});
            var Q382;
            Q382=makeQuery(id+"F3.boolean.opBoolean","COPY",EDGE,{"disambiguationData":[OD(1.0)],"derivedFrom":makeQuery(id+"F3.opExtrude","SWEPT_EDGE",EDGE,{"disambiguationData":[OSD([sQuery(id+"F2.wireOp",EDGE,"E16.1.0.0"),sQuery(id+"F2.wireOp",EDGE,"E16.1.0.3")])]})});
            var Q383;
            Q383=makeQuery(id+"F3.boolean.opBoolean","INTERSECT",EDGE,{"derivedFrom":[makeQuery(id+"F1.opExtrude","SWEPT_FACE",FACE,{"disambiguationData":[OSD([sQuery(id+"F0.wireOp",EDGE,"E0.rect.left"),sQuery(id+"F0.wireOp",EDGE,"E1.left"),sQuery(id+"F0.wireOp",EDGE,"E6.left")])]}),makeQuery(id+"F3.opExtrude","SWEPT_FACE",FACE,{"disambiguationData":[OSD([sQuery(id+"F2.wireOp",EDGE,"E16.2.0.1")])]})]});
            var Q384;
            Q384=makeQuery(id+"F3.boolean.opBoolean","INTERSECT",EDGE,{"derivedFrom":[makeQuery(id+"F1.opExtrude","SWEPT_FACE",FACE,{"disambiguationData":[OSD([sQuery(id+"F0.wireOp",EDGE,"E0.rect.left"),sQuery(id+"F0.wireOp",EDGE,"E1.left"),sQuery(id+"F0.wireOp",EDGE,"E6.left")])]}),makeQuery(id+"F3.opExtrude","SWEPT_FACE",FACE,{"disambiguationData":[OSD([sQuery(id+"F2.wireOp",EDGE,"E16.6.0.1")])]})]});
            var Q385;
            Q385=makeQuery(id+"F3.boolean.opBoolean","COPY",FACE,{"disambiguationData":[OD(1.0)],"derivedFrom":makeQuery(id+"F3.opExtrude","SWEPT_FACE",FACE,{"disambiguationData":[OSD([sQuery(id+"F2.wireOp",EDGE,"E16.4.0.3")])]})});
            var Q386;
            Q386=makeQuery(id+"F3.boolean.opBoolean","INTERSECT",EDGE,{"derivedFrom":[makeQuery(id+"F1.opExtrude","SWEPT_FACE",FACE,{"disambiguationData":[OSD([sQuery(id+"F0.wireOp",EDGE,"E0.rect.left"),sQuery(id+"F0.wireOp",EDGE,"E1.left"),sQuery(id+"F0.wireOp",EDGE,"E6.left")])]}),makeQuery(id+"F3.opExtrude","SWEPT_FACE",FACE,{"disambiguationData":[OSD([sQuery(id+"F2.wireOp",EDGE,"E16.7.0.0")])]})]});
            var Q387;
            Q387=makeQuery(id+"F3.boolean.opBoolean","INTERSECT",EDGE,{"derivedFrom":[makeQuery(id+"F1.opExtrude","SWEPT_FACE",FACE,{"disambiguationData":[OSD([sQuery(id+"F0.wireOp",EDGE,"E6.right")])]}),makeQuery(id+"F3.opExtrude","SWEPT_FACE",FACE,{"disambiguationData":[OSD([sQuery(id+"F2.wireOp",EDGE,"E16.3.0.0")])]})]});
            var Q388;
            Q388=makeQuery(id+"F3.boolean.opBoolean","COPY",EDGE,{"disambiguationData":[OD(1.0)],"derivedFrom":makeQuery(id+"F3.opExtrude","SWEPT_EDGE",EDGE,{"disambiguationData":[OSD([sQuery(id+"F2.wireOp",EDGE,"E16.1.0.0"),sQuery(id+"F2.wireOp",EDGE,"E16.1.0.1")])]})});
            var Q389;
            Q389=makeQuery(id+"F3.boolean.opBoolean","COPY",EDGE,{"disambiguationData":[OD(1.0)],"derivedFrom":makeQuery(id+"F3.opExtrude","SWEPT_EDGE",EDGE,{"disambiguationData":[OSD([sQuery(id+"F2.wireOp",EDGE,"E16.3.0.0"),sQuery(id+"F2.wireOp",EDGE,"E16.3.0.1")])]})});
            var Q390;
            Q390=makeQuery(id+"F3.boolean.opBoolean","COPY",EDGE,{"disambiguationData":[OD(1.0)],"derivedFrom":makeQuery(id+"F3.opExtrude","SWEPT_EDGE",EDGE,{"disambiguationData":[OSD([sQuery(id+"F2.wireOp",EDGE,"E16.5.0.0"),sQuery(id+"F2.wireOp",EDGE,"E16.5.0.1")])]})});
            var Q391;
            Q391=makeQuery(id+"F3.boolean.opBoolean","COPY",EDGE,{"disambiguationData":[OD(1.0)],"derivedFrom":makeQuery(id+"F3.opExtrude","SWEPT_EDGE",EDGE,{"disambiguationData":[OSD([sQuery(id+"F2.wireOp",EDGE,"E16.7.0.0"),sQuery(id+"F2.wireOp",EDGE,"E16.7.0.1")])]})});
            var Q392;
            Q392=makeQuery(id+"F3.boolean.opBoolean","INTERSECT",EDGE,{"derivedFrom":[makeQuery(id+"F1.opExtrude","SWEPT_FACE",FACE,{"disambiguationData":[OSD([sQuery(id+"F0.wireOp",EDGE,"E0.rect.left"),sQuery(id+"F0.wireOp",EDGE,"E1.left"),sQuery(id+"F0.wireOp",EDGE,"E6.left")])]}),makeQuery(id+"F3.opExtrude","SWEPT_FACE",FACE,{"disambiguationData":[OSD([sQuery(id+"F2.wireOp",EDGE,"E16.2.0.3")])]})]});
            var Q393;
            Q393=makeQuery(id+"F3.boolean.opBoolean","INTERSECT",EDGE,{"derivedFrom":[makeQuery(id+"F1.opExtrude","SWEPT_FACE",FACE,{"disambiguationData":[OSD([sQuery(id+"F0.wireOp",EDGE,"E0.rect.left"),sQuery(id+"F0.wireOp",EDGE,"E1.left"),sQuery(id+"F0.wireOp",EDGE,"E6.left")])]}),makeQuery(id+"F3.opExtrude","SWEPT_FACE",FACE,{"disambiguationData":[OSD([sQuery(id+"F2.wireOp",EDGE,"E16.6.0.3")])]})]});
            var Q394;
            Q394=makeQuery(id+"F3.boolean.opBoolean","INTERSECT",EDGE,{"derivedFrom":[makeQuery(id+"F1.opExtrude","SWEPT_FACE",FACE,{"disambiguationData":[OSD([sQuery(id+"F0.wireOp",EDGE,"E5.right")])]}),makeQuery(id+"F3.opExtrude","SWEPT_FACE",FACE,{"disambiguationData":[OSD([sQuery(id+"F2.wireOp",EDGE,"E16.2.0.3")])]})]});
            var Q395;
            Q395=makeQuery(id+"F3.boolean.opBoolean","INTERSECT",EDGE,{"derivedFrom":[makeQuery(id+"F1.opExtrude","SWEPT_FACE",FACE,{"disambiguationData":[OSD([sQuery(id+"F0.wireOp",EDGE,"E5.right")])]}),makeQuery(id+"F3.opExtrude","SWEPT_FACE",FACE,{"disambiguationData":[OSD([sQuery(id+"F2.wireOp",EDGE,"E16.6.0.3")])]})]});
            var Q396;
            Q396=makeQuery(id+"F5.boolean.opBoolean","COPY",EDGE,{"derivedFrom":makeQuery(id+"F5.opExtrude","SWEPT_EDGE",EDGE,{"disambiguationData":[OSD([sQuery(id+"F4.wireOp",EDGE,"f82c8603-6a34-46cd-9305-3e979d524e24.6.0.1"),sQuery(id+"F4.wireOp",EDGE,"f82c8603-6a34-46cd-9305-3e979d524e24.6.0.2")])]})});
            var Q397;
            Q397=makeQuery(id+"F1.opExtrude","CAP_EDGE",EDGE,{"disambiguationData":[OSD([sQuery(id+"F0.wireOp",EDGE,"E7")])],"isStart":false});
            var Q398;
            Q398=makeQuery(id+"F1.opExtrude","CAP_EDGE",EDGE,{"disambiguationData":[OSD([sQuery(id+"F0.wireOp",EDGE,"E6.top")])],"isStart":true});
            var Q399;
            Q399=makeQuery(id+"F1.opExtrude","CAP_EDGE",EDGE,{"disambiguationData":[OSD([sQuery(id+"F0.wireOp",EDGE,"E6.top")])],"isStart":false});
            var Q400;
            Q400=makeQuery(id+"F3.boolean.opBoolean","INTERSECT",EDGE,{"derivedFrom":[makeQuery(id+"F1.opExtrude","SWEPT_FACE",FACE,{"disambiguationData":[OSD([sQuery(id+"F0.wireOp",EDGE,"E6.right")])]}),makeQuery(id+"F3.opExtrude","SWEPT_FACE",FACE,{"disambiguationData":[OSD([sQuery(id+"F2.wireOp",EDGE,"E16.1.0.1")])]})]});
            var Q401;
            Q401=makeQuery(id+"F3.boolean.opBoolean","INTERSECT",EDGE,{"derivedFrom":[makeQuery(id+"F1.opExtrude","SWEPT_FACE",FACE,{"disambiguationData":[OSD([sQuery(id+"F0.wireOp",EDGE,"E6.right")])]}),makeQuery(id+"F3.opExtrude","SWEPT_FACE",FACE,{"disambiguationData":[OSD([sQuery(id+"F2.wireOp",EDGE,"E16.5.0.1")])]})]});
            var Q402;
            Q402=makeQuery(id+"F3.boolean.opBoolean","COPY",EDGE,{"disambiguationData":[OD(1.0)],"derivedFrom":makeQuery(id+"F3.opExtrude","SWEPT_EDGE",EDGE,{"disambiguationData":[OSD([sQuery(id+"F2.wireOp",EDGE,"E16.4.0.1"),sQuery(id+"F2.wireOp",EDGE,"E16.4.0.2")])]})});
            var Q403;
            Q403=makeQuery(id+"F3.boolean.opBoolean","COPY",EDGE,{"disambiguationData":[OD(1.0)],"derivedFrom":makeQuery(id+"F3.opExtrude","SWEPT_EDGE",EDGE,{"disambiguationData":[OSD([sQuery(id+"F2.wireOp",EDGE,"E16.6.0.1"),sQuery(id+"F2.wireOp",EDGE,"E16.6.0.2")])]})});
            var Q404;
            Q404=makeQuery(id+"F3.boolean.opBoolean","INTERSECT",EDGE,{"derivedFrom":[makeQuery(id+"F1.opExtrude","SWEPT_FACE",FACE,{"disambiguationData":[OSD([sQuery(id+"F0.wireOp",EDGE,"E0.rect.left"),sQuery(id+"F0.wireOp",EDGE,"E1.left"),sQuery(id+"F0.wireOp",EDGE,"E6.left")])]}),makeQuery(id+"F3.opExtrude","SWEPT_FACE",FACE,{"disambiguationData":[OSD([sQuery(id+"F2.wireOp",EDGE,"E16.1.0.1")])]})]});
            var Q405;
            Q405=makeQuery(id+"F3.boolean.opBoolean","COPY",EDGE,{"disambiguationData":[OD(1.0)],"derivedFrom":makeQuery(id+"F3.opExtrude","SWEPT_EDGE",EDGE,{"disambiguationData":[OSD([sQuery(id+"F2.wireOp",EDGE,"E16.2.0.1"),sQuery(id+"F2.wireOp",EDGE,"E16.2.0.2")])]})});
            var Q406;
            Q406=makeQuery(id+"F3.boolean.opBoolean","COPY",EDGE,{"disambiguationData":[OD(1.0)],"derivedFrom":makeQuery(id+"F3.opExtrude","SWEPT_EDGE",EDGE,{"disambiguationData":[OSD([sQuery(id+"F2.wireOp",EDGE,"E11"),sQuery(id+"F2.wireOp",EDGE,"E15")])]})});
            var Q407;
            Q407=makeQuery(id+"F3.boolean.opBoolean","INTERSECT",EDGE,{"derivedFrom":[makeQuery(id+"F1.opExtrude","SWEPT_FACE",FACE,{"disambiguationData":[OSD([sQuery(id+"F0.wireOp",EDGE,"E0.rect.left"),sQuery(id+"F0.wireOp",EDGE,"E1.left"),sQuery(id+"F0.wireOp",EDGE,"E6.left")])]}),makeQuery(id+"F3.opExtrude","SWEPT_FACE",FACE,{"disambiguationData":[OSD([sQuery(id+"F2.wireOp",EDGE,"E16.5.0.0")])]})]});
            var Q408;
            Q408=makeQuery(id+"F3.boolean.opBoolean","COPY",EDGE,{"disambiguationData":[OD(1.0)],"derivedFrom":makeQuery(id+"F3.opExtrude","SWEPT_EDGE",EDGE,{"disambiguationData":[OSD([sQuery(id+"F2.wireOp",EDGE,"E10"),sQuery(id+"F2.wireOp",EDGE,"E15")])]})});
            var Q409;
            Q409=makeQuery(id+"F3.boolean.opBoolean","INTERSECT",EDGE,{"derivedFrom":[makeQuery(id+"F1.opExtrude","SWEPT_FACE",FACE,{"disambiguationData":[OSD([sQuery(id+"F0.wireOp",EDGE,"E5.right")])]}),makeQuery(id+"F3.opExtrude","SWEPT_FACE",FACE,{"disambiguationData":[OSD([sQuery(id+"F2.wireOp",EDGE,"E15")])]})]});
            var Q410;
            Q410=makeQuery(id+"F3.boolean.opBoolean","INTERSECT",EDGE,{"derivedFrom":[makeQuery(id+"F1.opExtrude","SWEPT_FACE",FACE,{"disambiguationData":[OSD([sQuery(id+"F0.wireOp",EDGE,"E0.rect.left"),sQuery(id+"F0.wireOp",EDGE,"E1.left"),sQuery(id+"F0.wireOp",EDGE,"E6.left")])]}),makeQuery(id+"F3.opExtrude","SWEPT_FACE",FACE,{"disambiguationData":[OSD([sQuery(id+"F2.wireOp",EDGE,"E15")])]})]});
            var Q411;
            Q411=makeQuery(id+"F3.boolean.opBoolean","COPY",EDGE,{"disambiguationData":[OD(1.0)],"derivedFrom":makeQuery(id+"F3.opExtrude","SWEPT_EDGE",EDGE,{"disambiguationData":[OSD([sQuery(id+"F2.wireOp",EDGE,"E16.4.0.0"),sQuery(id+"F2.wireOp",EDGE,"E16.4.0.1")])]})});
            var Q412;
            Q412=makeQuery(id+"F3.boolean.opBoolean","COPY",FACE,{"disambiguationData":[OD(1.0)],"derivedFrom":makeQuery(id+"F3.opExtrude","SWEPT_FACE",FACE,{"disambiguationData":[OSD([sQuery(id+"F2.wireOp",EDGE,"E16.3.0.3")])]})});
            var Q413;
            Q413=makeQuery(id+"F3.boolean.opBoolean","COPY",FACE,{"disambiguationData":[OD(1.0)],"derivedFrom":makeQuery(id+"F3.opExtrude","SWEPT_FACE",FACE,{"disambiguationData":[OSD([sQuery(id+"F2.wireOp",EDGE,"E16.5.0.3")])]})});
            var Q414;
            Q414=makeQuery(id+"F3.boolean.opBoolean","INTERSECT",EDGE,{"derivedFrom":[makeQuery(id+"F1.opExtrude","SWEPT_FACE",FACE,{"disambiguationData":[OSD([sQuery(id+"F0.wireOp",EDGE,"E0.rect.left"),sQuery(id+"F0.wireOp",EDGE,"E1.left"),sQuery(id+"F0.wireOp",EDGE,"E6.left")])]}),makeQuery(id+"F3.opExtrude","SWEPT_FACE",FACE,{"disambiguationData":[OSD([sQuery(id+"F2.wireOp",EDGE,"E16.4.0.2")])]})]});
            var Q415;
            Q415=makeQuery(id+"F3.boolean.opBoolean","INTERSECT",EDGE,{"derivedFrom":[makeQuery(id+"F1.opExtrude","SWEPT_FACE",FACE,{"disambiguationData":[OSD([sQuery(id+"F0.wireOp",EDGE,"E0.rect.left"),sQuery(id+"F0.wireOp",EDGE,"E1.left"),sQuery(id+"F0.wireOp",EDGE,"E6.left")])]}),makeQuery(id+"F3.opExtrude","SWEPT_FACE",FACE,{"disambiguationData":[OSD([sQuery(id+"F2.wireOp",EDGE,"E14")])]})]});
            var Q416;
            Q416=makeQuery(id+"F3.boolean.opBoolean","COPY",EDGE,{"disambiguationData":[OD(0.0)],"derivedFrom":makeQuery(id+"F3.opExtrude","SWEPT_EDGE",EDGE,{"disambiguationData":[OSD([sQuery(id+"F2.wireOp",EDGE,"E16.6.0.0"),sQuery(id+"F2.wireOp",EDGE,"E16.6.0.1")])]})});
            var Q417;
            Q417=makeQuery(id+"F3.boolean.opBoolean","COPY",EDGE,{"disambiguationData":[OD(0.0)],"derivedFrom":makeQuery(id+"F3.opExtrude","SWEPT_EDGE",EDGE,{"disambiguationData":[OSD([sQuery(id+"F2.wireOp",EDGE,"E16.2.0.0"),sQuery(id+"F2.wireOp",EDGE,"E16.2.0.1")])]})});
            var Q418;
            Q418=makeQuery(id+"F3.boolean.opBoolean","INTERSECT",EDGE,{"derivedFrom":[makeQuery(id+"F1.opExtrude","SWEPT_FACE",FACE,{"disambiguationData":[OSD([sQuery(id+"F0.wireOp",EDGE,"E0.rect.left"),sQuery(id+"F0.wireOp",EDGE,"E1.left"),sQuery(id+"F0.wireOp",EDGE,"E6.left")])]}),makeQuery(id+"F3.opExtrude","SWEPT_FACE",FACE,{"disambiguationData":[OSD([sQuery(id+"F2.wireOp",EDGE,"E16.4.0.1")])]})]});
            var Q419;
            Q419=makeQuery(id+"F3.boolean.opBoolean","COPY",EDGE,{"disambiguationData":[OD(1.0)],"derivedFrom":makeQuery(id+"F3.opExtrude","SWEPT_EDGE",EDGE,{"disambiguationData":[OSD([sQuery(id+"F2.wireOp",EDGE,"E16.6.0.0"),sQuery(id+"F2.wireOp",EDGE,"E16.6.0.3")])]})});
            var Q420;
            Q420=makeQuery(id+"F3.boolean.opBoolean","COPY",EDGE,{"disambiguationData":[OD(1.0)],"derivedFrom":makeQuery(id+"F3.opExtrude","SWEPT_EDGE",EDGE,{"disambiguationData":[OSD([sQuery(id+"F2.wireOp",EDGE,"E10"),sQuery(id+"F2.wireOp",EDGE,"E14")])]})});
            var Q421;
            Q421=makeQuery(id+"F3.boolean.opBoolean","COPY",EDGE,{"disambiguationData":[OD(1.0)],"derivedFrom":makeQuery(id+"F3.opExtrude","SWEPT_EDGE",EDGE,{"disambiguationData":[OSD([sQuery(id+"F2.wireOp",EDGE,"E16.2.0.0"),sQuery(id+"F2.wireOp",EDGE,"E16.2.0.3")])]})});
            var Q422;
            Q422=makeQuery(id+"F3.boolean.opBoolean","INTERSECT",EDGE,{"derivedFrom":[makeQuery(id+"F1.opExtrude","SWEPT_FACE",FACE,{"disambiguationData":[OSD([sQuery(id+"F0.wireOp",EDGE,"E0.rect.left"),sQuery(id+"F0.wireOp",EDGE,"E1.left"),sQuery(id+"F0.wireOp",EDGE,"E6.left")])]}),makeQuery(id+"F3.opExtrude","SWEPT_FACE",FACE,{"disambiguationData":[OSD([sQuery(id+"F2.wireOp",EDGE,"E10")])]})]});
            var Q423;
            Q423=makeQuery(id+"F3.boolean.opBoolean","COPY",EDGE,{"disambiguationData":[OD(0.0)],"derivedFrom":makeQuery(id+"F3.opExtrude","SWEPT_EDGE",EDGE,{"disambiguationData":[OSD([sQuery(id+"F2.wireOp",EDGE,"E16.4.0.0"),sQuery(id+"F2.wireOp",EDGE,"E16.4.0.3")])]})});
            var Q424;
            Q424=makeQuery(id+"F3.boolean.opBoolean","COPY",EDGE,{"disambiguationData":[OD(1.0)],"derivedFrom":makeQuery(id+"F3.opExtrude","SWEPT_EDGE",EDGE,{"disambiguationData":[OSD([sQuery(id+"F2.wireOp",EDGE,"E16.1.0.2"),sQuery(id+"F2.wireOp",EDGE,"E16.1.0.3")])]})});
            var Q425;
            Q425=makeQuery(id+"F3.boolean.opBoolean","INTERSECT",EDGE,{"derivedFrom":[makeQuery(id+"F1.opExtrude","SWEPT_FACE",FACE,{"disambiguationData":[OSD([sQuery(id+"F0.wireOp",EDGE,"E5.right")])]}),makeQuery(id+"F3.opExtrude","SWEPT_FACE",FACE,{"disambiguationData":[OSD([sQuery(id+"F2.wireOp",EDGE,"E16.3.0.3")])]})]});
            var Q426;
            Q426=makeQuery(id+"F3.boolean.opBoolean","INTERSECT",EDGE,{"derivedFrom":[makeQuery(id+"F1.opExtrude","SWEPT_FACE",FACE,{"disambiguationData":[OSD([sQuery(id+"F0.wireOp",EDGE,"E6.right")])]}),makeQuery(id+"F3.opExtrude","SWEPT_FACE",FACE,{"disambiguationData":[OSD([sQuery(id+"F2.wireOp",EDGE,"E16.3.0.2")])]})]});
            var Q427;
            Q427=makeQuery(id+"F5.boolean.opBoolean","COPY",EDGE,{"derivedFrom":makeQuery(id+"F5.opExtrude","SWEPT_EDGE",EDGE,{"disambiguationData":[OSD([sQuery(id+"F4.wireOp",EDGE,"f82c8603-6a34-46cd-9305-3e979d524e24.4.0.0"),sQuery(id+"F4.wireOp",EDGE,"f82c8603-6a34-46cd-9305-3e979d524e24.4.0.2")])]})});
            var Q428;
            Q428=makeQuery(id+"F3.boolean.opBoolean","COPY",EDGE,{"disambiguationData":[OD(1.0)],"derivedFrom":makeQuery(id+"F3.opExtrude","SWEPT_EDGE",EDGE,{"disambiguationData":[OSD([sQuery(id+"F2.wireOp",EDGE,"E16.3.0.1"),sQuery(id+"F2.wireOp",EDGE,"E16.3.0.2")])]})});
            var Q429;
            Q429=makeQuery(id+"F3.boolean.opBoolean","COPY",EDGE,{"disambiguationData":[OD(1.0)],"derivedFrom":makeQuery(id+"F3.opExtrude","SWEPT_EDGE",EDGE,{"disambiguationData":[OSD([sQuery(id+"F2.wireOp",EDGE,"E16.7.0.1"),sQuery(id+"F2.wireOp",EDGE,"E16.7.0.2")])]})});
            var Q430;
            Q430=makeQuery(id+"F5.boolean.opBoolean","COPY",EDGE,{"derivedFrom":makeQuery(id+"F5.opExtrude","SWEPT_EDGE",EDGE,{"disambiguationData":[OSD([sQuery(id+"F4.wireOp",EDGE,"E17"),sQuery(id+"F4.wireOp",EDGE,"E22")])]})});
            var Q431;
            Q431=makeQuery(id+"F5.boolean.opBoolean","COPY",EDGE,{"derivedFrom":makeQuery(id+"F5.opExtrude","SWEPT_EDGE",EDGE,{"disambiguationData":[OSD([sQuery(id+"F4.wireOp",EDGE,"f82c8603-6a34-46cd-9305-3e979d524e24.5.0.0"),sQuery(id+"F4.wireOp",EDGE,"f82c8603-6a34-46cd-9305-3e979d524e24.5.0.2")])]})});
            var Q432;
            Q432=makeQuery(id+"F5.boolean.opBoolean","COPY",EDGE,{"derivedFrom":makeQuery(id+"F5.opExtrude","SWEPT_EDGE",EDGE,{"disambiguationData":[OSD([sQuery(id+"F4.wireOp",EDGE,"f82c8603-6a34-46cd-9305-3e979d524e24.5.0.0"),sQuery(id+"F4.wireOp",EDGE,"f82c8603-6a34-46cd-9305-3e979d524e24.5.0.3")])]})});
            var Q433;
            Q433=makeQuery(id+"F3.boolean.opBoolean","COPY",EDGE,{"disambiguationData":[OD(1.0)],"derivedFrom":makeQuery(id+"F3.opExtrude","SWEPT_EDGE",EDGE,{"disambiguationData":[OSD([sQuery(id+"F2.wireOp",EDGE,"E16.5.0.0"),sQuery(id+"F2.wireOp",EDGE,"E16.5.0.3")])]})});
            var Q434;
            Q434=makeQuery(id+"F3.boolean.opBoolean","COPY",EDGE,{"disambiguationData":[OD(1.0)],"derivedFrom":makeQuery(id+"F3.opExtrude","SWEPT_EDGE",EDGE,{"disambiguationData":[OSD([sQuery(id+"F2.wireOp",EDGE,"E16.3.0.0"),sQuery(id+"F2.wireOp",EDGE,"E16.3.0.3")])]})});
            var Q435;
            Q435=makeQuery(id+"F3.boolean.opBoolean","COPY",EDGE,{"disambiguationData":[OD(1.0)],"derivedFrom":makeQuery(id+"F3.opExtrude","SWEPT_EDGE",EDGE,{"disambiguationData":[OSD([sQuery(id+"F2.wireOp",EDGE,"E16.2.0.0"),sQuery(id+"F2.wireOp",EDGE,"E16.2.0.1")])]})});
            var Q436;
            Q436=makeQuery(id+"F3.boolean.opBoolean","COPY",EDGE,{"disambiguationData":[OD(1.0)],"derivedFrom":makeQuery(id+"F3.opExtrude","SWEPT_EDGE",EDGE,{"disambiguationData":[OSD([sQuery(id+"F2.wireOp",EDGE,"E16.6.0.0"),sQuery(id+"F2.wireOp",EDGE,"E16.6.0.1")])]})});
            var Q437;
            Q437=makeQuery(id+"F3.boolean.opBoolean","COPY",EDGE,{"disambiguationData":[OD(1.0)],"derivedFrom":makeQuery(id+"F3.opExtrude","SWEPT_EDGE",EDGE,{"disambiguationData":[OSD([sQuery(id+"F2.wireOp",EDGE,"E16.4.0.0"),sQuery(id+"F2.wireOp",EDGE,"E16.4.0.3")])]})});
            var Q438;
            Q438=makeQuery(id+"F3.boolean.opBoolean","COPY",EDGE,{"disambiguationData":[OD(1.0)],"derivedFrom":makeQuery(id+"F3.opExtrude","SWEPT_EDGE",EDGE,{"disambiguationData":[OSD([sQuery(id+"F2.wireOp",EDGE,"E16.3.0.2"),sQuery(id+"F2.wireOp",EDGE,"E16.3.0.3")])]})});
            var Q439;
            Q439=makeQuery(id+"F3.boolean.opBoolean","COPY",EDGE,{"disambiguationData":[OD(1.0)],"derivedFrom":makeQuery(id+"F3.opExtrude","SWEPT_EDGE",EDGE,{"disambiguationData":[OSD([sQuery(id+"F2.wireOp",EDGE,"E16.5.0.2"),sQuery(id+"F2.wireOp",EDGE,"E16.5.0.3")])]})});
            var Q440;
            Q440=makeQuery(id+"F3.boolean.opBoolean","COPY",EDGE,{"disambiguationData":[OD(1.0)],"derivedFrom":makeQuery(id+"F3.opExtrude","SWEPT_EDGE",EDGE,{"disambiguationData":[OSD([sQuery(id+"F2.wireOp",EDGE,"E16.5.0.1"),sQuery(id+"F2.wireOp",EDGE,"E16.5.0.2")])]})});
            var Q441;
            Q441=makeQuery(id+"F3.boolean.opBoolean","COPY",EDGE,{"disambiguationData":[OD(1.0)],"derivedFrom":makeQuery(id+"F3.opExtrude","SWEPT_EDGE",EDGE,{"disambiguationData":[OSD([sQuery(id+"F2.wireOp",EDGE,"E16.1.0.1"),sQuery(id+"F2.wireOp",EDGE,"E16.1.0.2")])]})});
            fillet(context, id + "F6", {"entities" : qUnion([Q0, Q1, Q2, Q3, Q4, Q5, Q6, Q7, Q8, Q9, Q10, Q11, Q12, Q13, Q14, Q15, Q16, Q17, Q18, Q19, Q20, Q21, Q22, Q23, Q24, Q25, Q26, Q27, Q28, Q29, Q30, Q31, Q32, Q33, Q34, Q35, Q36, Q37, Q38, Q39, Q40, Q41, Q42, Q43, Q44, Q45, Q46, Q47, Q48, Q49, Q50, Q51, Q52, Q53, Q54, Q55, Q56, Q57, Q58, Q59, Q60, Q61, Q62, Q63, Q64, Q65, Q66, Q67, Q68, Q69, Q70, Q71, Q72, Q73, Q74, Q75, Q76, Q77, Q78, Q79, Q80, Q81, Q82, Q83, Q84, Q85, Q86, Q87, Q88, Q89, Q90, Q91, Q92, Q93, Q94, Q95, Q96, Q97, Q98, Q99, Q100, Q101, Q102, Q103, Q104, Q105, Q106, Q107, Q108, Q109, Q110, Q111, Q112, Q113, Q114, Q115, Q116, Q117, Q118, Q119, Q120, Q121, Q122, Q123, Q124, Q125, Q126, Q127, Q128, Q129, Q130, Q131, Q132, Q133, Q134, Q135, Q136, Q137, Q138, Q139, Q140, Q141, Q142, Q143, Q144, Q145, Q146, Q147, Q148, Q149, Q150, Q151, Q152, Q153, Q154, Q155, Q156, Q157, Q158, Q159, Q160, Q161, Q162, Q163, Q164, Q165, Q166, Q167, Q168, Q169, Q170, Q171, Q172, Q173, Q174, Q175, Q176, Q177, Q178, Q179, Q180, Q181, Q182, Q183, Q184, Q185, Q186, Q187, Q188, Q189, Q190, Q191, Q192, Q193, Q194, Q195, Q196, Q197, Q198, Q199, Q200, Q201, Q202, Q203, Q204, Q205, Q206, Q207, Q208, Q209, Q210, Q211, Q212, Q213, Q214, Q215, Q216, Q217, Q218, Q219, Q220, Q221, Q222, Q223, Q224, Q225, Q226, Q227, Q228, Q229, Q230, Q231, Q232, Q233, Q234, Q235, Q236, Q237, Q238, Q239, Q240, Q241, Q242, Q243, Q244, Q245, Q246, Q247, Q248, Q249, Q250, Q251, Q252, Q253, Q254, Q255, Q256, Q257, Q258, Q259, Q260, Q261, Q262, Q263, Q264, Q265, Q266, Q267, Q268, Q269, Q270, Q271, Q272, Q273, Q274, Q275, Q276, Q277, Q278, Q279, Q280, Q281, Q282, Q283, Q284, Q285, Q286, Q287, Q288, Q289, Q290, Q291, Q292, Q293, Q294, Q295, Q296, Q297, Q298, Q299, Q300, Q301, Q302, Q303, Q304, Q305, Q306, Q307, Q308, Q309, Q310, Q311, Q312, Q313, Q314, Q315, Q316, Q317, Q318, Q319, Q320, Q321, Q322, Q323, Q324, Q325, Q326, Q327, Q328, Q329, Q330, Q331, Q332, Q333, Q334, Q335, Q336, Q337, Q338, Q339, Q340, Q341, Q342, Q343, Q344, Q345, Q346, Q347, Q348, Q349, Q350, Q351, Q352, Q353, Q354, Q355, Q356, Q357, Q358, Q359, Q360, Q361, Q362, Q363, Q364, Q365, Q366, Q367, Q368, Q369, Q370, Q371, Q372, Q373, Q374, Q375, Q376, Q377, Q378, Q379, Q380, Q381, Q382, Q383, Q384, Q385, Q386, Q387, Q388, Q389, Q390, Q391, Q392, Q393, Q394, Q395, Q396, Q397, Q398, Q399, Q400, Q401, Q402, Q403, Q404, Q405, Q406, Q407, Q408, Q409, Q410, Q411, Q412, Q413, Q414, Q415, Q416, Q417, Q418, Q419, Q420, Q421, Q422, Q423, Q424, Q425, Q426, Q427, Q428, Q429, Q430, Q431, Q432, Q433, Q434, Q435, Q436, Q437, Q438, Q439, Q440, Q441]), "radius" : 0.25 * mm, "tangentPropagation" : true, "allowEdgeOverflow" : false});
        }
    });
